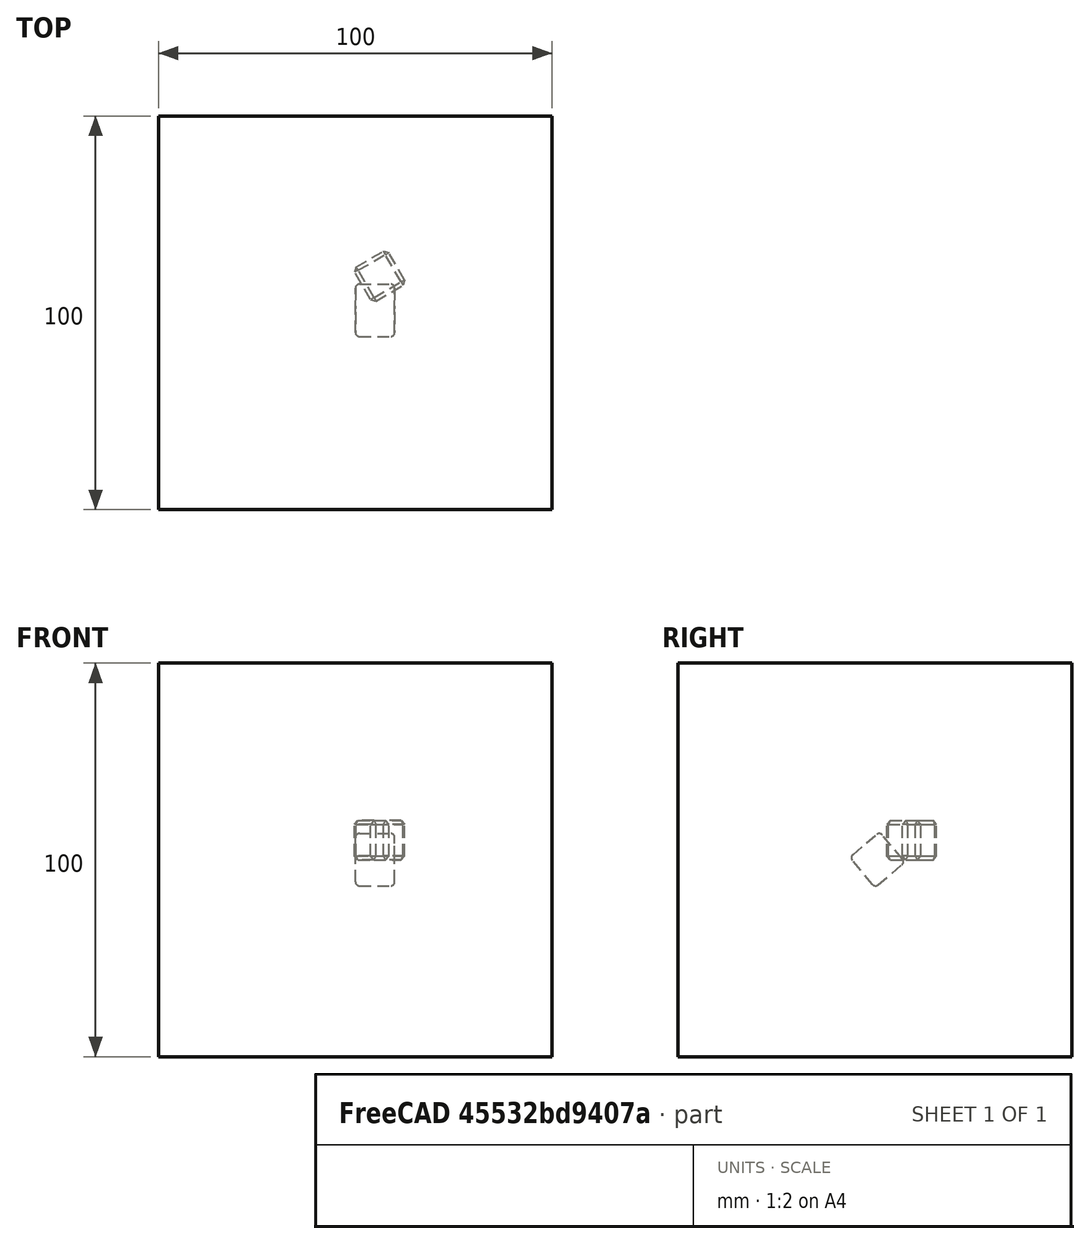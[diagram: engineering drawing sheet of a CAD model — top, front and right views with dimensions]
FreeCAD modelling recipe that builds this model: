
FCSTD DOCUMENT  (FreeCAD 0.21R33694 (Git))
Label: Chamfer_and_fillet
License: All rights reserved
objects: App::DocumentObjectGroupPython×1251, App::Part×3, Part::Box×2, Part::FeaturePython×1, Part::Chamfer×1, Part::Fillet×1
note: 5 computed .brp shape members not serialized (recipe doc carries the construction recipe); baked Part::Feature solids carry a one-line shape summary decoded from their .brp

FEATURE [App::DocumentObjectGroupPython] HALFPI  # scripted group (container) (typed FeaturePython)
  name = HALFPI
  value = pi/2.
FEATURE [App::DocumentObjectGroupPython] PI  # scripted group (container) (typed FeaturePython)
  name = PI
  value = 1.*pi
FEATURE [App::DocumentObjectGroupPython] TWOPI  # scripted group (container) (typed FeaturePython)
  name = TWOPI
  value = 2.*pi
FEATURE [App::DocumentObjectGroupPython] Constants  # scripted group (container) (typed FeaturePython)
  Group = -> [HALFPI,PI,TWOPI]
FEATURE [App::DocumentObjectGroupPython] Variables  # scripted group (container) (typed FeaturePython)
FEATURE [App::DocumentObjectGroupPython] Quantities  # scripted group (container) (typed FeaturePython)
FEATURE [App::DocumentObjectGroupPython] Isotopes  # scripted group (container) (typed FeaturePython)
FEATURE [App::DocumentObjectGroupPython] Elements  # scripted group (container) (typed FeaturePython)
FEATURE [App::DocumentObjectGroupPython] Matrix  # scripted group (container) (typed FeaturePython)
FEATURE [App::DocumentObjectGroupPython] Surfaces  # scripted group (container) (typed FeaturePython)
FEATURE [App::DocumentObjectGroupPython] Opticals  # scripted group (container) (typed FeaturePython)
  Group = -> [Matrix,Surfaces]
FEATURE [App::DocumentObjectGroupPython] G4Isotopes  # scripted group (container) (typed FeaturePython)
FEATURE [App::DocumentObjectGroupPython] H_element  # scripted group (container) (typed FeaturePython)
  Z = 1
  atom_value = 1.008
  formula = H
  name = H_element
FEATURE [App::DocumentObjectGroupPython] He_element  # scripted group (container) (typed FeaturePython)
  Z = 2
  atom_value = 4.0026
  formula = He
  name = He_element
FEATURE [App::DocumentObjectGroupPython] Li_element  # scripted group (container) (typed FeaturePython)
  Z = 3
  atom_value = 6.94
  formula = Li
  name = Li_element
FEATURE [App::DocumentObjectGroupPython] Be_element  # scripted group (container) (typed FeaturePython)
  Z = 4
  atom_value = 9.01218
  formula = Be
  name = Be_element
FEATURE [App::DocumentObjectGroupPython] B_element  # scripted group (container) (typed FeaturePython)
  Z = 5
  atom_value = 10.81
  formula = B
  name = B_element
FEATURE [App::DocumentObjectGroupPython] C_element  # scripted group (container) (typed FeaturePython)
  Z = 6
  atom_value = 12.011
  formula = C
  name = C_element
FEATURE [App::DocumentObjectGroupPython] N_element  # scripted group (container) (typed FeaturePython)
  Z = 7
  atom_value = 14.007
  formula = N
  name = N_element
FEATURE [App::DocumentObjectGroupPython] O_element  # scripted group (container) (typed FeaturePython)
  Z = 8
  atom_value = 15.999
  formula = O
  name = O_element
FEATURE [App::DocumentObjectGroupPython] F_element  # scripted group (container) (typed FeaturePython)
  Z = 9
  atom_value = 18.9984
  formula = F
  name = F_element
FEATURE [App::DocumentObjectGroupPython] Ne_element  # scripted group (container) (typed FeaturePython)
  Z = 10
  atom_value = 20.1797
  formula = Ne
  name = Ne_element
FEATURE [App::DocumentObjectGroupPython] Na_element  # scripted group (container) (typed FeaturePython)
  Z = 11
  atom_value = 22.9898
  formula = Na
  name = Na_element
FEATURE [App::DocumentObjectGroupPython] Mg_element  # scripted group (container) (typed FeaturePython)
  Z = 12
  atom_value = 24.305
  formula = Mg
  name = Mg_element
FEATURE [App::DocumentObjectGroupPython] Al_element  # scripted group (container) (typed FeaturePython)
  Z = 13
  atom_value = 26.9815
  formula = Al
  name = Al_element
FEATURE [App::DocumentObjectGroupPython] Si_element  # scripted group (container) (typed FeaturePython)
  Z = 14
  atom_value = 28.085
  formula = Si
  name = Si_element
FEATURE [App::DocumentObjectGroupPython] P_element  # scripted group (container) (typed FeaturePython)
  Z = 15
  atom_value = 30.9738
  formula = P
  name = P_element
FEATURE [App::DocumentObjectGroupPython] S_element  # scripted group (container) (typed FeaturePython)
  Z = 16
  atom_value = 32.06
  formula = S
  name = S_element
FEATURE [App::DocumentObjectGroupPython] Cl_element  # scripted group (container) (typed FeaturePython)
  Z = 17
  atom_value = 35.45
  formula = Cl
  name = Cl_element
FEATURE [App::DocumentObjectGroupPython] Ar_element  # scripted group (container) (typed FeaturePython)
  Z = 18
  atom_value = 39.95
  formula = Ar
  name = Ar_element
FEATURE [App::DocumentObjectGroupPython] K_element  # scripted group (container) (typed FeaturePython)
  Z = 19
  atom_value = 39.0983
  formula = K
  name = K_element
FEATURE [App::DocumentObjectGroupPython] Ca_element  # scripted group (container) (typed FeaturePython)
  Z = 20
  atom_value = 40.078
  formula = Ca
  name = Ca_element
FEATURE [App::DocumentObjectGroupPython] Sc_element  # scripted group (container) (typed FeaturePython)
  Z = 21
  atom_value = 44.9559
  formula = Sc
  name = Sc_element
FEATURE [App::DocumentObjectGroupPython] Ti_element  # scripted group (container) (typed FeaturePython)
  Z = 22
  atom_value = 47.867
  formula = Ti
  name = Ti_element
FEATURE [App::DocumentObjectGroupPython] V_element  # scripted group (container) (typed FeaturePython)
  Z = 23
  atom_value = 50.9415
  formula = V
  name = V_element
FEATURE [App::DocumentObjectGroupPython] Cr_element  # scripted group (container) (typed FeaturePython)
  Z = 24
  atom_value = 51.9961
  formula = Cr
  name = Cr_element
FEATURE [App::DocumentObjectGroupPython] Mn_element  # scripted group (container) (typed FeaturePython)
  Z = 25
  atom_value = 54.938
  formula = Mn
  name = Mn_element
FEATURE [App::DocumentObjectGroupPython] Fe_element  # scripted group (container) (typed FeaturePython)
  Z = 26
  atom_value = 55.845
  formula = Fe
  name = Fe_element
FEATURE [App::DocumentObjectGroupPython] Co_element  # scripted group (container) (typed FeaturePython)
  Z = 27
  atom_value = 58.9332
  formula = Co
  name = Co_element
FEATURE [App::DocumentObjectGroupPython] Ni_element  # scripted group (container) (typed FeaturePython)
  Z = 28
  atom_value = 58.6934
  formula = Ni
  name = Ni_element
FEATURE [App::DocumentObjectGroupPython] Cu_element  # scripted group (container) (typed FeaturePython)
  Z = 29
  atom_value = 63.546
  formula = Cu
  name = Cu_element
FEATURE [App::DocumentObjectGroupPython] Zn_element  # scripted group (container) (typed FeaturePython)
  Z = 30
  atom_value = 65.38
  formula = Zn
  name = Zn_element
FEATURE [App::DocumentObjectGroupPython] Ga_element  # scripted group (container) (typed FeaturePython)
  Z = 31
  atom_value = 69.723
  formula = Ga
  name = Ga_element
FEATURE [App::DocumentObjectGroupPython] Ge_element  # scripted group (container) (typed FeaturePython)
  Z = 32
  atom_value = 72.63
  formula = Ge
  name = Ge_element
FEATURE [App::DocumentObjectGroupPython] As_element  # scripted group (container) (typed FeaturePython)
  Z = 33
  atom_value = 74.9216
  formula = As
  name = As_element
FEATURE [App::DocumentObjectGroupPython] Se_element  # scripted group (container) (typed FeaturePython)
  Z = 34
  atom_value = 78.971
  formula = Se
  name = Se_element
FEATURE [App::DocumentObjectGroupPython] Br_element  # scripted group (container) (typed FeaturePython)
  Z = 35
  atom_value = 79.904
  formula = Br
  name = Br_element
FEATURE [App::DocumentObjectGroupPython] Kr_element  # scripted group (container) (typed FeaturePython)
  Z = 36
  atom_value = 83.798
  formula = Kr
  name = Kr_element
FEATURE [App::DocumentObjectGroupPython] Rb_element  # scripted group (container) (typed FeaturePython)
  Z = 37
  atom_value = 85.4678
  formula = Rb
  name = Rb_element
FEATURE [App::DocumentObjectGroupPython] Sr_element  # scripted group (container) (typed FeaturePython)
  Z = 38
  atom_value = 87.62
  formula = Sr
  name = Sr_element
FEATURE [App::DocumentObjectGroupPython] Y_element  # scripted group (container) (typed FeaturePython)
  Z = 39
  atom_value = 88.9058
  formula = Y
  name = Y_element
FEATURE [App::DocumentObjectGroupPython] Zr_element  # scripted group (container) (typed FeaturePython)
  Z = 40
  atom_value = 91.224
  formula = Zr
  name = Zr_element
FEATURE [App::DocumentObjectGroupPython] Nb_element  # scripted group (container) (typed FeaturePython)
  Z = 41
  atom_value = 92.9064
  formula = Nb
  name = Nb_element
FEATURE [App::DocumentObjectGroupPython] Mo_element  # scripted group (container) (typed FeaturePython)
  Z = 42
  atom_value = 95.95
  formula = Mo
  name = Mo_element
FEATURE [App::DocumentObjectGroupPython] Tc_element  # scripted group (container) (typed FeaturePython)
  Z = 43
  atom_value = 97
  formula = Tc
  name = Tc_element
FEATURE [App::DocumentObjectGroupPython] Ru_element  # scripted group (container) (typed FeaturePython)
  Z = 44
  atom_value = 101.07
  formula = Ru
  name = Ru_element
FEATURE [App::DocumentObjectGroupPython] Rh_element  # scripted group (container) (typed FeaturePython)
  Z = 45
  atom_value = 102.905
  formula = Rh
  name = Rh_element
FEATURE [App::DocumentObjectGroupPython] Pd_element  # scripted group (container) (typed FeaturePython)
  Z = 46
  atom_value = 106.42
  formula = Pd
  name = Pd_element
FEATURE [App::DocumentObjectGroupPython] Ag_element  # scripted group (container) (typed FeaturePython)
  Z = 47
  atom_value = 107.868
  formula = Ag
  name = Ag_element
FEATURE [App::DocumentObjectGroupPython] Cd_element  # scripted group (container) (typed FeaturePython)
  Z = 48
  atom_value = 112.414
  formula = Cd
  name = Cd_element
FEATURE [App::DocumentObjectGroupPython] In_element  # scripted group (container) (typed FeaturePython)
  Z = 49
  atom_value = 114.818
  formula = In
  name = In_element
FEATURE [App::DocumentObjectGroupPython] Sn_element  # scripted group (container) (typed FeaturePython)
  Z = 50
  atom_value = 118.71
  formula = Sn
  name = Sn_element
FEATURE [App::DocumentObjectGroupPython] Sb_element  # scripted group (container) (typed FeaturePython)
  Z = 51
  atom_value = 121.76
  formula = Sb
  name = Sb_element
FEATURE [App::DocumentObjectGroupPython] Te_element  # scripted group (container) (typed FeaturePython)
  Z = 52
  atom_value = 127.6
  formula = Te
  name = Te_element
FEATURE [App::DocumentObjectGroupPython] I_element  # scripted group (container) (typed FeaturePython)
  Z = 53
  atom_value = 126.904
  formula = I
  name = I_element
FEATURE [App::DocumentObjectGroupPython] Xe_element  # scripted group (container) (typed FeaturePython)
  Z = 54
  atom_value = 131.293
  formula = Xe
  name = Xe_element
FEATURE [App::DocumentObjectGroupPython] Cs_element  # scripted group (container) (typed FeaturePython)
  Z = 55
  atom_value = 132.905
  formula = Cs
  name = Cs_element
FEATURE [App::DocumentObjectGroupPython] Ba_element  # scripted group (container) (typed FeaturePython)
  Z = 56
  atom_value = 137.327
  formula = Ba
  name = Ba_element
FEATURE [App::DocumentObjectGroupPython] La_element  # scripted group (container) (typed FeaturePython)
  Z = 57
  atom_value = 138.905
  formula = La
  name = La_element
FEATURE [App::DocumentObjectGroupPython] Ce_element  # scripted group (container) (typed FeaturePython)
  Z = 58
  atom_value = 140.116
  formula = Ce
  name = Ce_element
FEATURE [App::DocumentObjectGroupPython] Pr_element  # scripted group (container) (typed FeaturePython)
  Z = 59
  atom_value = 140.908
  formula = Pr
  name = Pr_element
FEATURE [App::DocumentObjectGroupPython] Nd_element  # scripted group (container) (typed FeaturePython)
  Z = 60
  atom_value = 144.242
  formula = Nd
  name = Nd_element
FEATURE [App::DocumentObjectGroupPython] Pm_element  # scripted group (container) (typed FeaturePython)
  Z = 61
  atom_value = 145
  formula = Pm
  name = Pm_element
FEATURE [App::DocumentObjectGroupPython] Sm_element  # scripted group (container) (typed FeaturePython)
  Z = 62
  atom_value = 150.36
  formula = Sm
  name = Sm_element
FEATURE [App::DocumentObjectGroupPython] Eu_element  # scripted group (container) (typed FeaturePython)
  Z = 63
  atom_value = 151.964
  formula = Eu
  name = Eu_element
FEATURE [App::DocumentObjectGroupPython] Gd_element  # scripted group (container) (typed FeaturePython)
  Z = 64
  atom_value = 157.25
  formula = Gd
  name = Gd_element
FEATURE [App::DocumentObjectGroupPython] Tb_element  # scripted group (container) (typed FeaturePython)
  Z = 65
  atom_value = 158.925
  formula = Tb
  name = Tb_element
FEATURE [App::DocumentObjectGroupPython] Dy_element  # scripted group (container) (typed FeaturePython)
  Z = 66
  atom_value = 162.5
  formula = Dy
  name = Dy_element
FEATURE [App::DocumentObjectGroupPython] Ho_element  # scripted group (container) (typed FeaturePython)
  Z = 67
  atom_value = 164.93
  formula = Ho
  name = Ho_element
FEATURE [App::DocumentObjectGroupPython] Er_element  # scripted group (container) (typed FeaturePython)
  Z = 68
  atom_value = 167.259
  formula = Er
  name = Er_element
FEATURE [App::DocumentObjectGroupPython] Tm_element  # scripted group (container) (typed FeaturePython)
  Z = 69
  atom_value = 168.934
  formula = Tm
  name = Tm_element
FEATURE [App::DocumentObjectGroupPython] Yb_element  # scripted group (container) (typed FeaturePython)
  Z = 70
  atom_value = 173.045
  formula = Yb
  name = Yb_element
FEATURE [App::DocumentObjectGroupPython] Lu_element  # scripted group (container) (typed FeaturePython)
  Z = 71
  atom_value = 174.967
  formula = Lu
  name = Lu_element
FEATURE [App::DocumentObjectGroupPython] Hf_element  # scripted group (container) (typed FeaturePython)
  Z = 72
  atom_value = 178.49
  formula = Hf
  name = Hf_element
FEATURE [App::DocumentObjectGroupPython] Ta_element  # scripted group (container) (typed FeaturePython)
  Z = 73
  atom_value = 180.948
  formula = Ta
  name = Ta_element
FEATURE [App::DocumentObjectGroupPython] W_element  # scripted group (container) (typed FeaturePython)
  Z = 74
  atom_value = 183.84
  formula = W
  name = W_element
FEATURE [App::DocumentObjectGroupPython] Re_element  # scripted group (container) (typed FeaturePython)
  Z = 75
  atom_value = 186.207
  formula = Re
  name = Re_element
FEATURE [App::DocumentObjectGroupPython] Os_element  # scripted group (container) (typed FeaturePython)
  Z = 76
  atom_value = 190.23
  formula = Os
  name = Os_element
FEATURE [App::DocumentObjectGroupPython] Ir_element  # scripted group (container) (typed FeaturePython)
  Z = 77
  atom_value = 192.217
  formula = Ir
  name = Ir_element
FEATURE [App::DocumentObjectGroupPython] Pt_element  # scripted group (container) (typed FeaturePython)
  Z = 78
  atom_value = 195.084
  formula = Pt
  name = Pt_element
FEATURE [App::DocumentObjectGroupPython] Au_element  # scripted group (container) (typed FeaturePython)
  Z = 79
  atom_value = 196.967
  formula = Au
  name = Au_element
FEATURE [App::DocumentObjectGroupPython] Hg_element  # scripted group (container) (typed FeaturePython)
  Z = 80
  atom_value = 200.592
  formula = Hg
  name = Hg_element
FEATURE [App::DocumentObjectGroupPython] Tl_element  # scripted group (container) (typed FeaturePython)
  Z = 81
  atom_value = 204.38
  formula = Tl
  name = Tl_element
FEATURE [App::DocumentObjectGroupPython] Pb_element  # scripted group (container) (typed FeaturePython)
  Z = 82
  atom_value = 207.2
  formula = Pb
  name = Pb_element
FEATURE [App::DocumentObjectGroupPython] Bi_element  # scripted group (container) (typed FeaturePython)
  Z = 83
  atom_value = 208.98
  formula = Bi
  name = Bi_element
FEATURE [App::DocumentObjectGroupPython] Po_element  # scripted group (container) (typed FeaturePython)
  Z = 84
  atom_value = 209
  formula = Po
  name = Po_element
FEATURE [App::DocumentObjectGroupPython] At_element  # scripted group (container) (typed FeaturePython)
  Z = 85
  atom_value = 210
  formula = At
  name = At_element
FEATURE [App::DocumentObjectGroupPython] Rn_element  # scripted group (container) (typed FeaturePython)
  Z = 86
  atom_value = 222
  formula = Rn
  name = Rn_element
FEATURE [App::DocumentObjectGroupPython] Fr_element  # scripted group (container) (typed FeaturePython)
  Z = 87
  atom_value = 223
  formula = Fr
  name = Fr_element
FEATURE [App::DocumentObjectGroupPython] Ra_element  # scripted group (container) (typed FeaturePython)
  Z = 88
  atom_value = 226
  formula = Ra
  name = Ra_element
FEATURE [App::DocumentObjectGroupPython] Ac_element  # scripted group (container) (typed FeaturePython)
  Z = 89
  atom_value = 227
  formula = Ac
  name = Ac_element
FEATURE [App::DocumentObjectGroupPython] Th_element  # scripted group (container) (typed FeaturePython)
  Z = 90
  atom_value = 232.038
  formula = Th
  name = Th_element
FEATURE [App::DocumentObjectGroupPython] Pa_element  # scripted group (container) (typed FeaturePython)
  Z = 91
  atom_value = 231.036
  formula = Pa
  name = Pa_element
FEATURE [App::DocumentObjectGroupPython] U_element  # scripted group (container) (typed FeaturePython)
  Z = 92
  atom_value = 238.029
  formula = U
  name = U_element
FEATURE [App::DocumentObjectGroupPython] Np_element  # scripted group (container) (typed FeaturePython)
  Z = 93
  atom_value = 237
  formula = Np
  name = Np_element
FEATURE [App::DocumentObjectGroupPython] Pu_element  # scripted group (container) (typed FeaturePython)
  Z = 94
  atom_value = 244
  formula = Pu
  name = Pu_element
FEATURE [App::DocumentObjectGroupPython] Am_element  # scripted group (container) (typed FeaturePython)
  Z = 95
  atom_value = 243
  formula = Am
  name = Am_element
FEATURE [App::DocumentObjectGroupPython] Cm_element  # scripted group (container) (typed FeaturePython)
  Z = 96
  atom_value = 247
  formula = Cm
  name = Cm_element
FEATURE [App::DocumentObjectGroupPython] Bk_element  # scripted group (container) (typed FeaturePython)
  Z = 97
  atom_value = 247
  formula = Bk
  name = Bk_element
FEATURE [App::DocumentObjectGroupPython] Cf_element  # scripted group (container) (typed FeaturePython)
  Z = 98
  atom_value = 251
  formula = Cf
  name = Cf_element
FEATURE [App::DocumentObjectGroupPython] G4Elements  # scripted group (container) (typed FeaturePython)
  Group = -> [H_element,He_element,Li_element,Be_element,B_element,C_element,N_element,O_element,F_element,Ne_element,Na_element,Mg_element,Al_element,Si_element,P_element,S_element,Cl_element,Ar_element,K_element,Ca_element,Sc_element,Ti_element,V_element,Cr_element,Mn_element,Fe_element,Co_element,Ni_element,Cu_element,Zn_element,Ga_element,Ge_element,As_element,Se_element,Br_element,Kr_element,Rb_element,+61 more]
FEATURE [App::DocumentObjectGroupPython] H_element001  label="H_element : 0.101"  # scripted group (container) (typed FeaturePython)
  n = 0.101327
FEATURE [App::DocumentObjectGroupPython] C_element001  label="C_element : 0.775"  # scripted group (container) (typed FeaturePython)
  n = 0.7755
FEATURE [App::DocumentObjectGroupPython] N_element001  label="N_element : 0.035"  # scripted group (container) (typed FeaturePython)
  n = 0.035057
FEATURE [App::DocumentObjectGroupPython] O_element001  label="O_element : 0.052"  # scripted group (container) (typed FeaturePython)
  n = 0.0523159
FEATURE [App::DocumentObjectGroupPython] F_element001  label="F_element : 0.017"  # scripted group (container) (typed FeaturePython)
  n = 0.017422
FEATURE [App::DocumentObjectGroupPython] Ca_element001  label="Ca_element : 0.018"  # scripted group (container) (typed FeaturePython)
  n = 0.018378
FEATURE [App::DocumentObjectGroupPython] G4_A_150_TISSUE  label="G4_A-150_TISSUE"  # scripted group (container) (typed FeaturePython)
  Dunit = g/cm3
  Dvalue = 1.127
  Group = -> [H_element001,C_element001,N_element001,O_element001,F_element001,Ca_element001]
  conduct = 2
  density = 1
  expand = 3
  formula = G4_A-150_TISSUE
  name = G4_A-150_TISSUE
  specific = 4
FEATURE [App::DocumentObjectGroupPython] C_element002  label="C_element : 3"  # scripted group (container) (typed FeaturePython)
  n = 3
  ref = C_element
FEATURE [App::DocumentObjectGroupPython] H_element002  label="H_element : 6"  # scripted group (container) (typed FeaturePython)
  n = 6
  ref = H_element
FEATURE [App::DocumentObjectGroupPython] O_element002  label="O_element : 1"  # scripted group (container) (typed FeaturePython)
  n = 1
  ref = O_element
FEATURE [App::DocumentObjectGroupPython] G4_ACETONE  # scripted group (container) (typed FeaturePython)
  Dunit = g/cm3
  Dvalue = 0.7899
  Group = -> [C_element002,H_element002,O_element002]
  conduct = 2
  density = 1
  expand = 3
  formula = G4_ACETONE
  name = G4_ACETONE
  specific = 4
FEATURE [App::DocumentObjectGroupPython] C_element003  label="C_element : 2"  # scripted group (container) (typed FeaturePython)
  n = 2
  ref = C_element
FEATURE [App::DocumentObjectGroupPython] H_element003  label="H_element : 2"  # scripted group (container) (typed FeaturePython)
  n = 2
  ref = H_element
FEATURE [App::DocumentObjectGroupPython] G4_ACETYLENE  # scripted group (container) (typed FeaturePython)
  Dunit = g/cm3
  Dvalue = 0.0010967
  Group = -> [C_element003,H_element003]
  conduct = 2
  density = 1
  expand = 3
  formula = G4_ACETYLENE
  name = G4_ACETYLENE
  specific = 4
FEATURE [App::DocumentObjectGroupPython] C_element004  label="C_element : 5"  # scripted group (container) (typed FeaturePython)
  n = 5
  ref = C_element
FEATURE [App::DocumentObjectGroupPython] H_element004  label="H_element : 5"  # scripted group (container) (typed FeaturePython)
  n = 5
  ref = H_element
FEATURE [App::DocumentObjectGroupPython] N_element002  label="N_element : 5"  # scripted group (container) (typed FeaturePython)
  n = 5
  ref = N_element
FEATURE [App::DocumentObjectGroupPython] G4_ADENINE  # scripted group (container) (typed FeaturePython)
  Dunit = g/cm3
  Dvalue = 1.6
  Group = -> [C_element004,H_element004,N_element002]
  conduct = 2
  density = 1
  expand = 3
  formula = G4_ADENINE
  name = G4_ADENINE
  specific = 4
FEATURE [App::DocumentObjectGroupPython] H_element005  label="H_element : 0.114"  # scripted group (container) (typed FeaturePython)
  n = 0.114
FEATURE [App::DocumentObjectGroupPython] C_element005  label="C_element : 0.598"  # scripted group (container) (typed FeaturePython)
  n = 0.598
FEATURE [App::DocumentObjectGroupPython] N_element003  label="N_element : 0.007"  # scripted group (container) (typed FeaturePython)
  n = 0.007
FEATURE [App::DocumentObjectGroupPython] O_element003  label="O_element : 0.278"  # scripted group (container) (typed FeaturePython)
  n = 0.278
FEATURE [App::DocumentObjectGroupPython] Na_element001  label="Na_element : 0.001"  # scripted group (container) (typed FeaturePython)
  n = 0.001
FEATURE [App::DocumentObjectGroupPython] S_element001  label="S_element : 0.001"  # scripted group (container) (typed FeaturePython)
  n = 0.001
FEATURE [App::DocumentObjectGroupPython] Cl_element001  label="Cl_element : 0.001"  # scripted group (container) (typed FeaturePython)
  n = 0.001
FEATURE [App::DocumentObjectGroupPython] G4_ADIPOSE_TISSUE_ICRP  # scripted group (container) (typed FeaturePython)
  Dunit = g/cm3
  Dvalue = 0.95
  Group = -> [H_element005,C_element005,N_element003,O_element003,Na_element001,S_element001,Cl_element001]
  conduct = 2
  density = 1
  expand = 3
  formula = G4_ADIPOSE_TISSUE_ICRP
  name = G4_ADIPOSE_TISSUE_ICRP
  specific = 4
FEATURE [App::DocumentObjectGroupPython] C_element006  label="C_element : 0.000"  # scripted group (container) (typed FeaturePython)
  n = 0.000124
FEATURE [App::DocumentObjectGroupPython] N_element004  label="N_element : 0.755"  # scripted group (container) (typed FeaturePython)
  n = 0.755268
FEATURE [App::DocumentObjectGroupPython] O_element004  label="O_element : 0.232"  # scripted group (container) (typed FeaturePython)
  n = 0.231781
FEATURE [App::DocumentObjectGroupPython] Ar_element001  label="Ar_element : 0.013"  # scripted group (container) (typed FeaturePython)
  n = 0.012827
FEATURE [App::DocumentObjectGroupPython] G4_AIR  # scripted group (container) (typed FeaturePython)
  Dunit = g/cm3
  Dvalue = 0.00120479
  Group = -> [C_element006,N_element004,O_element004,Ar_element001]
  conduct = 2
  density = 1
  expand = 3
  formula = G4_AIR
  name = G4_AIR
  specific = 4
FEATURE [App::DocumentObjectGroupPython] C_element007  label="C_element : 006"  # scripted group (container) (typed FeaturePython)
  n = 3
  ref = C_element
FEATURE [App::DocumentObjectGroupPython] H_element006  label="H_element : 7"  # scripted group (container) (typed FeaturePython)
  n = 7
  ref = H_element
FEATURE [App::DocumentObjectGroupPython] N_element005  label="N_element : 1"  # scripted group (container) (typed FeaturePython)
  n = 1
  ref = N_element
FEATURE [App::DocumentObjectGroupPython] O_element005  label="O_element : 2"  # scripted group (container) (typed FeaturePython)
  n = 2
  ref = O_element
FEATURE [App::DocumentObjectGroupPython] G4_ALANINE  # scripted group (container) (typed FeaturePython)
  Dunit = g/cm3
  Dvalue = 1.42
  Group = -> [C_element007,H_element006,N_element005,O_element005]
  conduct = 2
  density = 1
  expand = 3
  formula = G4_ALANINE
  name = G4_ALANINE
  specific = 4
FEATURE [App::DocumentObjectGroupPython] Al_element001  label="Al_element : 2"  # scripted group (container) (typed FeaturePython)
  n = 2
  ref = Al_element
FEATURE [App::DocumentObjectGroupPython] O_element006  label="O_element : 3"  # scripted group (container) (typed FeaturePython)
  n = 3
  ref = O_element
FEATURE [App::DocumentObjectGroupPython] G4_ALUMINUM_OXIDE  # scripted group (container) (typed FeaturePython)
  Dunit = g/cm3
  Dvalue = 3.97
  Group = -> [Al_element001,O_element006]
  conduct = 2
  density = 1
  expand = 3
  formula = G4_ALUMINUM_OXIDE
  name = G4_ALUMINUM_OXIDE
  specific = 4
FEATURE [App::DocumentObjectGroupPython] H_element007  label="H_element : 0.106"  # scripted group (container) (typed FeaturePython)
  n = 0.10593
FEATURE [App::DocumentObjectGroupPython] C_element008  label="C_element : 0.789"  # scripted group (container) (typed FeaturePython)
  n = 0.788974
FEATURE [App::DocumentObjectGroupPython] O_element007  label="O_element : 0.105"  # scripted group (container) (typed FeaturePython)
  n = 0.105096
FEATURE [App::DocumentObjectGroupPython] G4_AMBER  # scripted group (container) (typed FeaturePython)
  Dunit = g/cm3
  Dvalue = 1.1
  Group = -> [H_element007,C_element008,O_element007]
  conduct = 2
  density = 1
  expand = 3
  formula = G4_AMBER
  name = G4_AMBER
  specific = 4
FEATURE [App::DocumentObjectGroupPython] N_element006  label="N_element : 006"  # scripted group (container) (typed FeaturePython)
  n = 1
  ref = N_element
FEATURE [App::DocumentObjectGroupPython] H_element008  label="H_element : 3"  # scripted group (container) (typed FeaturePython)
  n = 3
  ref = H_element
FEATURE [App::DocumentObjectGroupPython] G4_AMMONIA  # scripted group (container) (typed FeaturePython)
  Dunit = g/cm3
  Dvalue = 0.000826019
  Group = -> [N_element006,H_element008]
  conduct = 2
  density = 1
  expand = 3
  formula = G4_AMMONIA
  name = G4_AMMONIA
  specific = 4
FEATURE [App::DocumentObjectGroupPython] C_element009  label="C_element : 6"  # scripted group (container) (typed FeaturePython)
  n = 6
  ref = C_element
FEATURE [App::DocumentObjectGroupPython] H_element009  label="H_element : 008"  # scripted group (container) (typed FeaturePython)
  n = 7
  ref = H_element
FEATURE [App::DocumentObjectGroupPython] N_element007  label="N_element : 007"  # scripted group (container) (typed FeaturePython)
  n = 1
  ref = N_element
FEATURE [App::DocumentObjectGroupPython] G4_ANILINE  # scripted group (container) (typed FeaturePython)
  Dunit = g/cm3
  Dvalue = 1.0235
  Group = -> [C_element009,H_element009,N_element007]
  conduct = 2
  density = 1
  expand = 3
  formula = G4_ANILINE
  name = G4_ANILINE
  specific = 4
FEATURE [App::DocumentObjectGroupPython] C_element010  label="C_element : 14"  # scripted group (container) (typed FeaturePython)
  n = 14
  ref = C_element
FEATURE [App::DocumentObjectGroupPython] H_element010  label="H_element : 10"  # scripted group (container) (typed FeaturePython)
  n = 10
  ref = H_element
FEATURE [App::DocumentObjectGroupPython] G4_ANTHRACENE  # scripted group (container) (typed FeaturePython)
  Dunit = g/cm3
  Dvalue = 1.283
  Group = -> [C_element010,H_element010]
  conduct = 2
  density = 1
  expand = 3
  formula = G4_ANTHRACENE
  name = G4_ANTHRACENE
  specific = 4
FEATURE [App::DocumentObjectGroupPython] H_element011  label="H_element : 0.065"  # scripted group (container) (typed FeaturePython)
  n = 0.0654709
FEATURE [App::DocumentObjectGroupPython] C_element011  label="C_element : 0.537"  # scripted group (container) (typed FeaturePython)
  n = 0.536944
FEATURE [App::DocumentObjectGroupPython] N_element008  label="N_element : 0.021"  # scripted group (container) (typed FeaturePython)
  n = 0.0215
FEATURE [App::DocumentObjectGroupPython] O_element008  label="O_element : 0.032"  # scripted group (container) (typed FeaturePython)
  n = 0.032085
FEATURE [App::DocumentObjectGroupPython] F_element002  label="F_element : 0.167"  # scripted group (container) (typed FeaturePython)
  n = 0.167411
FEATURE [App::DocumentObjectGroupPython] Ca_element002  label="Ca_element : 0.177"  # scripted group (container) (typed FeaturePython)
  n = 0.176589
FEATURE [App::DocumentObjectGroupPython] G4_B_100_BONE  label="G4_B-100_BONE"  # scripted group (container) (typed FeaturePython)
  Dunit = g/cm3
  Dvalue = 1.45
  Group = -> [H_element011,C_element011,N_element008,O_element008,F_element002,Ca_element002]
  conduct = 2
  density = 1
  expand = 3
  formula = G4_B-100_BONE
  name = G4_B-100_BONE
  specific = 4
FEATURE [App::DocumentObjectGroupPython] H_element012  label="H_element : 0.057"  # scripted group (container) (typed FeaturePython)
  n = 0.057441
FEATURE [App::DocumentObjectGroupPython] C_element012  label="C_element : 0.790"  # scripted group (container) (typed FeaturePython)
  n = 0.774591
FEATURE [App::DocumentObjectGroupPython] O_element009  label="O_element : 0.168"  # scripted group (container) (typed FeaturePython)
  n = 0.167968
FEATURE [App::DocumentObjectGroupPython] G4_BAKELITE  # scripted group (container) (typed FeaturePython)
  Dunit = g/cm3
  Dvalue = 1.25
  Group = -> [H_element012,C_element012,O_element009]
  conduct = 2
  density = 1
  expand = 3
  formula = G4_BAKELITE
  name = G4_BAKELITE
  specific = 4
FEATURE [App::DocumentObjectGroupPython] Ba_element001  label="Ba_element : 1"  # scripted group (container) (typed FeaturePython)
  n = 1
  ref = Ba_element
FEATURE [App::DocumentObjectGroupPython] F_element003  label="F_element : 2"  # scripted group (container) (typed FeaturePython)
  n = 2
  ref = F_element
FEATURE [App::DocumentObjectGroupPython] G4_BARIUM_FLUORIDE  # scripted group (container) (typed FeaturePython)
  Dunit = g/cm3
  Dvalue = 4.89
  Group = -> [Ba_element001,F_element003]
  conduct = 2
  density = 1
  expand = 3
  formula = G4_BARIUM_FLUORIDE
  name = G4_BARIUM_FLUORIDE
  specific = 4
FEATURE [App::DocumentObjectGroupPython] Ba_element002  label="Ba_element : 002"  # scripted group (container) (typed FeaturePython)
  n = 1
  ref = Ba_element
FEATURE [App::DocumentObjectGroupPython] S_element002  label="S_element : 1"  # scripted group (container) (typed FeaturePython)
  n = 1
  ref = S_element
FEATURE [App::DocumentObjectGroupPython] O_element010  label="O_element : 4"  # scripted group (container) (typed FeaturePython)
  n = 4
  ref = O_element
FEATURE [App::DocumentObjectGroupPython] G4_BARIUM_SULFATE  # scripted group (container) (typed FeaturePython)
  Dunit = g/cm3
  Dvalue = 4.5
  Group = -> [Ba_element002,S_element002,O_element010]
  conduct = 2
  density = 1
  expand = 3
  formula = G4_BARIUM_SULFATE
  name = G4_BARIUM_SULFATE
  specific = 4
FEATURE [App::DocumentObjectGroupPython] C_element013  label="C_element : 007"  # scripted group (container) (typed FeaturePython)
  n = 6
  ref = C_element
FEATURE [App::DocumentObjectGroupPython] H_element013  label="H_element : 009"  # scripted group (container) (typed FeaturePython)
  n = 6
  ref = H_element
FEATURE [App::DocumentObjectGroupPython] G4_BENZENE  # scripted group (container) (typed FeaturePython)
  Dunit = g/cm3
  Dvalue = 0.87865
  Group = -> [C_element013,H_element013]
  conduct = 2
  density = 1
  expand = 3
  formula = G4_BENZENE
  name = G4_BENZENE
  specific = 4
FEATURE [App::DocumentObjectGroupPython] Be_element001  label="Be_element : 1"  # scripted group (container) (typed FeaturePython)
  n = 1
  ref = Be_element
FEATURE [App::DocumentObjectGroupPython] O_element011  label="O_element : 005"  # scripted group (container) (typed FeaturePython)
  n = 1
  ref = O_element
FEATURE [App::DocumentObjectGroupPython] G4_BERYLLIUM_OXIDE  # scripted group (container) (typed FeaturePython)
  Dunit = g/cm3
  Dvalue = 3.01
  Group = -> [Be_element001,O_element011]
  conduct = 2
  density = 1
  expand = 3
  formula = G4_BERYLLIUM_OXIDE
  name = G4_BERYLLIUM_OXIDE
  specific = 4
FEATURE [App::DocumentObjectGroupPython] Bi_element001  label="Bi_element : 4"  # scripted group (container) (typed FeaturePython)
  n = 4
  ref = Bi_element
FEATURE [App::DocumentObjectGroupPython] Ge_element001  label="Ge_element : 3"  # scripted group (container) (typed FeaturePython)
  n = 3
  ref = Ge_element
FEATURE [App::DocumentObjectGroupPython] O_element012  label="O_element : 12"  # scripted group (container) (typed FeaturePython)
  n = 12
  ref = O_element
FEATURE [App::DocumentObjectGroupPython] G4_BGO  # scripted group (container) (typed FeaturePython)
  Dunit = g/cm3
  Dvalue = 7.13
  Group = -> [Bi_element001,Ge_element001,O_element012]
  conduct = 2
  density = 1
  expand = 3
  formula = G4_BGO
  name = G4_BGO
  specific = 4
FEATURE [App::DocumentObjectGroupPython] H_element014  label="H_element : 0.102"  # scripted group (container) (typed FeaturePython)
  n = 0.102
FEATURE [App::DocumentObjectGroupPython] C_element014  label="C_element : 0.110"  # scripted group (container) (typed FeaturePython)
  n = 0.11
FEATURE [App::DocumentObjectGroupPython] N_element009  label="N_element : 0.033"  # scripted group (container) (typed FeaturePython)
  n = 0.033
FEATURE [App::DocumentObjectGroupPython] O_element013  label="O_element : 0.745"  # scripted group (container) (typed FeaturePython)
  n = 0.745
FEATURE [App::DocumentObjectGroupPython] Na_element002  label="Na_element : 0.002"  # scripted group (container) (typed FeaturePython)
  n = 0.001
FEATURE [App::DocumentObjectGroupPython] P_element001  label="P_element : 0.001"  # scripted group (container) (typed FeaturePython)
  n = 0.001
FEATURE [App::DocumentObjectGroupPython] S_element003  label="S_element : 0.002"  # scripted group (container) (typed FeaturePython)
  n = 0.002
FEATURE [App::DocumentObjectGroupPython] Cl_element002  label="Cl_element : 0.003"  # scripted group (container) (typed FeaturePython)
  n = 0.003
FEATURE [App::DocumentObjectGroupPython] K_element001  label="K_element : 0.002"  # scripted group (container) (typed FeaturePython)
  n = 0.002
FEATURE [App::DocumentObjectGroupPython] Fe_element001  label="Fe_element : 0.001"  # scripted group (container) (typed FeaturePython)
  n = 0.001
FEATURE [App::DocumentObjectGroupPython] G4_BLOOD_ICRP  # scripted group (container) (typed FeaturePython)
  Dunit = g/cm3
  Dvalue = 1.06
  Group = -> [H_element014,C_element014,N_element009,O_element013,Na_element002,P_element001,S_element003,Cl_element002,K_element001,Fe_element001]
  conduct = 2
  density = 1
  expand = 3
  formula = G4_BLOOD_ICRP
  name = G4_BLOOD_ICRP
  specific = 4
FEATURE [App::DocumentObjectGroupPython] H_element015  label="H_element : 0.064"  # scripted group (container) (typed FeaturePython)
  n = 0.064
FEATURE [App::DocumentObjectGroupPython] C_element015  label="C_element : 0.278"  # scripted group (container) (typed FeaturePython)
  n = 0.278
FEATURE [App::DocumentObjectGroupPython] N_element010  label="N_element : 0.027"  # scripted group (container) (typed FeaturePython)
  n = 0.027
FEATURE [App::DocumentObjectGroupPython] O_element014  label="O_element : 0.410"  # scripted group (container) (typed FeaturePython)
  n = 0.41
FEATURE [App::DocumentObjectGroupPython] Mg_element001  label="Mg_element : 0.002"  # scripted group (container) (typed FeaturePython)
  n = 0.002
FEATURE [App::DocumentObjectGroupPython] P_element002  label="P_element : 0.070"  # scripted group (container) (typed FeaturePython)
  n = 0.07
FEATURE [App::DocumentObjectGroupPython] S_element004  label="S_element : 0.003"  # scripted group (container) (typed FeaturePython)
  n = 0.002
FEATURE [App::DocumentObjectGroupPython] Ca_element003  label="Ca_element : 0.147"  # scripted group (container) (typed FeaturePython)
  n = 0.147
FEATURE [App::DocumentObjectGroupPython] G4_BONE_COMPACT_ICRU  # scripted group (container) (typed FeaturePython)
  Dunit = g/cm3
  Dvalue = 1.85
  Group = -> [H_element015,C_element015,N_element010,O_element014,Mg_element001,P_element002,S_element004,Ca_element003]
  conduct = 2
  density = 1
  expand = 3
  formula = G4_BONE_COMPACT_ICRU
  name = G4_BONE_COMPACT_ICRU
  specific = 4
FEATURE [App::DocumentObjectGroupPython] H_element016  label="H_element : 0.034"  # scripted group (container) (typed FeaturePython)
  n = 0.034
FEATURE [App::DocumentObjectGroupPython] C_element016  label="C_element : 0.155"  # scripted group (container) (typed FeaturePython)
  n = 0.155
FEATURE [App::DocumentObjectGroupPython] N_element011  label="N_element : 0.042"  # scripted group (container) (typed FeaturePython)
  n = 0.042
FEATURE [App::DocumentObjectGroupPython] O_element015  label="O_element : 0.435"  # scripted group (container) (typed FeaturePython)
  n = 0.435
FEATURE [App::DocumentObjectGroupPython] Na_element003  label="Na_element : 0.003"  # scripted group (container) (typed FeaturePython)
  n = 0.001
FEATURE [App::DocumentObjectGroupPython] Mg_element002  label="Mg_element : 0.003"  # scripted group (container) (typed FeaturePython)
  n = 0.002
FEATURE [App::DocumentObjectGroupPython] P_element003  label="P_element : 0.103"  # scripted group (container) (typed FeaturePython)
  n = 0.103
FEATURE [App::DocumentObjectGroupPython] S_element005  label="S_element : 0.004"  # scripted group (container) (typed FeaturePython)
  n = 0.003
FEATURE [App::DocumentObjectGroupPython] Ca_element004  label="Ca_element : 0.225"  # scripted group (container) (typed FeaturePython)
  n = 0.225
FEATURE [App::DocumentObjectGroupPython] G4_BONE_CORTICAL_ICRP  # scripted group (container) (typed FeaturePython)
  Dunit = g/cm3
  Dvalue = 1.92
  Group = -> [H_element016,C_element016,N_element011,O_element015,Na_element003,Mg_element002,P_element003,S_element005,Ca_element004]
  conduct = 2
  density = 1
  expand = 3
  formula = G4_BONE_CORTICAL_ICRP
  name = G4_BONE_CORTICAL_ICRP
  specific = 4
FEATURE [App::DocumentObjectGroupPython] B_element001  label="B_element : 4"  # scripted group (container) (typed FeaturePython)
  n = 4
  ref = B_element
FEATURE [App::DocumentObjectGroupPython] C_element017  label="C_element : 1"  # scripted group (container) (typed FeaturePython)
  n = 1
  ref = C_element
FEATURE [App::DocumentObjectGroupPython] G4_BORON_CARBIDE  # scripted group (container) (typed FeaturePython)
  Dunit = g/cm3
  Dvalue = 2.52
  Group = -> [B_element001,C_element017]
  conduct = 2
  density = 1
  expand = 3
  formula = G4_BORON_CARBIDE
  name = G4_BORON_CARBIDE
  specific = 4
FEATURE [App::DocumentObjectGroupPython] B_element002  label="B_element : 2"  # scripted group (container) (typed FeaturePython)
  n = 2
  ref = B_element
FEATURE [App::DocumentObjectGroupPython] O_element016  label="O_element : 006"  # scripted group (container) (typed FeaturePython)
  n = 3
  ref = O_element
FEATURE [App::DocumentObjectGroupPython] G4_BORON_OXIDE  # scripted group (container) (typed FeaturePython)
  Dunit = g/cm3
  Dvalue = 1.812
  Group = -> [B_element002,O_element016]
  conduct = 2
  density = 1
  expand = 3
  formula = G4_BORON_OXIDE
  name = G4_BORON_OXIDE
  specific = 4
FEATURE [App::DocumentObjectGroupPython] H_element017  label="H_element : 0.107"  # scripted group (container) (typed FeaturePython)
  n = 0.107
FEATURE [App::DocumentObjectGroupPython] C_element018  label="C_element : 0.145"  # scripted group (container) (typed FeaturePython)
  n = 0.145
FEATURE [App::DocumentObjectGroupPython] N_element012  label="N_element : 0.022"  # scripted group (container) (typed FeaturePython)
  n = 0.022
FEATURE [App::DocumentObjectGroupPython] O_element017  label="O_element : 0.712"  # scripted group (container) (typed FeaturePython)
  n = 0.712
FEATURE [App::DocumentObjectGroupPython] Na_element004  label="Na_element : 0.004"  # scripted group (container) (typed FeaturePython)
  n = 0.002
FEATURE [App::DocumentObjectGroupPython] P_element004  label="P_element : 0.004"  # scripted group (container) (typed FeaturePython)
  n = 0.004
FEATURE [App::DocumentObjectGroupPython] S_element006  label="S_element : 0.005"  # scripted group (container) (typed FeaturePython)
  n = 0.002
FEATURE [App::DocumentObjectGroupPython] Cl_element003  label="Cl_element : 0.004"  # scripted group (container) (typed FeaturePython)
  n = 0.003
FEATURE [App::DocumentObjectGroupPython] K_element002  label="K_element : 0.003"  # scripted group (container) (typed FeaturePython)
  n = 0.003
FEATURE [App::DocumentObjectGroupPython] G4_BRAIN_ICRP  # scripted group (container) (typed FeaturePython)
  Dunit = g/cm3
  Dvalue = 1.04
  Group = -> [H_element017,C_element018,N_element012,O_element017,Na_element004,P_element004,S_element006,Cl_element003,K_element002]
  conduct = 2
  density = 1
  expand = 3
  formula = G4_BRAIN_ICRP
  name = G4_BRAIN_ICRP
  specific = 4
FEATURE [App::DocumentObjectGroupPython] C_element019  label="C_element : 4"  # scripted group (container) (typed FeaturePython)
  n = 4
  ref = C_element
FEATURE [App::DocumentObjectGroupPython] H_element018  label="H_element : 010"  # scripted group (container) (typed FeaturePython)
  n = 10
  ref = H_element
FEATURE [App::DocumentObjectGroupPython] G4_BUTANE  # scripted group (container) (typed FeaturePython)
  Dunit = g/cm3
  Dvalue = 0.00249343
  Group = -> [C_element019,H_element018]
  conduct = 2
  density = 1
  expand = 3
  formula = G4_BUTANE
  name = G4_BUTANE
  specific = 4
FEATURE [App::DocumentObjectGroupPython] C_element020  label="C_element : 008"  # scripted group (container) (typed FeaturePython)
  n = 4
  ref = C_element
FEATURE [App::DocumentObjectGroupPython] H_element019  label="H_element : 011"  # scripted group (container) (typed FeaturePython)
  n = 10
  ref = H_element
FEATURE [App::DocumentObjectGroupPython] O_element018  label="O_element : 007"  # scripted group (container) (typed FeaturePython)
  n = 1
  ref = O_element
FEATURE [App::DocumentObjectGroupPython] G4_N_BUTYL_ALCOHOL  label="G4_N-BUTYL_ALCOHOL"  # scripted group (container) (typed FeaturePython)
  Dunit = g/cm3
  Dvalue = 0.8098
  Group = -> [C_element020,H_element019,O_element018]
  conduct = 2
  density = 1
  expand = 3
  formula = G4_N-BUTYL_ALCOHOL
  name = G4_N-BUTYL_ALCOHOL
  specific = 4
FEATURE [App::DocumentObjectGroupPython] H_element020  label="H_element : 0.025"  # scripted group (container) (typed FeaturePython)
  n = 0.02468
FEATURE [App::DocumentObjectGroupPython] C_element021  label="C_element : 0.502"  # scripted group (container) (typed FeaturePython)
  n = 0.501611
FEATURE [App::DocumentObjectGroupPython] O_element019  label="O_element : 0.005"  # scripted group (container) (typed FeaturePython)
  n = 0.004527
FEATURE [App::DocumentObjectGroupPython] F_element004  label="F_element : 0.465"  # scripted group (container) (typed FeaturePython)
  n = 0.465209
FEATURE [App::DocumentObjectGroupPython] Si_element001  label="Si_element : 0.004"  # scripted group (container) (typed FeaturePython)
  n = 0.003973
FEATURE [App::DocumentObjectGroupPython] G4_C_552  label="G4_C-552"  # scripted group (container) (typed FeaturePython)
  Dunit = g/cm3
  Dvalue = 1.76
  Group = -> [H_element020,C_element021,O_element019,F_element004,Si_element001]
  conduct = 2
  density = 1
  expand = 3
  formula = G4_C-552
  name = G4_C-552
  specific = 4
FEATURE [App::DocumentObjectGroupPython] Cd_element001  label="Cd_element : 1"  # scripted group (container) (typed FeaturePython)
  n = 1
  ref = Cd_element
FEATURE [App::DocumentObjectGroupPython] Te_element001  label="Te_element : 1"  # scripted group (container) (typed FeaturePython)
  n = 1
  ref = Te_element
FEATURE [App::DocumentObjectGroupPython] G4_CADMIUM_TELLURIDE  # scripted group (container) (typed FeaturePython)
  Dunit = g/cm3
  Dvalue = 6.2
  Group = -> [Cd_element001,Te_element001]
  conduct = 2
  density = 1
  expand = 3
  formula = G4_CADMIUM_TELLURIDE
  name = G4_CADMIUM_TELLURIDE
  specific = 4
FEATURE [App::DocumentObjectGroupPython] Cd_element002  label="Cd_element : 002"  # scripted group (container) (typed FeaturePython)
  n = 1
  ref = Cd_element
FEATURE [App::DocumentObjectGroupPython] W_element001  label="W_element : 1"  # scripted group (container) (typed FeaturePython)
  n = 1
  ref = W_element
FEATURE [App::DocumentObjectGroupPython] O_element020  label="O_element : 008"  # scripted group (container) (typed FeaturePython)
  n = 4
  ref = O_element
FEATURE [App::DocumentObjectGroupPython] G4_CADMIUM_TUNGSTATE  # scripted group (container) (typed FeaturePython)
  Dunit = g/cm3
  Dvalue = 7.9
  Group = -> [Cd_element002,W_element001,O_element020]
  conduct = 2
  density = 1
  expand = 3
  formula = G4_CADMIUM_TUNGSTATE
  name = G4_CADMIUM_TUNGSTATE
  specific = 4
FEATURE [App::DocumentObjectGroupPython] Ca_element005  label="Ca_element : 1"  # scripted group (container) (typed FeaturePython)
  n = 1
  ref = Ca_element
FEATURE [App::DocumentObjectGroupPython] C_element022  label="C_element : 009"  # scripted group (container) (typed FeaturePython)
  n = 1
  ref = C_element
FEATURE [App::DocumentObjectGroupPython] O_element021  label="O_element : 009"  # scripted group (container) (typed FeaturePython)
  n = 3
  ref = O_element
FEATURE [App::DocumentObjectGroupPython] G4_CALCIUM_CARBONATE  # scripted group (container) (typed FeaturePython)
  Dunit = g/cm3
  Dvalue = 2.8
  Group = -> [Ca_element005,C_element022,O_element021]
  conduct = 2
  density = 1
  expand = 3
  formula = G4_CALCIUM_CARBONATE
  name = G4_CALCIUM_CARBONATE
  specific = 4
FEATURE [App::DocumentObjectGroupPython] Ca_element006  label="Ca_element : 002"  # scripted group (container) (typed FeaturePython)
  n = 1
  ref = Ca_element
FEATURE [App::DocumentObjectGroupPython] F_element005  label="F_element : 003"  # scripted group (container) (typed FeaturePython)
  n = 2
  ref = F_element
FEATURE [App::DocumentObjectGroupPython] G4_CALCIUM_FLUORIDE  # scripted group (container) (typed FeaturePython)
  Dunit = g/cm3
  Dvalue = 3.18
  Group = -> [Ca_element006,F_element005]
  conduct = 2
  density = 1
  expand = 3
  formula = G4_CALCIUM_FLUORIDE
  name = G4_CALCIUM_FLUORIDE
  specific = 4
FEATURE [App::DocumentObjectGroupPython] Ca_element007  label="Ca_element : 003"  # scripted group (container) (typed FeaturePython)
  n = 1
  ref = Ca_element
FEATURE [App::DocumentObjectGroupPython] O_element022  label="O_element : 010"  # scripted group (container) (typed FeaturePython)
  n = 1
  ref = O_element
FEATURE [App::DocumentObjectGroupPython] G4_CALCIUM_OXIDE  # scripted group (container) (typed FeaturePython)
  Dunit = g/cm3
  Dvalue = 3.3
  Group = -> [Ca_element007,O_element022]
  conduct = 2
  density = 1
  expand = 3
  formula = G4_CALCIUM_OXIDE
  name = G4_CALCIUM_OXIDE
  specific = 4
FEATURE [App::DocumentObjectGroupPython] Ca_element008  label="Ca_element : 004"  # scripted group (container) (typed FeaturePython)
  n = 1
  ref = Ca_element
FEATURE [App::DocumentObjectGroupPython] S_element007  label="S_element : 002"  # scripted group (container) (typed FeaturePython)
  n = 1
  ref = S_element
FEATURE [App::DocumentObjectGroupPython] O_element023  label="O_element : 011"  # scripted group (container) (typed FeaturePython)
  n = 4
  ref = O_element
FEATURE [App::DocumentObjectGroupPython] G4_CALCIUM_SULFATE  # scripted group (container) (typed FeaturePython)
  Dunit = g/cm3
  Dvalue = 2.96
  Group = -> [Ca_element008,S_element007,O_element023]
  conduct = 2
  density = 1
  expand = 3
  formula = G4_CALCIUM_SULFATE
  name = G4_CALCIUM_SULFATE
  specific = 4
FEATURE [App::DocumentObjectGroupPython] Ca_element009  label="Ca_element : 005"  # scripted group (container) (typed FeaturePython)
  n = 1
  ref = Ca_element
FEATURE [App::DocumentObjectGroupPython] W_element002  label="W_element : 002"  # scripted group (container) (typed FeaturePython)
  n = 1
  ref = W_element
FEATURE [App::DocumentObjectGroupPython] O_element024  label="O_element : 012"  # scripted group (container) (typed FeaturePython)
  n = 4
  ref = O_element
FEATURE [App::DocumentObjectGroupPython] G4_CALCIUM_TUNGSTATE  # scripted group (container) (typed FeaturePython)
  Dunit = g/cm3
  Dvalue = 6.062
  Group = -> [Ca_element009,W_element002,O_element024]
  conduct = 2
  density = 1
  expand = 3
  formula = G4_CALCIUM_TUNGSTATE
  name = G4_CALCIUM_TUNGSTATE
  specific = 4
FEATURE [App::DocumentObjectGroupPython] C_element023  label="C_element : 010"  # scripted group (container) (typed FeaturePython)
  n = 1
  ref = C_element
FEATURE [App::DocumentObjectGroupPython] O_element025  label="O_element : 013"  # scripted group (container) (typed FeaturePython)
  n = 2
  ref = O_element
FEATURE [App::DocumentObjectGroupPython] G4_CARBON_DIOXIDE  # scripted group (container) (typed FeaturePython)
  Dunit = g/cm3
  Dvalue = 0.00184212
  Group = -> [C_element023,O_element025]
  conduct = 2
  density = 1
  expand = 3
  formula = G4_CARBON_DIOXIDE
  name = G4_CARBON_DIOXIDE
  specific = 4
FEATURE [App::DocumentObjectGroupPython] C_element024  label="C_element : 011"  # scripted group (container) (typed FeaturePython)
  n = 1
  ref = C_element
FEATURE [App::DocumentObjectGroupPython] Cl_element004  label="Cl_element : 4"  # scripted group (container) (typed FeaturePython)
  n = 4
  ref = Cl_element
FEATURE [App::DocumentObjectGroupPython] G4_CARBON_TETRACHLORIDE  # scripted group (container) (typed FeaturePython)
  Dunit = g/cm3
  Dvalue = 1.594
  Group = -> [C_element024,Cl_element004]
  conduct = 2
  density = 1
  expand = 3
  formula = G4_CARBON_TETRACHLORIDE
  name = G4_CARBON_TETRACHLORIDE
  specific = 4
FEATURE [App::DocumentObjectGroupPython] C_element025  label="C_element : 012"  # scripted group (container) (typed FeaturePython)
  n = 6
  ref = C_element
FEATURE [App::DocumentObjectGroupPython] H_element021  label="H_element : 012"  # scripted group (container) (typed FeaturePython)
  n = 10
  ref = H_element
FEATURE [App::DocumentObjectGroupPython] O_element026  label="O_element : 5"  # scripted group (container) (typed FeaturePython)
  n = 5
  ref = O_element
FEATURE [App::DocumentObjectGroupPython] G4_CELLULOSE_CELLOPHANE  # scripted group (container) (typed FeaturePython)
  Dunit = g/cm3
  Dvalue = 1.42
  Group = -> [C_element025,H_element021,O_element026]
  conduct = 2
  density = 1
  expand = 3
  formula = G4_CELLULOSE_CELLOPHANE
  name = G4_CELLULOSE_CELLOPHANE
  specific = 4
FEATURE [App::DocumentObjectGroupPython] H_element022  label="H_element : 0.067"  # scripted group (container) (typed FeaturePython)
  n = 0.067125
FEATURE [App::DocumentObjectGroupPython] C_element026  label="C_element : 0.545"  # scripted group (container) (typed FeaturePython)
  n = 0.545403
FEATURE [App::DocumentObjectGroupPython] O_element027  label="O_element : 0.387"  # scripted group (container) (typed FeaturePython)
  n = 0.387472
FEATURE [App::DocumentObjectGroupPython] G4_CELLULOSE_BUTYRATE  # scripted group (container) (typed FeaturePython)
  Dunit = g/cm3
  Dvalue = 1.2
  Group = -> [H_element022,C_element026,O_element027]
  conduct = 2
  density = 1
  expand = 3
  formula = G4_CELLULOSE_BUTYRATE
  name = G4_CELLULOSE_BUTYRATE
  specific = 4
FEATURE [App::DocumentObjectGroupPython] H_element023  label="H_element : 0.029"  # scripted group (container) (typed FeaturePython)
  n = 0.029216
FEATURE [App::DocumentObjectGroupPython] C_element027  label="C_element : 0.271"  # scripted group (container) (typed FeaturePython)
  n = 0.271296
FEATURE [App::DocumentObjectGroupPython] N_element013  label="N_element : 0.121"  # scripted group (container) (typed FeaturePython)
  n = 0.121276
FEATURE [App::DocumentObjectGroupPython] O_element028  label="O_element : 0.578"  # scripted group (container) (typed FeaturePython)
  n = 0.578212
FEATURE [App::DocumentObjectGroupPython] G4_CELLULOSE_NITRATE  # scripted group (container) (typed FeaturePython)
  Dunit = g/cm3
  Dvalue = 1.49
  Group = -> [H_element023,C_element027,N_element013,O_element028]
  conduct = 2
  density = 1
  expand = 3
  formula = G4_CELLULOSE_NITRATE
  name = G4_CELLULOSE_NITRATE
  specific = 4
FEATURE [App::DocumentObjectGroupPython] H_element024  label="H_element : 0.108"  # scripted group (container) (typed FeaturePython)
  n = 0.107596
FEATURE [App::DocumentObjectGroupPython] N_element014  label="N_element : 0.001"  # scripted group (container) (typed FeaturePython)
  n = 0.0008
FEATURE [App::DocumentObjectGroupPython] O_element029  label="O_element : 0.875"  # scripted group (container) (typed FeaturePython)
  n = 0.874976
FEATURE [App::DocumentObjectGroupPython] S_element008  label="S_element : 0.015"  # scripted group (container) (typed FeaturePython)
  n = 0.014627
FEATURE [App::DocumentObjectGroupPython] Ce_element001  label="Ce_element : 0.002"  # scripted group (container) (typed FeaturePython)
  n = 0.002001
FEATURE [App::DocumentObjectGroupPython] G4_CERIC_SULFATE  # scripted group (container) (typed FeaturePython)
  Dunit = g/cm3
  Dvalue = 1.03
  Group = -> [H_element024,N_element014,O_element029,S_element008,Ce_element001]
  conduct = 2
  density = 1
  expand = 3
  formula = G4_CERIC_SULFATE
  name = G4_CERIC_SULFATE
  specific = 4
FEATURE [App::DocumentObjectGroupPython] Cs_element001  label="Cs_element : 1"  # scripted group (container) (typed FeaturePython)
  n = 1
  ref = Cs_element
FEATURE [App::DocumentObjectGroupPython] F_element006  label="F_element : 1"  # scripted group (container) (typed FeaturePython)
  n = 1
  ref = F_element
FEATURE [App::DocumentObjectGroupPython] G4_CESIUM_FLUORIDE  # scripted group (container) (typed FeaturePython)
  Dunit = g/cm3
  Dvalue = 4.115
  Group = -> [Cs_element001,F_element006]
  conduct = 2
  density = 1
  expand = 3
  formula = G4_CESIUM_FLUORIDE
  name = G4_CESIUM_FLUORIDE
  specific = 4
FEATURE [App::DocumentObjectGroupPython] Cs_element002  label="Cs_element : 002"  # scripted group (container) (typed FeaturePython)
  n = 1
  ref = Cs_element
FEATURE [App::DocumentObjectGroupPython] I_element001  label="I_element : 1"  # scripted group (container) (typed FeaturePython)
  n = 1
  ref = I_element
FEATURE [App::DocumentObjectGroupPython] G4_CESIUM_IODIDE  # scripted group (container) (typed FeaturePython)
  Dunit = g/cm3
  Dvalue = 4.51
  Group = -> [Cs_element002,I_element001]
  conduct = 2
  density = 1
  expand = 3
  formula = G4_CESIUM_IODIDE
  name = G4_CESIUM_IODIDE
  specific = 4
FEATURE [App::DocumentObjectGroupPython] C_element028  label="C_element : 013"  # scripted group (container) (typed FeaturePython)
  n = 6
  ref = C_element
FEATURE [App::DocumentObjectGroupPython] H_element025  label="H_element : 013"  # scripted group (container) (typed FeaturePython)
  n = 5
  ref = H_element
FEATURE [App::DocumentObjectGroupPython] Cl_element005  label="Cl_element : 1"  # scripted group (container) (typed FeaturePython)
  n = 1
  ref = Cl_element
FEATURE [App::DocumentObjectGroupPython] G4_CHLOROBENZENE  # scripted group (container) (typed FeaturePython)
  Dunit = g/cm3
  Dvalue = 1.1058
  Group = -> [C_element028,H_element025,Cl_element005]
  conduct = 2
  density = 1
  expand = 3
  formula = G4_CHLOROBENZENE
  name = G4_CHLOROBENZENE
  specific = 4
FEATURE [App::DocumentObjectGroupPython] C_element029  label="C_element : 014"  # scripted group (container) (typed FeaturePython)
  n = 1
  ref = C_element
FEATURE [App::DocumentObjectGroupPython] H_element026  label="H_element : 1"  # scripted group (container) (typed FeaturePython)
  n = 1
  ref = H_element
FEATURE [App::DocumentObjectGroupPython] Cl_element006  label="Cl_element : 3"  # scripted group (container) (typed FeaturePython)
  n = 3
  ref = Cl_element
FEATURE [App::DocumentObjectGroupPython] G4_CHLOROFORM  # scripted group (container) (typed FeaturePython)
  Dunit = g/cm3
  Dvalue = 1.4832
  Group = -> [C_element029,H_element026,Cl_element006]
  conduct = 2
  density = 1
  expand = 3
  formula = G4_CHLOROFORM
  name = G4_CHLOROFORM
  specific = 4
FEATURE [App::DocumentObjectGroupPython] H_element027  label="H_element : 0.010"  # scripted group (container) (typed FeaturePython)
  n = 0.01
FEATURE [App::DocumentObjectGroupPython] C_element030  label="C_element : 0.001"  # scripted group (container) (typed FeaturePython)
  n = 0.001
FEATURE [App::DocumentObjectGroupPython] O_element030  label="O_element : 0.529"  # scripted group (container) (typed FeaturePython)
  n = 0.529107
FEATURE [App::DocumentObjectGroupPython] Na_element005  label="Na_element : 0.016"  # scripted group (container) (typed FeaturePython)
  n = 0.016
FEATURE [App::DocumentObjectGroupPython] Mg_element003  label="Mg_element : 0.004"  # scripted group (container) (typed FeaturePython)
  n = 0.002
FEATURE [App::DocumentObjectGroupPython] Al_element002  label="Al_element : 0.034"  # scripted group (container) (typed FeaturePython)
  n = 0.033872
FEATURE [App::DocumentObjectGroupPython] Si_element002  label="Si_element : 0.337"  # scripted group (container) (typed FeaturePython)
  n = 0.337021
FEATURE [App::DocumentObjectGroupPython] K_element003  label="K_element : 0.013"  # scripted group (container) (typed FeaturePython)
  n = 0.013
FEATURE [App::DocumentObjectGroupPython] Ca_element010  label="Ca_element : 0.044"  # scripted group (container) (typed FeaturePython)
  n = 0.044
FEATURE [App::DocumentObjectGroupPython] Fe_element002  label="Fe_element : 0.014"  # scripted group (container) (typed FeaturePython)
  n = 0.014
FEATURE [App::DocumentObjectGroupPython] G4_CONCRETE  # scripted group (container) (typed FeaturePython)
  Dunit = g/cm3
  Dvalue = 2.3
  Group = -> [H_element027,C_element030,O_element030,Na_element005,Mg_element003,Al_element002,Si_element002,K_element003,Ca_element010,Fe_element002]
  conduct = 2
  density = 1
  expand = 3
  formula = G4_CONCRETE
  name = G4_CONCRETE
  specific = 4
FEATURE [App::DocumentObjectGroupPython] C_element031  label="C_element : 015"  # scripted group (container) (typed FeaturePython)
  n = 6
  ref = C_element
FEATURE [App::DocumentObjectGroupPython] H_element028  label="H_element : 12"  # scripted group (container) (typed FeaturePython)
  n = 12
  ref = H_element
FEATURE [App::DocumentObjectGroupPython] G4_CYCLOHEXANE  # scripted group (container) (typed FeaturePython)
  Dunit = g/cm3
  Dvalue = 0.779
  Group = -> [C_element031,H_element028]
  conduct = 2
  density = 1
  expand = 3
  formula = G4_CYCLOHEXANE
  name = G4_CYCLOHEXANE
  specific = 4
FEATURE [App::DocumentObjectGroupPython] C_element032  label="C_element : 016"  # scripted group (container) (typed FeaturePython)
  n = 6
  ref = C_element
FEATURE [App::DocumentObjectGroupPython] H_element029  label="H_element : 4"  # scripted group (container) (typed FeaturePython)
  n = 4
  ref = H_element
FEATURE [App::DocumentObjectGroupPython] Cl_element007  label="Cl_element : 2"  # scripted group (container) (typed FeaturePython)
  n = 2
  ref = Cl_element
FEATURE [App::DocumentObjectGroupPython] G4_1_2_DICHLOROBENZENE  label="G4_1.2-DICHLOROBENZENE"  # scripted group (container) (typed FeaturePython)
  Dunit = g/cm3
  Dvalue = 1.3048
  Group = -> [C_element032,H_element029,Cl_element007]
  conduct = 2
  density = 1
  expand = 3
  formula = G4_1.2-DICHLOROBENZENE
  name = G4_1.2-DICHLOROBENZENE
  specific = 4
FEATURE [App::DocumentObjectGroupPython] C_element033  label="C_element : 017"  # scripted group (container) (typed FeaturePython)
  n = 4
  ref = C_element
FEATURE [App::DocumentObjectGroupPython] H_element030  label="H_element : 8"  # scripted group (container) (typed FeaturePython)
  n = 8
  ref = H_element
FEATURE [App::DocumentObjectGroupPython] O_element031  label="O_element : 014"  # scripted group (container) (typed FeaturePython)
  n = 1
  ref = O_element
FEATURE [App::DocumentObjectGroupPython] Cl_element008  label="Cl_element : 005"  # scripted group (container) (typed FeaturePython)
  n = 2
  ref = Cl_element
FEATURE [App::DocumentObjectGroupPython] G4_DICHLORODIETHYL_ETHER  # scripted group (container) (typed FeaturePython)
  Dunit = g/cm3
  Dvalue = 1.2199
  Group = -> [C_element033,H_element030,O_element031,Cl_element008]
  conduct = 2
  density = 1
  expand = 3
  formula = G4_DICHLORODIETHYL_ETHER
  name = G4_DICHLORODIETHYL_ETHER
  specific = 4
FEATURE [App::DocumentObjectGroupPython] C_element034  label="C_element : 018"  # scripted group (container) (typed FeaturePython)
  n = 2
  ref = C_element
FEATURE [App::DocumentObjectGroupPython] H_element031  label="H_element : 014"  # scripted group (container) (typed FeaturePython)
  n = 4
  ref = H_element
FEATURE [App::DocumentObjectGroupPython] Cl_element009  label="Cl_element : 006"  # scripted group (container) (typed FeaturePython)
  n = 2
  ref = Cl_element
FEATURE [App::DocumentObjectGroupPython] G4_1_2_DICHLOROETHANE  label="G4_1.2-DICHLOROETHANE"  # scripted group (container) (typed FeaturePython)
  Dunit = g/cm3
  Dvalue = 1.2351
  Group = -> [C_element034,H_element031,Cl_element009]
  conduct = 2
  density = 1
  expand = 3
  formula = G4_1.2-DICHLOROETHANE
  name = G4_1.2-DICHLOROETHANE
  specific = 4
FEATURE [App::DocumentObjectGroupPython] C_element035  label="C_element : 019"  # scripted group (container) (typed FeaturePython)
  n = 4
  ref = C_element
FEATURE [App::DocumentObjectGroupPython] H_element032  label="H_element : 015"  # scripted group (container) (typed FeaturePython)
  n = 10
  ref = H_element
FEATURE [App::DocumentObjectGroupPython] O_element032  label="O_element : 015"  # scripted group (container) (typed FeaturePython)
  n = 1
  ref = O_element
FEATURE [App::DocumentObjectGroupPython] G4_DIETHYL_ETHER  # scripted group (container) (typed FeaturePython)
  Dunit = g/cm3
  Dvalue = 0.71378
  Group = -> [C_element035,H_element032,O_element032]
  conduct = 2
  density = 1
  expand = 3
  formula = G4_DIETHYL_ETHER
  name = G4_DIETHYL_ETHER
  specific = 4
FEATURE [App::DocumentObjectGroupPython] C_element036  label="C_element : 020"  # scripted group (container) (typed FeaturePython)
  n = 3
  ref = C_element
FEATURE [App::DocumentObjectGroupPython] H_element033  label="H_element : 016"  # scripted group (container) (typed FeaturePython)
  n = 7
  ref = H_element
FEATURE [App::DocumentObjectGroupPython] N_element015  label="N_element : 008"  # scripted group (container) (typed FeaturePython)
  n = 1
  ref = N_element
FEATURE [App::DocumentObjectGroupPython] O_element033  label="O_element : 016"  # scripted group (container) (typed FeaturePython)
  n = 1
  ref = O_element
FEATURE [App::DocumentObjectGroupPython] G4_N_N_DIMETHYL_FORMAMIDE  label="G4_N.N-DIMETHYL_FORMAMIDE"  # scripted group (container) (typed FeaturePython)
  Dunit = g/cm3
  Dvalue = 0.9487
  Group = -> [C_element036,H_element033,N_element015,O_element033]
  conduct = 2
  density = 1
  expand = 3
  formula = G4_N.N-DIMETHYL_FORMAMIDE
  name = G4_N.N-DIMETHYL_FORMAMIDE
  specific = 4
FEATURE [App::DocumentObjectGroupPython] C_element037  label="C_element : 021"  # scripted group (container) (typed FeaturePython)
  n = 2
  ref = C_element
FEATURE [App::DocumentObjectGroupPython] H_element034  label="H_element : 017"  # scripted group (container) (typed FeaturePython)
  n = 6
  ref = H_element
FEATURE [App::DocumentObjectGroupPython] O_element034  label="O_element : 017"  # scripted group (container) (typed FeaturePython)
  n = 1
  ref = O_element
FEATURE [App::DocumentObjectGroupPython] S_element009  label="S_element : 003"  # scripted group (container) (typed FeaturePython)
  n = 1
  ref = S_element
FEATURE [App::DocumentObjectGroupPython] G4_DIMETHYL_SULFOXIDE  # scripted group (container) (typed FeaturePython)
  Dunit = g/cm3
  Dvalue = 1.1014
  Group = -> [C_element037,H_element034,O_element034,S_element009]
  conduct = 2
  density = 1
  expand = 3
  formula = G4_DIMETHYL_SULFOXIDE
  name = G4_DIMETHYL_SULFOXIDE
  specific = 4
FEATURE [App::DocumentObjectGroupPython] C_element038  label="C_element : 022"  # scripted group (container) (typed FeaturePython)
  n = 2
  ref = C_element
FEATURE [App::DocumentObjectGroupPython] H_element035  label="H_element : 018"  # scripted group (container) (typed FeaturePython)
  n = 6
  ref = H_element
FEATURE [App::DocumentObjectGroupPython] G4_ETHANE  # scripted group (container) (typed FeaturePython)
  Dunit = g/cm3
  Dvalue = 0.00125324
  Group = -> [C_element038,H_element035]
  conduct = 2
  density = 1
  expand = 3
  formula = G4_ETHANE
  name = G4_ETHANE
  specific = 4
FEATURE [App::DocumentObjectGroupPython] C_element039  label="C_element : 023"  # scripted group (container) (typed FeaturePython)
  n = 2
  ref = C_element
FEATURE [App::DocumentObjectGroupPython] H_element036  label="H_element : 019"  # scripted group (container) (typed FeaturePython)
  n = 6
  ref = H_element
FEATURE [App::DocumentObjectGroupPython] O_element035  label="O_element : 018"  # scripted group (container) (typed FeaturePython)
  n = 1
  ref = O_element
FEATURE [App::DocumentObjectGroupPython] G4_ETHYL_ALCOHOL  # scripted group (container) (typed FeaturePython)
  Dunit = g/cm3
  Dvalue = 0.7893
  Group = -> [C_element039,H_element036,O_element035]
  conduct = 2
  density = 1
  expand = 3
  formula = G4_ETHYL_ALCOHOL
  name = G4_ETHYL_ALCOHOL
  specific = 4
FEATURE [App::DocumentObjectGroupPython] H_element037  label="H_element : 0.090"  # scripted group (container) (typed FeaturePython)
  n = 0.090027
FEATURE [App::DocumentObjectGroupPython] C_element040  label="C_element : 0.585"  # scripted group (container) (typed FeaturePython)
  n = 0.585182
FEATURE [App::DocumentObjectGroupPython] O_element036  label="O_element : 0.325"  # scripted group (container) (typed FeaturePython)
  n = 0.324791
FEATURE [App::DocumentObjectGroupPython] G4_ETHYL_CELLULOSE  # scripted group (container) (typed FeaturePython)
  Dunit = g/cm3
  Dvalue = 1.13
  Group = -> [H_element037,C_element040,O_element036]
  conduct = 2
  density = 1
  expand = 3
  formula = G4_ETHYL_CELLULOSE
  name = G4_ETHYL_CELLULOSE
  specific = 4
FEATURE [App::DocumentObjectGroupPython] C_element041  label="C_element : 024"  # scripted group (container) (typed FeaturePython)
  n = 2
  ref = C_element
FEATURE [App::DocumentObjectGroupPython] H_element038  label="H_element : 020"  # scripted group (container) (typed FeaturePython)
  n = 4
  ref = H_element
FEATURE [App::DocumentObjectGroupPython] G4_ETHYLENE  # scripted group (container) (typed FeaturePython)
  Dunit = g/cm3
  Dvalue = 0.00117497
  Group = -> [C_element041,H_element038]
  conduct = 2
  density = 1
  expand = 3
  formula = G4_ETHYLENE
  name = G4_ETHYLENE
  specific = 4
FEATURE [App::DocumentObjectGroupPython] H_element039  label="H_element : 0.096"  # scripted group (container) (typed FeaturePython)
  n = 0.096
FEATURE [App::DocumentObjectGroupPython] C_element042  label="C_element : 0.195"  # scripted group (container) (typed FeaturePython)
  n = 0.195
FEATURE [App::DocumentObjectGroupPython] N_element016  label="N_element : 0.057"  # scripted group (container) (typed FeaturePython)
  n = 0.057
FEATURE [App::DocumentObjectGroupPython] O_element037  label="O_element : 0.646"  # scripted group (container) (typed FeaturePython)
  n = 0.646
FEATURE [App::DocumentObjectGroupPython] Na_element006  label="Na_element : 0.017"  # scripted group (container) (typed FeaturePython)
  n = 0.001
FEATURE [App::DocumentObjectGroupPython] P_element005  label="P_element : 0.104"  # scripted group (container) (typed FeaturePython)
  n = 0.001
FEATURE [App::DocumentObjectGroupPython] S_element010  label="S_element : 0.016"  # scripted group (container) (typed FeaturePython)
  n = 0.003
FEATURE [App::DocumentObjectGroupPython] Cl_element010  label="Cl_element : 0.005"  # scripted group (container) (typed FeaturePython)
  n = 0.001
FEATURE [App::DocumentObjectGroupPython] G4_EYE_LENS_ICRP  # scripted group (container) (typed FeaturePython)
  Dunit = g/cm3
  Dvalue = 1.07
  Group = -> [H_element039,C_element042,N_element016,O_element037,Na_element006,P_element005,S_element010,Cl_element010]
  conduct = 2
  density = 1
  expand = 3
  formula = G4_EYE_LENS_ICRP
  name = G4_EYE_LENS_ICRP
  specific = 4
FEATURE [App::DocumentObjectGroupPython] Fe_element003  label="Fe_element : 2"  # scripted group (container) (typed FeaturePython)
  n = 2
  ref = Fe_element
FEATURE [App::DocumentObjectGroupPython] O_element038  label="O_element : 019"  # scripted group (container) (typed FeaturePython)
  n = 3
  ref = O_element
FEATURE [App::DocumentObjectGroupPython] G4_FERRIC_OXIDE  # scripted group (container) (typed FeaturePython)
  Dunit = g/cm3
  Dvalue = 5.2
  Group = -> [Fe_element003,O_element038]
  conduct = 2
  density = 1
  expand = 3
  formula = G4_FERRIC_OXIDE
  name = G4_FERRIC_OXIDE
  specific = 4
FEATURE [App::DocumentObjectGroupPython] Fe_element004  label="Fe_element : 1"  # scripted group (container) (typed FeaturePython)
  n = 1
  ref = Fe_element
FEATURE [App::DocumentObjectGroupPython] B_element003  label="B_element : 1"  # scripted group (container) (typed FeaturePython)
  n = 1
  ref = B_element
FEATURE [App::DocumentObjectGroupPython] G4_FERROBORIDE  # scripted group (container) (typed FeaturePython)
  Dunit = g/cm3
  Dvalue = 7.15
  Group = -> [Fe_element004,B_element003]
  conduct = 2
  density = 1
  expand = 3
  formula = G4_FERROBORIDE
  name = G4_FERROBORIDE
  specific = 4
FEATURE [App::DocumentObjectGroupPython] Fe_element005  label="Fe_element : 003"  # scripted group (container) (typed FeaturePython)
  n = 1
  ref = Fe_element
FEATURE [App::DocumentObjectGroupPython] O_element039  label="O_element : 020"  # scripted group (container) (typed FeaturePython)
  n = 1
  ref = O_element
FEATURE [App::DocumentObjectGroupPython] G4_FERROUS_OXIDE  # scripted group (container) (typed FeaturePython)
  Dunit = g/cm3
  Dvalue = 5.7
  Group = -> [Fe_element005,O_element039]
  conduct = 2
  density = 1
  expand = 3
  formula = G4_FERROUS_OXIDE
  name = G4_FERROUS_OXIDE
  specific = 4
FEATURE [App::DocumentObjectGroupPython] H_element040  label="H_element : 0.115"  # scripted group (container) (typed FeaturePython)
  n = 0.108259
FEATURE [App::DocumentObjectGroupPython] N_element017  label="N_element : 0.000"  # scripted group (container) (typed FeaturePython)
  n = 2.7e-05
FEATURE [App::DocumentObjectGroupPython] O_element040  label="O_element : 0.879"  # scripted group (container) (typed FeaturePython)
  n = 0.878636
FEATURE [App::DocumentObjectGroupPython] Na_element007  label="Na_element : 0.000"  # scripted group (container) (typed FeaturePython)
  n = 2.2e-05
FEATURE [App::DocumentObjectGroupPython] S_element011  label="S_element : 0.013"  # scripted group (container) (typed FeaturePython)
  n = 0.012968
FEATURE [App::DocumentObjectGroupPython] Cl_element011  label="Cl_element : 0.000"  # scripted group (container) (typed FeaturePython)
  n = 3.4e-05
FEATURE [App::DocumentObjectGroupPython] Fe_element006  label="Fe_element : 0.000"  # scripted group (container) (typed FeaturePython)
  n = 5.4e-05
FEATURE [App::DocumentObjectGroupPython] G4_FERROUS_SULFATE  # scripted group (container) (typed FeaturePython)
  Dunit = g/cm3
  Dvalue = 1.024
  Group = -> [H_element040,N_element017,O_element040,Na_element007,S_element011,Cl_element011,Fe_element006]
  conduct = 2
  density = 1
  expand = 3
  formula = G4_FERROUS_SULFATE
  name = G4_FERROUS_SULFATE
  specific = 4
FEATURE [App::DocumentObjectGroupPython] C_element043  label="C_element : 0.099"  # scripted group (container) (typed FeaturePython)
  n = 0.099335
FEATURE [App::DocumentObjectGroupPython] F_element007  label="F_element : 0.314"  # scripted group (container) (typed FeaturePython)
  n = 0.314247
FEATURE [App::DocumentObjectGroupPython] Cl_element012  label="Cl_element : 0.586"  # scripted group (container) (typed FeaturePython)
  n = 0.586418
FEATURE [App::DocumentObjectGroupPython] G4_FREON_12  label="G4_FREON-12"  # scripted group (container) (typed FeaturePython)
  Dunit = g/cm3
  Dvalue = 1.12
  Group = -> [C_element043,F_element007,Cl_element012]
  conduct = 2
  density = 1
  expand = 3
  formula = G4_FREON-12
  name = G4_FREON-12
  specific = 4
FEATURE [App::DocumentObjectGroupPython] C_element044  label="C_element : 0.057"  # scripted group (container) (typed FeaturePython)
  n = 0.057245
FEATURE [App::DocumentObjectGroupPython] F_element008  label="F_element : 0.181"  # scripted group (container) (typed FeaturePython)
  n = 0.181096
FEATURE [App::DocumentObjectGroupPython] Br_element001  label="Br_element : 0.762"  # scripted group (container) (typed FeaturePython)
  n = 0.761659
FEATURE [App::DocumentObjectGroupPython] G4_FREON_12B2  label="G4_FREON-12B2"  # scripted group (container) (typed FeaturePython)
  Dunit = g/cm3
  Dvalue = 1.8
  Group = -> [C_element044,F_element008,Br_element001]
  conduct = 2
  density = 1
  expand = 3
  formula = G4_FREON-12B2
  name = G4_FREON-12B2
  specific = 4
FEATURE [App::DocumentObjectGroupPython] C_element045  label="C_element : 0.115"  # scripted group (container) (typed FeaturePython)
  n = 0.114983
FEATURE [App::DocumentObjectGroupPython] F_element009  label="F_element : 0.546"  # scripted group (container) (typed FeaturePython)
  n = 0.545621
FEATURE [App::DocumentObjectGroupPython] Cl_element013  label="Cl_element : 0.339"  # scripted group (container) (typed FeaturePython)
  n = 0.339396
FEATURE [App::DocumentObjectGroupPython] G4_FREON_13  label="G4_FREON-13"  # scripted group (container) (typed FeaturePython)
  Dunit = g/cm3
  Dvalue = 0.95
  Group = -> [C_element045,F_element009,Cl_element013]
  conduct = 2
  density = 1
  expand = 3
  formula = G4_FREON-13
  name = G4_FREON-13
  specific = 4
FEATURE [App::DocumentObjectGroupPython] C_element046  label="C_element : 025"  # scripted group (container) (typed FeaturePython)
  n = 1
  ref = C_element
FEATURE [App::DocumentObjectGroupPython] F_element010  label="F_element : 3"  # scripted group (container) (typed FeaturePython)
  n = 3
  ref = F_element
FEATURE [App::DocumentObjectGroupPython] Br_element002  label="Br_element : 1"  # scripted group (container) (typed FeaturePython)
  n = 1
  ref = Br_element
FEATURE [App::DocumentObjectGroupPython] G4_FREON_13B1  label="G4_FREON-13B1"  # scripted group (container) (typed FeaturePython)
  Dunit = g/cm3
  Dvalue = 1.5
  Group = -> [C_element046,F_element010,Br_element002]
  conduct = 2
  density = 1
  expand = 3
  formula = G4_FREON-13B1
  name = G4_FREON-13B1
  specific = 4
FEATURE [App::DocumentObjectGroupPython] C_element047  label="C_element : 0.061"  # scripted group (container) (typed FeaturePython)
  n = 0.061309
FEATURE [App::DocumentObjectGroupPython] F_element011  label="F_element : 0.291"  # scripted group (container) (typed FeaturePython)
  n = 0.290924
FEATURE [App::DocumentObjectGroupPython] I_element002  label="I_element : 0.648"  # scripted group (container) (typed FeaturePython)
  n = 0.647767
FEATURE [App::DocumentObjectGroupPython] G4_FREON_13I1  label="G4_FREON-13I1"  # scripted group (container) (typed FeaturePython)
  Dunit = g/cm3
  Dvalue = 1.8
  Group = -> [C_element047,F_element011,I_element002]
  conduct = 2
  density = 1
  expand = 3
  formula = G4_FREON-13I1
  name = G4_FREON-13I1
  specific = 4
FEATURE [App::DocumentObjectGroupPython] Gd_element001  label="Gd_element : 2"  # scripted group (container) (typed FeaturePython)
  n = 2
  ref = Gd_element
FEATURE [App::DocumentObjectGroupPython] O_element041  label="O_element : 021"  # scripted group (container) (typed FeaturePython)
  n = 2
  ref = O_element
FEATURE [App::DocumentObjectGroupPython] S_element012  label="S_element : 004"  # scripted group (container) (typed FeaturePython)
  n = 1
  ref = S_element
FEATURE [App::DocumentObjectGroupPython] G4_GADOLINIUM_OXYSULFIDE  # scripted group (container) (typed FeaturePython)
  Dunit = g/cm3
  Dvalue = 7.44
  Group = -> [Gd_element001,O_element041,S_element012]
  conduct = 2
  density = 1
  expand = 3
  formula = G4_GADOLINIUM_OXYSULFIDE
  name = G4_GADOLINIUM_OXYSULFIDE
  specific = 4
FEATURE [App::DocumentObjectGroupPython] Ga_element001  label="Ga_element : 1"  # scripted group (container) (typed FeaturePython)
  n = 1
  ref = Ga_element
FEATURE [App::DocumentObjectGroupPython] As_element001  label="As_element : 1"  # scripted group (container) (typed FeaturePython)
  n = 1
  ref = As_element
FEATURE [App::DocumentObjectGroupPython] G4_GALLIUM_ARSENIDE  # scripted group (container) (typed FeaturePython)
  Dunit = g/cm3
  Dvalue = 5.31
  Group = -> [Ga_element001,As_element001]
  conduct = 2
  density = 1
  expand = 3
  formula = G4_GALLIUM_ARSENIDE
  name = G4_GALLIUM_ARSENIDE
  specific = 4
FEATURE [App::DocumentObjectGroupPython] H_element041  label="H_element : 0.081"  # scripted group (container) (typed FeaturePython)
  n = 0.08118
FEATURE [App::DocumentObjectGroupPython] C_element048  label="C_element : 0.416"  # scripted group (container) (typed FeaturePython)
  n = 0.41606
FEATURE [App::DocumentObjectGroupPython] N_element018  label="N_element : 0.111"  # scripted group (container) (typed FeaturePython)
  n = 0.11124
FEATURE [App::DocumentObjectGroupPython] O_element042  label="O_element : 0.381"  # scripted group (container) (typed FeaturePython)
  n = 0.38064
FEATURE [App::DocumentObjectGroupPython] S_element013  label="S_element : 0.011"  # scripted group (container) (typed FeaturePython)
  n = 0.01088
FEATURE [App::DocumentObjectGroupPython] G4_GEL_PHOTO_EMULSION  # scripted group (container) (typed FeaturePython)
  Dunit = g/cm3
  Dvalue = 1.2914
  Group = -> [H_element041,C_element048,N_element018,O_element042,S_element013]
  conduct = 2
  density = 1
  expand = 3
  formula = G4_GEL_PHOTO_EMULSION
  name = G4_GEL_PHOTO_EMULSION
  specific = 4
FEATURE [App::DocumentObjectGroupPython] B_element004  label="B_element : 0.040"  # scripted group (container) (typed FeaturePython)
  n = 0.0400639
FEATURE [App::DocumentObjectGroupPython] O_element043  label="O_element : 0.540"  # scripted group (container) (typed FeaturePython)
  n = 0.539561
FEATURE [App::DocumentObjectGroupPython] Na_element008  label="Na_element : 0.028"  # scripted group (container) (typed FeaturePython)
  n = 0.0281909
FEATURE [App::DocumentObjectGroupPython] Al_element003  label="Al_element : 0.012"  # scripted group (container) (typed FeaturePython)
  n = 0.011644
FEATURE [App::DocumentObjectGroupPython] Si_element003  label="Si_element : 0.377"  # scripted group (container) (typed FeaturePython)
  n = 0.377219
FEATURE [App::DocumentObjectGroupPython] K_element004  label="K_element : 0.014"  # scripted group (container) (typed FeaturePython)
  n = 0.00332099
FEATURE [App::DocumentObjectGroupPython] G4_Pyrex_Glass  # scripted group (container) (typed FeaturePython)
  Dunit = g/cm3
  Dvalue = 2.23
  Group = -> [B_element004,O_element043,Na_element008,Al_element003,Si_element003,K_element004]
  conduct = 2
  density = 1
  expand = 3
  formula = G4_Pyrex_Glass
  name = G4_Pyrex_Glass
  specific = 4
FEATURE [App::DocumentObjectGroupPython] O_element044  label="O_element : 0.156"  # scripted group (container) (typed FeaturePython)
  n = 0.156453
FEATURE [App::DocumentObjectGroupPython] Si_element004  label="Si_element : 0.081"  # scripted group (container) (typed FeaturePython)
  n = 0.080866
FEATURE [App::DocumentObjectGroupPython] Ti_element001  label="Ti_element : 0.008"  # scripted group (container) (typed FeaturePython)
  n = 0.008092
FEATURE [App::DocumentObjectGroupPython] As_element002  label="As_element : 0.003"  # scripted group (container) (typed FeaturePython)
  n = 0.002651
FEATURE [App::DocumentObjectGroupPython] Pb_element001  label="Pb_element : 0.752"  # scripted group (container) (typed FeaturePython)
  n = 0.751938
FEATURE [App::DocumentObjectGroupPython] G4_GLASS_LEAD  # scripted group (container) (typed FeaturePython)
  Dunit = g/cm3
  Dvalue = 6.22
  Group = -> [O_element044,Si_element004,Ti_element001,As_element002,Pb_element001]
  conduct = 2
  density = 1
  expand = 3
  formula = G4_GLASS_LEAD
  name = G4_GLASS_LEAD
  specific = 4
FEATURE [App::DocumentObjectGroupPython] O_element045  label="O_element : 0.460"  # scripted group (container) (typed FeaturePython)
  n = 0.4598
FEATURE [App::DocumentObjectGroupPython] Na_element009  label="Na_element : 0.096"  # scripted group (container) (typed FeaturePython)
  n = 0.0964411
FEATURE [App::DocumentObjectGroupPython] Si_element005  label="Si_element : 0.378"  # scripted group (container) (typed FeaturePython)
  n = 0.336553
FEATURE [App::DocumentObjectGroupPython] Ca_element011  label="Ca_element : 0.107"  # scripted group (container) (typed FeaturePython)
  n = 0.107205
FEATURE [App::DocumentObjectGroupPython] G4_GLASS_PLATE  # scripted group (container) (typed FeaturePython)
  Dunit = g/cm3
  Dvalue = 2.4
  Group = -> [O_element045,Na_element009,Si_element005,Ca_element011]
  conduct = 2
  density = 1
  expand = 3
  formula = G4_GLASS_PLATE
  name = G4_GLASS_PLATE
  specific = 4
FEATURE [App::DocumentObjectGroupPython] C_element049  label="C_element : 026"  # scripted group (container) (typed FeaturePython)
  n = 5
  ref = C_element
FEATURE [App::DocumentObjectGroupPython] H_element042  label="H_element : 021"  # scripted group (container) (typed FeaturePython)
  n = 10
  ref = H_element
FEATURE [App::DocumentObjectGroupPython] N_element019  label="N_element : 2"  # scripted group (container) (typed FeaturePython)
  n = 2
  ref = N_element
FEATURE [App::DocumentObjectGroupPython] O_element046  label="O_element : 022"  # scripted group (container) (typed FeaturePython)
  n = 3
  ref = O_element
FEATURE [App::DocumentObjectGroupPython] G4_GLUTAMINE  # scripted group (container) (typed FeaturePython)
  Dunit = g/cm3
  Dvalue = 1.46
  Group = -> [C_element049,H_element042,N_element019,O_element046]
  conduct = 2
  density = 1
  expand = 3
  formula = G4_GLUTAMINE
  name = G4_GLUTAMINE
  specific = 4
FEATURE [App::DocumentObjectGroupPython] C_element050  label="C_element : 027"  # scripted group (container) (typed FeaturePython)
  n = 3
  ref = C_element
FEATURE [App::DocumentObjectGroupPython] H_element043  label="H_element : 022"  # scripted group (container) (typed FeaturePython)
  n = 8
  ref = H_element
FEATURE [App::DocumentObjectGroupPython] O_element047  label="O_element : 023"  # scripted group (container) (typed FeaturePython)
  n = 3
  ref = O_element
FEATURE [App::DocumentObjectGroupPython] G4_GLYCEROL  # scripted group (container) (typed FeaturePython)
  Dunit = g/cm3
  Dvalue = 1.2613
  Group = -> [C_element050,H_element043,O_element047]
  conduct = 2
  density = 1
  expand = 3
  formula = G4_GLYCEROL
  name = G4_GLYCEROL
  specific = 4
FEATURE [App::DocumentObjectGroupPython] C_element051  label="C_element : 028"  # scripted group (container) (typed FeaturePython)
  n = 5
  ref = C_element
FEATURE [App::DocumentObjectGroupPython] H_element044  label="H_element : 023"  # scripted group (container) (typed FeaturePython)
  n = 5
  ref = H_element
FEATURE [App::DocumentObjectGroupPython] N_element020  label="N_element : 009"  # scripted group (container) (typed FeaturePython)
  n = 5
  ref = N_element
FEATURE [App::DocumentObjectGroupPython] O_element048  label="O_element : 024"  # scripted group (container) (typed FeaturePython)
  n = 1
  ref = O_element
FEATURE [App::DocumentObjectGroupPython] G4_GUANINE  # scripted group (container) (typed FeaturePython)
  Dunit = g/cm3
  Dvalue = 2.2
  Group = -> [C_element051,H_element044,N_element020,O_element048]
  conduct = 2
  density = 1
  expand = 3
  formula = G4_GUANINE
  name = G4_GUANINE
  specific = 4
FEATURE [App::DocumentObjectGroupPython] Ca_element012  label="Ca_element : 006"  # scripted group (container) (typed FeaturePython)
  n = 1
  ref = Ca_element
FEATURE [App::DocumentObjectGroupPython] S_element014  label="S_element : 005"  # scripted group (container) (typed FeaturePython)
  n = 1
  ref = S_element
FEATURE [App::DocumentObjectGroupPython] O_element049  label="O_element : 6"  # scripted group (container) (typed FeaturePython)
  n = 6
  ref = O_element
FEATURE [App::DocumentObjectGroupPython] H_element045  label="H_element : 024"  # scripted group (container) (typed FeaturePython)
  n = 4
  ref = H_element
FEATURE [App::DocumentObjectGroupPython] G4_GYPSUM  # scripted group (container) (typed FeaturePython)
  Dunit = g/cm3
  Dvalue = 2.32
  Group = -> [Ca_element012,S_element014,O_element049,H_element045]
  conduct = 2
  density = 1
  expand = 3
  formula = G4_GYPSUM
  name = G4_GYPSUM
  specific = 4
FEATURE [App::DocumentObjectGroupPython] C_element052  label="C_element : 7"  # scripted group (container) (typed FeaturePython)
  n = 7
  ref = C_element
FEATURE [App::DocumentObjectGroupPython] H_element046  label="H_element : 16"  # scripted group (container) (typed FeaturePython)
  n = 16
  ref = H_element
FEATURE [App::DocumentObjectGroupPython] G4_N_HEPTANE  label="G4_N-HEPTANE"  # scripted group (container) (typed FeaturePython)
  Dunit = g/cm3
  Dvalue = 0.68376
  Group = -> [C_element052,H_element046]
  conduct = 2
  density = 1
  expand = 3
  formula = G4_N-HEPTANE
  name = G4_N-HEPTANE
  specific = 4
FEATURE [App::DocumentObjectGroupPython] C_element053  label="C_element : 029"  # scripted group (container) (typed FeaturePython)
  n = 6
  ref = C_element
FEATURE [App::DocumentObjectGroupPython] H_element047  label="H_element : 14"  # scripted group (container) (typed FeaturePython)
  n = 14
  ref = H_element
FEATURE [App::DocumentObjectGroupPython] G4_N_HEXANE  label="G4_N-HEXANE"  # scripted group (container) (typed FeaturePython)
  Dunit = g/cm3
  Dvalue = 0.6603
  Group = -> [C_element053,H_element047]
  conduct = 2
  density = 1
  expand = 3
  formula = G4_N-HEXANE
  name = G4_N-HEXANE
  specific = 4
FEATURE [App::DocumentObjectGroupPython] C_element054  label="C_element : 22"  # scripted group (container) (typed FeaturePython)
  n = 22
  ref = C_element
FEATURE [App::DocumentObjectGroupPython] H_element048  label="H_element : 025"  # scripted group (container) (typed FeaturePython)
  n = 10
  ref = H_element
FEATURE [App::DocumentObjectGroupPython] N_element021  label="N_element : 010"  # scripted group (container) (typed FeaturePython)
  n = 2
  ref = N_element
FEATURE [App::DocumentObjectGroupPython] O_element050  label="O_element : 025"  # scripted group (container) (typed FeaturePython)
  n = 5
  ref = O_element
FEATURE [App::DocumentObjectGroupPython] G4_KAPTON  # scripted group (container) (typed FeaturePython)
  Dunit = g/cm3
  Dvalue = 1.42
  Group = -> [C_element054,H_element048,N_element021,O_element050]
  conduct = 2
  density = 1
  expand = 3
  formula = G4_KAPTON
  name = G4_KAPTON
  specific = 4
FEATURE [App::DocumentObjectGroupPython] La_element001  label="La_element : 1"  # scripted group (container) (typed FeaturePython)
  n = 1
  ref = La_element
FEATURE [App::DocumentObjectGroupPython] Br_element003  label="Br_element : 002"  # scripted group (container) (typed FeaturePython)
  n = 1
  ref = Br_element
FEATURE [App::DocumentObjectGroupPython] O_element051  label="O_element : 026"  # scripted group (container) (typed FeaturePython)
  n = 1
  ref = O_element
FEATURE [App::DocumentObjectGroupPython] G4_LANTHANUM_OXYBROMIDE  # scripted group (container) (typed FeaturePython)
  Dunit = g/cm3
  Dvalue = 6.28
  Group = -> [La_element001,Br_element003,O_element051]
  conduct = 2
  density = 1
  expand = 3
  formula = G4_LANTHANUM_OXYBROMIDE
  name = G4_LANTHANUM_OXYBROMIDE
  specific = 4
FEATURE [App::DocumentObjectGroupPython] La_element002  label="La_element : 2"  # scripted group (container) (typed FeaturePython)
  n = 2
  ref = La_element
FEATURE [App::DocumentObjectGroupPython] O_element052  label="O_element : 027"  # scripted group (container) (typed FeaturePython)
  n = 2
  ref = O_element
FEATURE [App::DocumentObjectGroupPython] S_element015  label="S_element : 006"  # scripted group (container) (typed FeaturePython)
  n = 1
  ref = S_element
FEATURE [App::DocumentObjectGroupPython] G4_LANTHANUM_OXYSULFIDE  # scripted group (container) (typed FeaturePython)
  Dunit = g/cm3
  Dvalue = 5.86
  Group = -> [La_element002,O_element052,S_element015]
  conduct = 2
  density = 1
  expand = 3
  formula = G4_LANTHANUM_OXYSULFIDE
  name = G4_LANTHANUM_OXYSULFIDE
  specific = 4
FEATURE [App::DocumentObjectGroupPython] O_element053  label="O_element : 0.072"  # scripted group (container) (typed FeaturePython)
  n = 0.071682
FEATURE [App::DocumentObjectGroupPython] Pb_element002  label="Pb_element : 0.928"  # scripted group (container) (typed FeaturePython)
  n = 0.928318
FEATURE [App::DocumentObjectGroupPython] G4_LEAD_OXIDE  # scripted group (container) (typed FeaturePython)
  Dunit = g/cm3
  Dvalue = 9.53
  Group = -> [O_element053,Pb_element002]
  conduct = 2
  density = 1
  expand = 3
  formula = G4_LEAD_OXIDE
  name = G4_LEAD_OXIDE
  specific = 4
FEATURE [App::DocumentObjectGroupPython] Li_element001  label="Li_element : 1"  # scripted group (container) (typed FeaturePython)
  n = 1
  ref = Li_element
FEATURE [App::DocumentObjectGroupPython] N_element022  label="N_element : 011"  # scripted group (container) (typed FeaturePython)
  n = 1
  ref = N_element
FEATURE [App::DocumentObjectGroupPython] H_element049  label="H_element : 026"  # scripted group (container) (typed FeaturePython)
  n = 2
  ref = H_element
FEATURE [App::DocumentObjectGroupPython] G4_LITHIUM_AMIDE  # scripted group (container) (typed FeaturePython)
  Dunit = g/cm3
  Dvalue = 1.178
  Group = -> [Li_element001,N_element022,H_element049]
  conduct = 2
  density = 1
  expand = 3
  formula = G4_LITHIUM_AMIDE
  name = G4_LITHIUM_AMIDE
  specific = 4
FEATURE [App::DocumentObjectGroupPython] Li_element002  label="Li_element : 2"  # scripted group (container) (typed FeaturePython)
  n = 2
  ref = Li_element
FEATURE [App::DocumentObjectGroupPython] C_element055  label="C_element : 030"  # scripted group (container) (typed FeaturePython)
  n = 1
  ref = C_element
FEATURE [App::DocumentObjectGroupPython] O_element054  label="O_element : 028"  # scripted group (container) (typed FeaturePython)
  n = 3
  ref = O_element
FEATURE [App::DocumentObjectGroupPython] G4_LITHIUM_CARBONATE  # scripted group (container) (typed FeaturePython)
  Dunit = g/cm3
  Dvalue = 2.11
  Group = -> [Li_element002,C_element055,O_element054]
  conduct = 2
  density = 1
  expand = 3
  formula = G4_LITHIUM_CARBONATE
  name = G4_LITHIUM_CARBONATE
  specific = 4
FEATURE [App::DocumentObjectGroupPython] Li_element003  label="Li_element : 003"  # scripted group (container) (typed FeaturePython)
  n = 1
  ref = Li_element
FEATURE [App::DocumentObjectGroupPython] F_element012  label="F_element : 004"  # scripted group (container) (typed FeaturePython)
  n = 1
  ref = F_element
FEATURE [App::DocumentObjectGroupPython] G4_LITHIUM_FLUORIDE  # scripted group (container) (typed FeaturePython)
  Dunit = g/cm3
  Dvalue = 2.635
  Group = -> [Li_element003,F_element012]
  conduct = 2
  density = 1
  expand = 3
  formula = G4_LITHIUM_FLUORIDE
  name = G4_LITHIUM_FLUORIDE
  specific = 4
FEATURE [App::DocumentObjectGroupPython] Li_element004  label="Li_element : 004"  # scripted group (container) (typed FeaturePython)
  n = 1
  ref = Li_element
FEATURE [App::DocumentObjectGroupPython] H_element050  label="H_element : 027"  # scripted group (container) (typed FeaturePython)
  n = 1
  ref = H_element
FEATURE [App::DocumentObjectGroupPython] G4_LITHIUM_HYDRIDE  # scripted group (container) (typed FeaturePython)
  Dunit = g/cm3
  Dvalue = 0.82
  Group = -> [Li_element004,H_element050]
  conduct = 2
  density = 1
  expand = 3
  formula = G4_LITHIUM_HYDRIDE
  name = G4_LITHIUM_HYDRIDE
  specific = 4
FEATURE [App::DocumentObjectGroupPython] Li_element005  label="Li_element : 005"  # scripted group (container) (typed FeaturePython)
  n = 1
  ref = Li_element
FEATURE [App::DocumentObjectGroupPython] I_element003  label="I_element : 002"  # scripted group (container) (typed FeaturePython)
  n = 1
  ref = I_element
FEATURE [App::DocumentObjectGroupPython] G4_LITHIUM_IODIDE  # scripted group (container) (typed FeaturePython)
  Dunit = g/cm3
  Dvalue = 3.494
  Group = -> [Li_element005,I_element003]
  conduct = 2
  density = 1
  expand = 3
  formula = G4_LITHIUM_IODIDE
  name = G4_LITHIUM_IODIDE
  specific = 4
FEATURE [App::DocumentObjectGroupPython] Li_element006  label="Li_element : 006"  # scripted group (container) (typed FeaturePython)
  n = 2
  ref = Li_element
FEATURE [App::DocumentObjectGroupPython] O_element055  label="O_element : 029"  # scripted group (container) (typed FeaturePython)
  n = 1
  ref = O_element
FEATURE [App::DocumentObjectGroupPython] G4_LITHIUM_OXIDE  # scripted group (container) (typed FeaturePython)
  Dunit = g/cm3
  Dvalue = 2.013
  Group = -> [Li_element006,O_element055]
  conduct = 2
  density = 1
  expand = 3
  formula = G4_LITHIUM_OXIDE
  name = G4_LITHIUM_OXIDE
  specific = 4
FEATURE [App::DocumentObjectGroupPython] Li_element007  label="Li_element : 007"  # scripted group (container) (typed FeaturePython)
  n = 2
  ref = Li_element
FEATURE [App::DocumentObjectGroupPython] B_element005  label="B_element : 005"  # scripted group (container) (typed FeaturePython)
  n = 4
  ref = B_element
FEATURE [App::DocumentObjectGroupPython] O_element056  label="O_element : 7"  # scripted group (container) (typed FeaturePython)
  n = 7
  ref = O_element
FEATURE [App::DocumentObjectGroupPython] G4_LITHIUM_TETRABORATE  # scripted group (container) (typed FeaturePython)
  Dunit = g/cm3
  Dvalue = 2.44
  Group = -> [Li_element007,B_element005,O_element056]
  conduct = 2
  density = 1
  expand = 3
  formula = G4_LITHIUM_TETRABORATE
  name = G4_LITHIUM_TETRABORATE
  specific = 4
FEATURE [App::DocumentObjectGroupPython] H_element051  label="H_element : 0.105"  # scripted group (container) (typed FeaturePython)
  n = 0.105
FEATURE [App::DocumentObjectGroupPython] C_element056  label="C_element : 0.083"  # scripted group (container) (typed FeaturePython)
  n = 0.083
FEATURE [App::DocumentObjectGroupPython] N_element023  label="N_element : 0.023"  # scripted group (container) (typed FeaturePython)
  n = 0.023
FEATURE [App::DocumentObjectGroupPython] O_element057  label="O_element : 0.779"  # scripted group (container) (typed FeaturePython)
  n = 0.779
FEATURE [App::DocumentObjectGroupPython] Na_element010  label="Na_element : 0.097"  # scripted group (container) (typed FeaturePython)
  n = 0.002
FEATURE [App::DocumentObjectGroupPython] P_element006  label="P_element : 0.105"  # scripted group (container) (typed FeaturePython)
  n = 0.001
FEATURE [App::DocumentObjectGroupPython] S_element016  label="S_element : 0.017"  # scripted group (container) (typed FeaturePython)
  n = 0.002
FEATURE [App::DocumentObjectGroupPython] Cl_element014  label="Cl_element : 0.587"  # scripted group (container) (typed FeaturePython)
  n = 0.003
FEATURE [App::DocumentObjectGroupPython] K_element005  label="K_element : 0.015"  # scripted group (container) (typed FeaturePython)
  n = 0.002
FEATURE [App::DocumentObjectGroupPython] G4_LUNG_ICRP  # scripted group (container) (typed FeaturePython)
  Dunit = g/cm3
  Dvalue = 1.04
  Group = -> [H_element051,C_element056,N_element023,O_element057,Na_element010,P_element006,S_element016,Cl_element014,K_element005]
  conduct = 2
  density = 1
  expand = 3
  formula = G4_LUNG_ICRP
  name = G4_LUNG_ICRP
  specific = 4
FEATURE [App::DocumentObjectGroupPython] H_element052  label="H_element : 0.116"  # scripted group (container) (typed FeaturePython)
  n = 0.114318
FEATURE [App::DocumentObjectGroupPython] C_element057  label="C_element : 0.656"  # scripted group (container) (typed FeaturePython)
  n = 0.655824
FEATURE [App::DocumentObjectGroupPython] O_element058  label="O_element : 0.092"  # scripted group (container) (typed FeaturePython)
  n = 0.0921831
FEATURE [App::DocumentObjectGroupPython] Mg_element004  label="Mg_element : 0.135"  # scripted group (container) (typed FeaturePython)
  n = 0.134792
FEATURE [App::DocumentObjectGroupPython] Ca_element013  label="Ca_element : 0.003"  # scripted group (container) (typed FeaturePython)
  n = 0.002883
FEATURE [App::DocumentObjectGroupPython] G4_M3_WAX  # scripted group (container) (typed FeaturePython)
  Dunit = g/cm3
  Dvalue = 1.05
  Group = -> [H_element052,C_element057,O_element058,Mg_element004,Ca_element013]
  conduct = 2
  density = 1
  expand = 3
  formula = G4_M3_WAX
  name = G4_M3_WAX
  specific = 4
FEATURE [App::DocumentObjectGroupPython] Mg_element005  label="Mg_element : 1"  # scripted group (container) (typed FeaturePython)
  n = 1
  ref = Mg_element
FEATURE [App::DocumentObjectGroupPython] C_element058  label="C_element : 031"  # scripted group (container) (typed FeaturePython)
  n = 1
  ref = C_element
FEATURE [App::DocumentObjectGroupPython] O_element059  label="O_element : 030"  # scripted group (container) (typed FeaturePython)
  n = 3
  ref = O_element
FEATURE [App::DocumentObjectGroupPython] G4_MAGNESIUM_CARBONATE  # scripted group (container) (typed FeaturePython)
  Dunit = g/cm3
  Dvalue = 2.958
  Group = -> [Mg_element005,C_element058,O_element059]
  conduct = 2
  density = 1
  expand = 3
  formula = G4_MAGNESIUM_CARBONATE
  name = G4_MAGNESIUM_CARBONATE
  specific = 4
FEATURE [App::DocumentObjectGroupPython] Mg_element006  label="Mg_element : 002"  # scripted group (container) (typed FeaturePython)
  n = 1
  ref = Mg_element
FEATURE [App::DocumentObjectGroupPython] F_element013  label="F_element : 005"  # scripted group (container) (typed FeaturePython)
  n = 2
  ref = F_element
FEATURE [App::DocumentObjectGroupPython] G4_MAGNESIUM_FLUORIDE  # scripted group (container) (typed FeaturePython)
  Dunit = g/cm3
  Dvalue = 3
  Group = -> [Mg_element006,F_element013]
  conduct = 2
  density = 1
  expand = 3
  formula = G4_MAGNESIUM_FLUORIDE
  name = G4_MAGNESIUM_FLUORIDE
  specific = 4
FEATURE [App::DocumentObjectGroupPython] Mg_element007  label="Mg_element : 003"  # scripted group (container) (typed FeaturePython)
  n = 1
  ref = Mg_element
FEATURE [App::DocumentObjectGroupPython] O_element060  label="O_element : 031"  # scripted group (container) (typed FeaturePython)
  n = 1
  ref = O_element
FEATURE [App::DocumentObjectGroupPython] G4_MAGNESIUM_OXIDE  # scripted group (container) (typed FeaturePython)
  Dunit = g/cm3
  Dvalue = 3.58
  Group = -> [Mg_element007,O_element060]
  conduct = 2
  density = 1
  expand = 3
  formula = G4_MAGNESIUM_OXIDE
  name = G4_MAGNESIUM_OXIDE
  specific = 4
FEATURE [App::DocumentObjectGroupPython] Mg_element008  label="Mg_element : 004"  # scripted group (container) (typed FeaturePython)
  n = 1
  ref = Mg_element
FEATURE [App::DocumentObjectGroupPython] B_element006  label="B_element : 006"  # scripted group (container) (typed FeaturePython)
  n = 4
  ref = B_element
FEATURE [App::DocumentObjectGroupPython] O_element061  label="O_element : 032"  # scripted group (container) (typed FeaturePython)
  n = 7
  ref = O_element
FEATURE [App::DocumentObjectGroupPython] G4_MAGNESIUM_TETRABORATE  # scripted group (container) (typed FeaturePython)
  Dunit = g/cm3
  Dvalue = 2.53
  Group = -> [Mg_element008,B_element006,O_element061]
  conduct = 2
  density = 1
  expand = 3
  formula = G4_MAGNESIUM_TETRABORATE
  name = G4_MAGNESIUM_TETRABORATE
  specific = 4
FEATURE [App::DocumentObjectGroupPython] Hg_element001  label="Hg_element : 1"  # scripted group (container) (typed FeaturePython)
  n = 1
  ref = Hg_element
FEATURE [App::DocumentObjectGroupPython] I_element004  label="I_element : 2"  # scripted group (container) (typed FeaturePython)
  n = 2
  ref = I_element
FEATURE [App::DocumentObjectGroupPython] G4_MERCURIC_IODIDE  # scripted group (container) (typed FeaturePython)
  Dunit = g/cm3
  Dvalue = 6.36
  Group = -> [Hg_element001,I_element004]
  conduct = 2
  density = 1
  expand = 3
  formula = G4_MERCURIC_IODIDE
  name = G4_MERCURIC_IODIDE
  specific = 4
FEATURE [App::DocumentObjectGroupPython] C_element059  label="C_element : 032"  # scripted group (container) (typed FeaturePython)
  n = 1
  ref = C_element
FEATURE [App::DocumentObjectGroupPython] H_element053  label="H_element : 028"  # scripted group (container) (typed FeaturePython)
  n = 4
  ref = H_element
FEATURE [App::DocumentObjectGroupPython] G4_METHANE  # scripted group (container) (typed FeaturePython)
  Dunit = g/cm3
  Dvalue = 0.000667151
  Group = -> [C_element059,H_element053]
  conduct = 2
  density = 1
  expand = 3
  formula = G4_METHANE
  name = G4_METHANE
  specific = 4
FEATURE [App::DocumentObjectGroupPython] C_element060  label="C_element : 033"  # scripted group (container) (typed FeaturePython)
  n = 1
  ref = C_element
FEATURE [App::DocumentObjectGroupPython] H_element054  label="H_element : 029"  # scripted group (container) (typed FeaturePython)
  n = 4
  ref = H_element
FEATURE [App::DocumentObjectGroupPython] O_element062  label="O_element : 033"  # scripted group (container) (typed FeaturePython)
  n = 1
  ref = O_element
FEATURE [App::DocumentObjectGroupPython] G4_METHANOL  # scripted group (container) (typed FeaturePython)
  Dunit = g/cm3
  Dvalue = 0.7914
  Group = -> [C_element060,H_element054,O_element062]
  conduct = 2
  density = 1
  expand = 3
  formula = G4_METHANOL
  name = G4_METHANOL
  specific = 4
FEATURE [App::DocumentObjectGroupPython] H_element055  label="H_element : 0.134"  # scripted group (container) (typed FeaturePython)
  n = 0.13404
FEATURE [App::DocumentObjectGroupPython] C_element061  label="C_element : 0.778"  # scripted group (container) (typed FeaturePython)
  n = 0.77796
FEATURE [App::DocumentObjectGroupPython] O_element063  label="O_element : 0.035"  # scripted group (container) (typed FeaturePython)
  n = 0.03502
FEATURE [App::DocumentObjectGroupPython] Mg_element009  label="Mg_element : 0.039"  # scripted group (container) (typed FeaturePython)
  n = 0.038594
FEATURE [App::DocumentObjectGroupPython] Ti_element002  label="Ti_element : 0.014"  # scripted group (container) (typed FeaturePython)
  n = 0.014386
FEATURE [App::DocumentObjectGroupPython] G4_MIX_D_WAX  # scripted group (container) (typed FeaturePython)
  Dunit = g/cm3
  Dvalue = 0.99
  Group = -> [H_element055,C_element061,O_element063,Mg_element009,Ti_element002]
  conduct = 2
  density = 1
  expand = 3
  formula = G4_MIX_D_WAX
  name = G4_MIX_D_WAX
  specific = 4
FEATURE [App::DocumentObjectGroupPython] H_element056  label="H_element : 0.135"  # scripted group (container) (typed FeaturePython)
  n = 0.081192
FEATURE [App::DocumentObjectGroupPython] C_element062  label="C_element : 0.583"  # scripted group (container) (typed FeaturePython)
  n = 0.583442
FEATURE [App::DocumentObjectGroupPython] N_element024  label="N_element : 0.018"  # scripted group (container) (typed FeaturePython)
  n = 0.017798
FEATURE [App::DocumentObjectGroupPython] O_element064  label="O_element : 0.186"  # scripted group (container) (typed FeaturePython)
  n = 0.186381
FEATURE [App::DocumentObjectGroupPython] Mg_element010  label="Mg_element : 0.130"  # scripted group (container) (typed FeaturePython)
  n = 0.130287
FEATURE [App::DocumentObjectGroupPython] Cl_element015  label="Cl_element : 0.588"  # scripted group (container) (typed FeaturePython)
  n = 0.0009
FEATURE [App::DocumentObjectGroupPython] G4_MS20_TISSUE  # scripted group (container) (typed FeaturePython)
  Dunit = g/cm3
  Dvalue = 1
  Group = -> [H_element056,C_element062,N_element024,O_element064,Mg_element010,Cl_element015]
  conduct = 2
  density = 1
  expand = 3
  formula = G4_MS20_TISSUE
  name = G4_MS20_TISSUE
  specific = 4
FEATURE [App::DocumentObjectGroupPython] H_element057  label="H_element : 0.136"  # scripted group (container) (typed FeaturePython)
  n = 0.102
FEATURE [App::DocumentObjectGroupPython] C_element063  label="C_element : 0.143"  # scripted group (container) (typed FeaturePython)
  n = 0.143
FEATURE [App::DocumentObjectGroupPython] N_element025  label="N_element : 0.034"  # scripted group (container) (typed FeaturePython)
  n = 0.034
FEATURE [App::DocumentObjectGroupPython] O_element065  label="O_element : 0.710"  # scripted group (container) (typed FeaturePython)
  n = 0.71
FEATURE [App::DocumentObjectGroupPython] Na_element011  label="Na_element : 0.098"  # scripted group (container) (typed FeaturePython)
  n = 0.001
FEATURE [App::DocumentObjectGroupPython] P_element007  label="P_element : 0.002"  # scripted group (container) (typed FeaturePython)
  n = 0.002
FEATURE [App::DocumentObjectGroupPython] S_element017  label="S_element : 0.018"  # scripted group (container) (typed FeaturePython)
  n = 0.003
FEATURE [App::DocumentObjectGroupPython] Cl_element016  label="Cl_element : 0.589"  # scripted group (container) (typed FeaturePython)
  n = 0.001
FEATURE [App::DocumentObjectGroupPython] K_element006  label="K_element : 0.004"  # scripted group (container) (typed FeaturePython)
  n = 0.004
FEATURE [App::DocumentObjectGroupPython] G4_MUSCLE_SKELETAL_ICRP  # scripted group (container) (typed FeaturePython)
  Dunit = g/cm3
  Dvalue = 1.05
  Group = -> [H_element057,C_element063,N_element025,O_element065,Na_element011,P_element007,S_element017,Cl_element016,K_element006]
  conduct = 2
  density = 1
  expand = 3
  formula = G4_MUSCLE_SKELETAL_ICRP
  name = G4_MUSCLE_SKELETAL_ICRP
  specific = 4
FEATURE [App::DocumentObjectGroupPython] H_element058  label="H_element : 0.137"  # scripted group (container) (typed FeaturePython)
  n = 0.102102
FEATURE [App::DocumentObjectGroupPython] C_element064  label="C_element : 0.123"  # scripted group (container) (typed FeaturePython)
  n = 0.123123
FEATURE [App::DocumentObjectGroupPython] N_element026  label="N_element : 0.756"  # scripted group (container) (typed FeaturePython)
  n = 0.035035
FEATURE [App::DocumentObjectGroupPython] O_element066  label="O_element : 0.730"  # scripted group (container) (typed FeaturePython)
  n = 0.72973
FEATURE [App::DocumentObjectGroupPython] Na_element012  label="Na_element : 0.099"  # scripted group (container) (typed FeaturePython)
  n = 0.001001
FEATURE [App::DocumentObjectGroupPython] P_element008  label="P_element : 0.106"  # scripted group (container) (typed FeaturePython)
  n = 0.002002
FEATURE [App::DocumentObjectGroupPython] S_element018  label="S_element : 0.019"  # scripted group (container) (typed FeaturePython)
  n = 0.004004
FEATURE [App::DocumentObjectGroupPython] K_element007  label="K_element : 0.016"  # scripted group (container) (typed FeaturePython)
  n = 0.003003
FEATURE [App::DocumentObjectGroupPython] G4_MUSCLE_STRIATED_ICRU  # scripted group (container) (typed FeaturePython)
  Dunit = g/cm3
  Dvalue = 1.04
  Group = -> [H_element058,C_element064,N_element026,O_element066,Na_element012,P_element008,S_element018,K_element007]
  conduct = 2
  density = 1
  expand = 3
  formula = G4_MUSCLE_STRIATED_ICRU
  name = G4_MUSCLE_STRIATED_ICRU
  specific = 4
FEATURE [App::DocumentObjectGroupPython] H_element059  label="H_element : 0.098"  # scripted group (container) (typed FeaturePython)
  n = 0.0982341
FEATURE [App::DocumentObjectGroupPython] C_element065  label="C_element : 0.156"  # scripted group (container) (typed FeaturePython)
  n = 0.156214
FEATURE [App::DocumentObjectGroupPython] N_element027  label="N_element : 0.757"  # scripted group (container) (typed FeaturePython)
  n = 0.035451
FEATURE [App::DocumentObjectGroupPython] O_element067  label="O_element : 0.880"  # scripted group (container) (typed FeaturePython)
  n = 0.710101
FEATURE [App::DocumentObjectGroupPython] G4_MUSCLE_WITH_SUCROSE  # scripted group (container) (typed FeaturePython)
  Dunit = g/cm3
  Dvalue = 1.11
  Group = -> [H_element059,C_element065,N_element027,O_element067]
  conduct = 2
  density = 1
  expand = 3
  formula = G4_MUSCLE_WITH_SUCROSE
  name = G4_MUSCLE_WITH_SUCROSE
  specific = 4
FEATURE [App::DocumentObjectGroupPython] H_element060  label="H_element : 0.138"  # scripted group (container) (typed FeaturePython)
  n = 0.101969
FEATURE [App::DocumentObjectGroupPython] C_element066  label="C_element : 0.120"  # scripted group (container) (typed FeaturePython)
  n = 0.120058
FEATURE [App::DocumentObjectGroupPython] N_element028  label="N_element : 0.758"  # scripted group (container) (typed FeaturePython)
  n = 0.035451
FEATURE [App::DocumentObjectGroupPython] O_element068  label="O_element : 0.743"  # scripted group (container) (typed FeaturePython)
  n = 0.742522
FEATURE [App::DocumentObjectGroupPython] G4_MUSCLE_WITHOUT_SUCROSE  # scripted group (container) (typed FeaturePython)
  Dunit = g/cm3
  Dvalue = 1.07
  Group = -> [H_element060,C_element066,N_element028,O_element068]
  conduct = 2
  density = 1
  expand = 3
  formula = G4_MUSCLE_WITHOUT_SUCROSE
  name = G4_MUSCLE_WITHOUT_SUCROSE
  specific = 4
FEATURE [App::DocumentObjectGroupPython] C_element067  label="C_element : 10"  # scripted group (container) (typed FeaturePython)
  n = 10
  ref = C_element
FEATURE [App::DocumentObjectGroupPython] H_element061  label="H_element : 030"  # scripted group (container) (typed FeaturePython)
  n = 8
  ref = H_element
FEATURE [App::DocumentObjectGroupPython] G4_NAPHTHALENE  # scripted group (container) (typed FeaturePython)
  Dunit = g/cm3
  Dvalue = 1.145
  Group = -> [C_element067,H_element061]
  conduct = 2
  density = 1
  expand = 3
  formula = G4_NAPHTHALENE
  name = G4_NAPHTHALENE
  specific = 4
FEATURE [App::DocumentObjectGroupPython] C_element068  label="C_element : 034"  # scripted group (container) (typed FeaturePython)
  n = 6
  ref = C_element
FEATURE [App::DocumentObjectGroupPython] H_element062  label="H_element : 031"  # scripted group (container) (typed FeaturePython)
  n = 5
  ref = H_element
FEATURE [App::DocumentObjectGroupPython] N_element029  label="N_element : 012"  # scripted group (container) (typed FeaturePython)
  n = 1
  ref = N_element
FEATURE [App::DocumentObjectGroupPython] O_element069  label="O_element : 034"  # scripted group (container) (typed FeaturePython)
  n = 2
  ref = O_element
FEATURE [App::DocumentObjectGroupPython] G4_NITROBENZENE  # scripted group (container) (typed FeaturePython)
  Dunit = g/cm3
  Dvalue = 1.19867
  Group = -> [C_element068,H_element062,N_element029,O_element069]
  conduct = 2
  density = 1
  expand = 3
  formula = G4_NITROBENZENE
  name = G4_NITROBENZENE
  specific = 4
FEATURE [App::DocumentObjectGroupPython] N_element030  label="N_element : 013"  # scripted group (container) (typed FeaturePython)
  n = 2
  ref = N_element
FEATURE [App::DocumentObjectGroupPython] O_element070  label="O_element : 035"  # scripted group (container) (typed FeaturePython)
  n = 1
  ref = O_element
FEATURE [App::DocumentObjectGroupPython] G4_NITROUS_OXIDE  # scripted group (container) (typed FeaturePython)
  Dunit = g/cm3
  Dvalue = 0.00183094
  Group = -> [N_element030,O_element070]
  conduct = 2
  density = 1
  expand = 3
  formula = G4_NITROUS_OXIDE
  name = G4_NITROUS_OXIDE
  specific = 4
FEATURE [App::DocumentObjectGroupPython] H_element063  label="H_element : 0.104"  # scripted group (container) (typed FeaturePython)
  n = 0.103509
FEATURE [App::DocumentObjectGroupPython] C_element069  label="C_element : 0.648"  # scripted group (container) (typed FeaturePython)
  n = 0.648416
FEATURE [App::DocumentObjectGroupPython] N_element031  label="N_element : 0.100"  # scripted group (container) (typed FeaturePython)
  n = 0.0995361
FEATURE [App::DocumentObjectGroupPython] O_element071  label="O_element : 0.149"  # scripted group (container) (typed FeaturePython)
  n = 0.148539
FEATURE [App::DocumentObjectGroupPython] G4_NYLON_8062  label="G4_NYLON-8062"  # scripted group (container) (typed FeaturePython)
  Dunit = g/cm3
  Dvalue = 1.08
  Group = -> [H_element063,C_element069,N_element031,O_element071]
  conduct = 2
  density = 1
  expand = 3
  formula = G4_NYLON-8062
  name = G4_NYLON-8062
  specific = 4
FEATURE [App::DocumentObjectGroupPython] C_element070  label="C_element : 035"  # scripted group (container) (typed FeaturePython)
  n = 6
  ref = C_element
FEATURE [App::DocumentObjectGroupPython] H_element064  label="H_element : 11"  # scripted group (container) (typed FeaturePython)
  n = 11
  ref = H_element
FEATURE [App::DocumentObjectGroupPython] N_element032  label="N_element : 014"  # scripted group (container) (typed FeaturePython)
  n = 1
  ref = N_element
FEATURE [App::DocumentObjectGroupPython] O_element072  label="O_element : 036"  # scripted group (container) (typed FeaturePython)
  n = 1
  ref = O_element
FEATURE [App::DocumentObjectGroupPython] G4_NYLON_6_6  label="G4_NYLON-6-6"  # scripted group (container) (typed FeaturePython)
  Dunit = g/cm3
  Dvalue = 1.14
  Group = -> [C_element070,H_element064,N_element032,O_element072]
  conduct = 2
  density = 1
  expand = 3
  formula = G4_NYLON-6-6
  name = G4_NYLON-6-6
  specific = 4
FEATURE [App::DocumentObjectGroupPython] H_element065  label="H_element : 0.139"  # scripted group (container) (typed FeaturePython)
  n = 0.107062
FEATURE [App::DocumentObjectGroupPython] C_element071  label="C_element : 0.680"  # scripted group (container) (typed FeaturePython)
  n = 0.680449
FEATURE [App::DocumentObjectGroupPython] N_element033  label="N_element : 0.099"  # scripted group (container) (typed FeaturePython)
  n = 0.099189
FEATURE [App::DocumentObjectGroupPython] O_element073  label="O_element : 0.113"  # scripted group (container) (typed FeaturePython)
  n = 0.1133
FEATURE [App::DocumentObjectGroupPython] G4_NYLON_6_10  label="G4_NYLON-6-10"  # scripted group (container) (typed FeaturePython)
  Dunit = g/cm3
  Dvalue = 1.14
  Group = -> [H_element065,C_element071,N_element033,O_element073]
  conduct = 2
  density = 1
  expand = 3
  formula = G4_NYLON-6-10
  name = G4_NYLON-6-10
  specific = 4
FEATURE [App::DocumentObjectGroupPython] H_element066  label="H_element : 0.140"  # scripted group (container) (typed FeaturePython)
  n = 0.115476
FEATURE [App::DocumentObjectGroupPython] C_element072  label="C_element : 0.721"  # scripted group (container) (typed FeaturePython)
  n = 0.720818
FEATURE [App::DocumentObjectGroupPython] N_element034  label="N_element : 0.076"  # scripted group (container) (typed FeaturePython)
  n = 0.0764169
FEATURE [App::DocumentObjectGroupPython] O_element074  label="O_element : 0.087"  # scripted group (container) (typed FeaturePython)
  n = 0.0872889
FEATURE [App::DocumentObjectGroupPython] G4_NYLON_11_RILSAN  label="G4_NYLON-11_RILSAN"  # scripted group (container) (typed FeaturePython)
  Dunit = g/cm3
  Dvalue = 1.425
  Group = -> [H_element066,C_element072,N_element034,O_element074]
  conduct = 2
  density = 1
  expand = 3
  formula = G4_NYLON-11_RILSAN
  name = G4_NYLON-11_RILSAN
  specific = 4
FEATURE [App::DocumentObjectGroupPython] C_element073  label="C_element : 8"  # scripted group (container) (typed FeaturePython)
  n = 8
  ref = C_element
FEATURE [App::DocumentObjectGroupPython] H_element067  label="H_element : 18"  # scripted group (container) (typed FeaturePython)
  n = 18
  ref = H_element
FEATURE [App::DocumentObjectGroupPython] G4_OCTANE  # scripted group (container) (typed FeaturePython)
  Dunit = g/cm3
  Dvalue = 0.7026
  Group = -> [C_element073,H_element067]
  conduct = 2
  density = 1
  expand = 3
  formula = G4_OCTANE
  name = G4_OCTANE
  specific = 4
FEATURE [App::DocumentObjectGroupPython] C_element074  label="C_element : 25"  # scripted group (container) (typed FeaturePython)
  n = 25
  ref = C_element
FEATURE [App::DocumentObjectGroupPython] H_element068  label="H_element : 52"  # scripted group (container) (typed FeaturePython)
  n = 52
  ref = H_element
FEATURE [App::DocumentObjectGroupPython] G4_PARAFFIN  # scripted group (container) (typed FeaturePython)
  Dunit = g/cm3
  Dvalue = 0.93
  Group = -> [C_element074,H_element068]
  conduct = 2
  density = 1
  expand = 3
  formula = G4_PARAFFIN
  name = G4_PARAFFIN
  specific = 4
FEATURE [App::DocumentObjectGroupPython] C_element075  label="C_element : 036"  # scripted group (container) (typed FeaturePython)
  n = 5
  ref = C_element
FEATURE [App::DocumentObjectGroupPython] H_element069  label="H_element : 032"  # scripted group (container) (typed FeaturePython)
  n = 12
  ref = H_element
FEATURE [App::DocumentObjectGroupPython] G4_N_PENTANE  label="G4_N-PENTANE"  # scripted group (container) (typed FeaturePython)
  Dunit = g/cm3
  Dvalue = 0.6262
  Group = -> [C_element075,H_element069]
  conduct = 2
  density = 1
  expand = 3
  formula = G4_N-PENTANE
  name = G4_N-PENTANE
  specific = 4
FEATURE [App::DocumentObjectGroupPython] H_element070  label="H_element : 0.014"  # scripted group (container) (typed FeaturePython)
  n = 0.0141
FEATURE [App::DocumentObjectGroupPython] C_element076  label="C_element : 0.072"  # scripted group (container) (typed FeaturePython)
  n = 0.072261
FEATURE [App::DocumentObjectGroupPython] N_element035  label="N_element : 0.019"  # scripted group (container) (typed FeaturePython)
  n = 0.01932
FEATURE [App::DocumentObjectGroupPython] O_element075  label="O_element : 0.066"  # scripted group (container) (typed FeaturePython)
  n = 0.066101
FEATURE [App::DocumentObjectGroupPython] S_element019  label="S_element : 0.020"  # scripted group (container) (typed FeaturePython)
  n = 0.00189
FEATURE [App::DocumentObjectGroupPython] Br_element004  label="Br_element : 0.349"  # scripted group (container) (typed FeaturePython)
  n = 0.349103
FEATURE [App::DocumentObjectGroupPython] Ag_element001  label="Ag_element : 0.474"  # scripted group (container) (typed FeaturePython)
  n = 0.474105
FEATURE [App::DocumentObjectGroupPython] I_element005  label="I_element : 0.003"  # scripted group (container) (typed FeaturePython)
  n = 0.00312
FEATURE [App::DocumentObjectGroupPython] G4_PHOTO_EMULSION  # scripted group (container) (typed FeaturePython)
  Dunit = g/cm3
  Dvalue = 3.815
  Group = -> [H_element070,C_element076,N_element035,O_element075,S_element019,Br_element004,Ag_element001,I_element005]
  conduct = 2
  density = 1
  expand = 3
  formula = G4_PHOTO_EMULSION
  name = G4_PHOTO_EMULSION
  specific = 4
FEATURE [App::DocumentObjectGroupPython] C_element077  label="C_element : 9"  # scripted group (container) (typed FeaturePython)
  n = 9
  ref = C_element
FEATURE [App::DocumentObjectGroupPython] H_element071  label="H_element : 033"  # scripted group (container) (typed FeaturePython)
  n = 10
  ref = H_element
FEATURE [App::DocumentObjectGroupPython] G4_PLASTIC_SC_VINYLTOLUENE  # scripted group (container) (typed FeaturePython)
  Dunit = g/cm3
  Dvalue = 1.032
  Group = -> [C_element077,H_element071]
  conduct = 2
  density = 1
  expand = 3
  formula = G4_PLASTIC_SC_VINYLTOLUENE
  name = G4_PLASTIC_SC_VINYLTOLUENE
  specific = 4
FEATURE [App::DocumentObjectGroupPython] Pu_element001  label="Pu_element : 1"  # scripted group (container) (typed FeaturePython)
  n = 1
  ref = Pu_element
FEATURE [App::DocumentObjectGroupPython] O_element076  label="O_element : 037"  # scripted group (container) (typed FeaturePython)
  n = 2
  ref = O_element
FEATURE [App::DocumentObjectGroupPython] G4_PLUTONIUM_DIOXIDE  # scripted group (container) (typed FeaturePython)
  Dunit = g/cm3
  Dvalue = 11.46
  Group = -> [Pu_element001,O_element076]
  conduct = 2
  density = 1
  expand = 3
  formula = G4_PLUTONIUM_DIOXIDE
  name = G4_PLUTONIUM_DIOXIDE
  specific = 4
FEATURE [App::DocumentObjectGroupPython] C_element078  label="C_element : 037"  # scripted group (container) (typed FeaturePython)
  n = 3
  ref = C_element
FEATURE [App::DocumentObjectGroupPython] H_element072  label="H_element : 034"  # scripted group (container) (typed FeaturePython)
  n = 3
  ref = H_element
FEATURE [App::DocumentObjectGroupPython] N_element036  label="N_element : 015"  # scripted group (container) (typed FeaturePython)
  n = 1
  ref = N_element
FEATURE [App::DocumentObjectGroupPython] G4_POLYACRYLONITRILE  # scripted group (container) (typed FeaturePython)
  Dunit = g/cm3
  Dvalue = 1.17
  Group = -> [C_element078,H_element072,N_element036]
  conduct = 2
  density = 1
  expand = 3
  formula = G4_POLYACRYLONITRILE
  name = G4_POLYACRYLONITRILE
  specific = 4
FEATURE [App::DocumentObjectGroupPython] C_element079  label="C_element : 16"  # scripted group (container) (typed FeaturePython)
  n = 16
  ref = C_element
FEATURE [App::DocumentObjectGroupPython] H_element073  label="H_element : 035"  # scripted group (container) (typed FeaturePython)
  n = 14
  ref = H_element
FEATURE [App::DocumentObjectGroupPython] O_element077  label="O_element : 038"  # scripted group (container) (typed FeaturePython)
  n = 3
  ref = O_element
FEATURE [App::DocumentObjectGroupPython] G4_POLYCARBONATE  # scripted group (container) (typed FeaturePython)
  Dunit = g/cm3
  Dvalue = 1.2
  Group = -> [C_element079,H_element073,O_element077]
  conduct = 2
  density = 1
  expand = 3
  formula = G4_POLYCARBONATE
  name = G4_POLYCARBONATE
  specific = 4
FEATURE [App::DocumentObjectGroupPython] C_element080  label="C_element : 038"  # scripted group (container) (typed FeaturePython)
  n = 8
  ref = C_element
FEATURE [App::DocumentObjectGroupPython] H_element074  label="H_element : 036"  # scripted group (container) (typed FeaturePython)
  n = 7
  ref = H_element
FEATURE [App::DocumentObjectGroupPython] Cl_element017  label="Cl_element : 007"  # scripted group (container) (typed FeaturePython)
  n = 1
  ref = Cl_element
FEATURE [App::DocumentObjectGroupPython] G4_POLYCHLOROSTYRENE  # scripted group (container) (typed FeaturePython)
  Dunit = g/cm3
  Dvalue = 1.3
  Group = -> [C_element080,H_element074,Cl_element017]
  conduct = 2
  density = 1
  expand = 3
  formula = G4_POLYCHLOROSTYRENE
  name = G4_POLYCHLOROSTYRENE
  specific = 4
FEATURE [App::DocumentObjectGroupPython] C_element081  label="C_element : 039"  # scripted group (container) (typed FeaturePython)
  n = 1
  ref = C_element
FEATURE [App::DocumentObjectGroupPython] H_element075  label="H_element : 037"  # scripted group (container) (typed FeaturePython)
  n = 2
  ref = H_element
FEATURE [App::DocumentObjectGroupPython] G4_POLYETHYLENE  # scripted group (container) (typed FeaturePython)
  Dunit = g/cm3
  Dvalue = 0.94
  Group = -> [C_element081,H_element075]
  conduct = 2
  density = 1
  expand = 3
  formula = G4_POLYETHYLENE
  name = G4_POLYETHYLENE
  specific = 4
FEATURE [App::DocumentObjectGroupPython] C_element082  label="C_element : 040"  # scripted group (container) (typed FeaturePython)
  n = 10
  ref = C_element
FEATURE [App::DocumentObjectGroupPython] H_element076  label="H_element : 038"  # scripted group (container) (typed FeaturePython)
  n = 8
  ref = H_element
FEATURE [App::DocumentObjectGroupPython] O_element078  label="O_element : 039"  # scripted group (container) (typed FeaturePython)
  n = 4
  ref = O_element
FEATURE [App::DocumentObjectGroupPython] G4_MYLAR  # scripted group (container) (typed FeaturePython)
  Dunit = g/cm3
  Dvalue = 1.4
  Group = -> [C_element082,H_element076,O_element078]
  conduct = 2
  density = 1
  expand = 3
  formula = G4_MYLAR
  name = G4_MYLAR
  specific = 4
FEATURE [App::DocumentObjectGroupPython] C_element083  label="C_element : 041"  # scripted group (container) (typed FeaturePython)
  n = 5
  ref = C_element
FEATURE [App::DocumentObjectGroupPython] H_element077  label="H_element : 039"  # scripted group (container) (typed FeaturePython)
  n = 8
  ref = H_element
FEATURE [App::DocumentObjectGroupPython] O_element079  label="O_element : 040"  # scripted group (container) (typed FeaturePython)
  n = 2
  ref = O_element
FEATURE [App::DocumentObjectGroupPython] G4_PLEXIGLASS  # scripted group (container) (typed FeaturePython)
  Dunit = g/cm3
  Dvalue = 1.19
  Group = -> [C_element083,H_element077,O_element079]
  conduct = 2
  density = 1
  expand = 3
  formula = G4_PLEXIGLASS
  name = G4_PLEXIGLASS
  specific = 4
FEATURE [App::DocumentObjectGroupPython] C_element084  label="C_element : 042"  # scripted group (container) (typed FeaturePython)
  n = 1
  ref = C_element
FEATURE [App::DocumentObjectGroupPython] H_element078  label="H_element : 040"  # scripted group (container) (typed FeaturePython)
  n = 2
  ref = H_element
FEATURE [App::DocumentObjectGroupPython] O_element080  label="O_element : 041"  # scripted group (container) (typed FeaturePython)
  n = 1
  ref = O_element
FEATURE [App::DocumentObjectGroupPython] G4_POLYOXYMETHYLENE  # scripted group (container) (typed FeaturePython)
  Dunit = g/cm3
  Dvalue = 1.425
  Group = -> [C_element084,H_element078,O_element080]
  conduct = 2
  density = 1
  expand = 3
  formula = G4_POLYOXYMETHYLENE
  name = G4_POLYOXYMETHYLENE
  specific = 4
FEATURE [App::DocumentObjectGroupPython] C_element085  label="C_element : 043"  # scripted group (container) (typed FeaturePython)
  n = 2
  ref = C_element
FEATURE [App::DocumentObjectGroupPython] H_element079  label="H_element : 041"  # scripted group (container) (typed FeaturePython)
  n = 4
  ref = H_element
FEATURE [App::DocumentObjectGroupPython] G4_POLYPROPYLENE  # scripted group (container) (typed FeaturePython)
  Dunit = g/cm3
  Dvalue = 0.9
  Group = -> [C_element085,H_element079]
  conduct = 2
  density = 1
  expand = 3
  formula = G4_POLYPROPYLENE
  name = G4_POLYPROPYLENE
  specific = 4
FEATURE [App::DocumentObjectGroupPython] C_element086  label="C_element : 044"  # scripted group (container) (typed FeaturePython)
  n = 8
  ref = C_element
FEATURE [App::DocumentObjectGroupPython] H_element080  label="H_element : 042"  # scripted group (container) (typed FeaturePython)
  n = 8
  ref = H_element
FEATURE [App::DocumentObjectGroupPython] G4_POLYSTYRENE  # scripted group (container) (typed FeaturePython)
  Dunit = g/cm3
  Dvalue = 1.06
  Group = -> [C_element086,H_element080]
  conduct = 2
  density = 1
  expand = 3
  formula = G4_POLYSTYRENE
  name = G4_POLYSTYRENE
  specific = 4
FEATURE [App::DocumentObjectGroupPython] C_element087  label="C_element : 045"  # scripted group (container) (typed FeaturePython)
  n = 2
  ref = C_element
FEATURE [App::DocumentObjectGroupPython] F_element014  label="F_element : 4"  # scripted group (container) (typed FeaturePython)
  n = 4
  ref = F_element
FEATURE [App::DocumentObjectGroupPython] G4_TEFLON  # scripted group (container) (typed FeaturePython)
  Dunit = g/cm3
  Dvalue = 2.2
  Group = -> [C_element087,F_element014]
  conduct = 2
  density = 1
  expand = 3
  formula = G4_TEFLON
  name = G4_TEFLON
  specific = 4
FEATURE [App::DocumentObjectGroupPython] C_element088  label="C_element : 046"  # scripted group (container) (typed FeaturePython)
  n = 2
  ref = C_element
FEATURE [App::DocumentObjectGroupPython] F_element015  label="F_element : 006"  # scripted group (container) (typed FeaturePython)
  n = 3
  ref = F_element
FEATURE [App::DocumentObjectGroupPython] Cl_element018  label="Cl_element : 008"  # scripted group (container) (typed FeaturePython)
  n = 1
  ref = Cl_element
FEATURE [App::DocumentObjectGroupPython] G4_POLYTRIFLUOROCHLOROETHYLENE  # scripted group (container) (typed FeaturePython)
  Dunit = g/cm3
  Dvalue = 2.1
  Group = -> [C_element088,F_element015,Cl_element018]
  conduct = 2
  density = 1
  expand = 3
  formula = G4_POLYTRIFLUOROCHLOROETHYLENE
  name = G4_POLYTRIFLUOROCHLOROETHYLENE
  specific = 4
FEATURE [App::DocumentObjectGroupPython] C_element089  label="C_element : 047"  # scripted group (container) (typed FeaturePython)
  n = 4
  ref = C_element
FEATURE [App::DocumentObjectGroupPython] H_element081  label="H_element : 043"  # scripted group (container) (typed FeaturePython)
  n = 6
  ref = H_element
FEATURE [App::DocumentObjectGroupPython] O_element081  label="O_element : 042"  # scripted group (container) (typed FeaturePython)
  n = 2
  ref = O_element
FEATURE [App::DocumentObjectGroupPython] G4_POLYVINYL_ACETATE  # scripted group (container) (typed FeaturePython)
  Dunit = g/cm3
  Dvalue = 1.19
  Group = -> [C_element089,H_element081,O_element081]
  conduct = 2
  density = 1
  expand = 3
  formula = G4_POLYVINYL_ACETATE
  name = G4_POLYVINYL_ACETATE
  specific = 4
FEATURE [App::DocumentObjectGroupPython] C_element090  label="C_element : 048"  # scripted group (container) (typed FeaturePython)
  n = 2
  ref = C_element
FEATURE [App::DocumentObjectGroupPython] H_element082  label="H_element : 044"  # scripted group (container) (typed FeaturePython)
  n = 4
  ref = H_element
FEATURE [App::DocumentObjectGroupPython] O_element082  label="O_element : 043"  # scripted group (container) (typed FeaturePython)
  n = 1
  ref = O_element
FEATURE [App::DocumentObjectGroupPython] G4_POLYVINYL_ALCOHOL  # scripted group (container) (typed FeaturePython)
  Dunit = g/cm3
  Dvalue = 1.3
  Group = -> [C_element090,H_element082,O_element082]
  conduct = 2
  density = 1
  expand = 3
  formula = G4_POLYVINYL_ALCOHOL
  name = G4_POLYVINYL_ALCOHOL
  specific = 4
FEATURE [App::DocumentObjectGroupPython] C_element091  label="C_element : 049"  # scripted group (container) (typed FeaturePython)
  n = 8
  ref = C_element
FEATURE [App::DocumentObjectGroupPython] H_element083  label="H_element : 045"  # scripted group (container) (typed FeaturePython)
  n = 14
  ref = H_element
FEATURE [App::DocumentObjectGroupPython] O_element083  label="O_element : 044"  # scripted group (container) (typed FeaturePython)
  n = 2
  ref = O_element
FEATURE [App::DocumentObjectGroupPython] G4_POLYVINYL_BUTYRAL  # scripted group (container) (typed FeaturePython)
  Dunit = g/cm3
  Dvalue = 1.12
  Group = -> [C_element091,H_element083,O_element083]
  conduct = 2
  density = 1
  expand = 3
  formula = G4_POLYVINYL_BUTYRAL
  name = G4_POLYVINYL_BUTYRAL
  specific = 4
FEATURE [App::DocumentObjectGroupPython] C_element092  label="C_element : 050"  # scripted group (container) (typed FeaturePython)
  n = 2
  ref = C_element
FEATURE [App::DocumentObjectGroupPython] H_element084  label="H_element : 046"  # scripted group (container) (typed FeaturePython)
  n = 3
  ref = H_element
FEATURE [App::DocumentObjectGroupPython] Cl_element019  label="Cl_element : 009"  # scripted group (container) (typed FeaturePython)
  n = 1
  ref = Cl_element
FEATURE [App::DocumentObjectGroupPython] G4_POLYVINYL_CHLORIDE  # scripted group (container) (typed FeaturePython)
  Dunit = g/cm3
  Dvalue = 1.3
  Group = -> [C_element092,H_element084,Cl_element019]
  conduct = 2
  density = 1
  expand = 3
  formula = G4_POLYVINYL_CHLORIDE
  name = G4_POLYVINYL_CHLORIDE
  specific = 4
FEATURE [App::DocumentObjectGroupPython] C_element093  label="C_element : 051"  # scripted group (container) (typed FeaturePython)
  n = 2
  ref = C_element
FEATURE [App::DocumentObjectGroupPython] H_element085  label="H_element : 047"  # scripted group (container) (typed FeaturePython)
  n = 2
  ref = H_element
FEATURE [App::DocumentObjectGroupPython] Cl_element020  label="Cl_element : 010"  # scripted group (container) (typed FeaturePython)
  n = 2
  ref = Cl_element
FEATURE [App::DocumentObjectGroupPython] G4_POLYVINYLIDENE_CHLORIDE  # scripted group (container) (typed FeaturePython)
  Dunit = g/cm3
  Dvalue = 1.7
  Group = -> [C_element093,H_element085,Cl_element020]
  conduct = 2
  density = 1
  expand = 3
  formula = G4_POLYVINYLIDENE_CHLORIDE
  name = G4_POLYVINYLIDENE_CHLORIDE
  specific = 4
FEATURE [App::DocumentObjectGroupPython] C_element094  label="C_element : 052"  # scripted group (container) (typed FeaturePython)
  n = 2
  ref = C_element
FEATURE [App::DocumentObjectGroupPython] H_element086  label="H_element : 048"  # scripted group (container) (typed FeaturePython)
  n = 2
  ref = H_element
FEATURE [App::DocumentObjectGroupPython] F_element016  label="F_element : 007"  # scripted group (container) (typed FeaturePython)
  n = 2
  ref = F_element
FEATURE [App::DocumentObjectGroupPython] G4_POLYVINYLIDENE_FLUORIDE  # scripted group (container) (typed FeaturePython)
  Dunit = g/cm3
  Dvalue = 1.76
  Group = -> [C_element094,H_element086,F_element016]
  conduct = 2
  density = 1
  expand = 3
  formula = G4_POLYVINYLIDENE_FLUORIDE
  name = G4_POLYVINYLIDENE_FLUORIDE
  specific = 4
FEATURE [App::DocumentObjectGroupPython] C_element095  label="C_element : 053"  # scripted group (container) (typed FeaturePython)
  n = 6
  ref = C_element
FEATURE [App::DocumentObjectGroupPython] H_element087  label="H_element : 9"  # scripted group (container) (typed FeaturePython)
  n = 9
  ref = H_element
FEATURE [App::DocumentObjectGroupPython] N_element037  label="N_element : 016"  # scripted group (container) (typed FeaturePython)
  n = 1
  ref = N_element
FEATURE [App::DocumentObjectGroupPython] O_element084  label="O_element : 045"  # scripted group (container) (typed FeaturePython)
  n = 1
  ref = O_element
FEATURE [App::DocumentObjectGroupPython] G4_POLYVINYL_PYRROLIDONE  # scripted group (container) (typed FeaturePython)
  Dunit = g/cm3
  Dvalue = 1.25
  Group = -> [C_element095,H_element087,N_element037,O_element084]
  conduct = 2
  density = 1
  expand = 3
  formula = G4_POLYVINYL_PYRROLIDONE
  name = G4_POLYVINYL_PYRROLIDONE
  specific = 4
FEATURE [App::DocumentObjectGroupPython] K_element008  label="K_element : 1"  # scripted group (container) (typed FeaturePython)
  n = 1
  ref = K_element
FEATURE [App::DocumentObjectGroupPython] I_element006  label="I_element : 003"  # scripted group (container) (typed FeaturePython)
  n = 1
  ref = I_element
FEATURE [App::DocumentObjectGroupPython] G4_POTASSIUM_IODIDE  # scripted group (container) (typed FeaturePython)
  Dunit = g/cm3
  Dvalue = 3.13
  Group = -> [K_element008,I_element006]
  conduct = 2
  density = 1
  expand = 3
  formula = G4_POTASSIUM_IODIDE
  name = G4_POTASSIUM_IODIDE
  specific = 4
FEATURE [App::DocumentObjectGroupPython] K_element009  label="K_element : 2"  # scripted group (container) (typed FeaturePython)
  n = 2
  ref = K_element
FEATURE [App::DocumentObjectGroupPython] O_element085  label="O_element : 046"  # scripted group (container) (typed FeaturePython)
  n = 1
  ref = O_element
FEATURE [App::DocumentObjectGroupPython] G4_POTASSIUM_OXIDE  # scripted group (container) (typed FeaturePython)
  Dunit = g/cm3
  Dvalue = 2.32
  Group = -> [K_element009,O_element085]
  conduct = 2
  density = 1
  expand = 3
  formula = G4_POTASSIUM_OXIDE
  name = G4_POTASSIUM_OXIDE
  specific = 4
FEATURE [App::DocumentObjectGroupPython] C_element096  label="C_element : 054"  # scripted group (container) (typed FeaturePython)
  n = 3
  ref = C_element
FEATURE [App::DocumentObjectGroupPython] H_element088  label="H_element : 049"  # scripted group (container) (typed FeaturePython)
  n = 8
  ref = H_element
FEATURE [App::DocumentObjectGroupPython] G4_PROPANE  # scripted group (container) (typed FeaturePython)
  Dunit = g/cm3
  Dvalue = 0.00187939
  Group = -> [C_element096,H_element088]
  conduct = 2
  density = 1
  expand = 3
  formula = G4_PROPANE
  name = G4_PROPANE
  specific = 4
FEATURE [App::DocumentObjectGroupPython] C_element097  label="C_element : 055"  # scripted group (container) (typed FeaturePython)
  n = 3
  ref = C_element
FEATURE [App::DocumentObjectGroupPython] H_element089  label="H_element : 050"  # scripted group (container) (typed FeaturePython)
  n = 8
  ref = H_element
FEATURE [App::DocumentObjectGroupPython] G4_lPROPANE  # scripted group (container) (typed FeaturePython)
  Dunit = g/cm3
  Dvalue = 0.43
  Group = -> [C_element097,H_element089]
  conduct = 2
  density = 1
  expand = 3
  formula = G4_lPROPANE
  name = G4_lPROPANE
  specific = 4
FEATURE [App::DocumentObjectGroupPython] C_element098  label="C_element : 056"  # scripted group (container) (typed FeaturePython)
  n = 3
  ref = C_element
FEATURE [App::DocumentObjectGroupPython] H_element090  label="H_element : 051"  # scripted group (container) (typed FeaturePython)
  n = 8
  ref = H_element
FEATURE [App::DocumentObjectGroupPython] O_element086  label="O_element : 047"  # scripted group (container) (typed FeaturePython)
  n = 1
  ref = O_element
FEATURE [App::DocumentObjectGroupPython] G4_N_PROPYL_ALCOHOL  label="G4_N-PROPYL_ALCOHOL"  # scripted group (container) (typed FeaturePython)
  Dunit = g/cm3
  Dvalue = 0.8035
  Group = -> [C_element098,H_element090,O_element086]
  conduct = 2
  density = 1
  expand = 3
  formula = G4_N-PROPYL_ALCOHOL
  name = G4_N-PROPYL_ALCOHOL
  specific = 4
FEATURE [App::DocumentObjectGroupPython] C_element099  label="C_element : 057"  # scripted group (container) (typed FeaturePython)
  n = 5
  ref = C_element
FEATURE [App::DocumentObjectGroupPython] H_element091  label="H_element : 052"  # scripted group (container) (typed FeaturePython)
  n = 5
  ref = H_element
FEATURE [App::DocumentObjectGroupPython] N_element038  label="N_element : 017"  # scripted group (container) (typed FeaturePython)
  n = 1
  ref = N_element
FEATURE [App::DocumentObjectGroupPython] G4_PYRIDINE  # scripted group (container) (typed FeaturePython)
  Dunit = g/cm3
  Dvalue = 0.9819
  Group = -> [C_element099,H_element091,N_element038]
  conduct = 2
  density = 1
  expand = 3
  formula = G4_PYRIDINE
  name = G4_PYRIDINE
  specific = 4
FEATURE [App::DocumentObjectGroupPython] H_element092  label="H_element : 0.144"  # scripted group (container) (typed FeaturePython)
  n = 0.143711
FEATURE [App::DocumentObjectGroupPython] C_element100  label="C_element : 0.856"  # scripted group (container) (typed FeaturePython)
  n = 0.856289
FEATURE [App::DocumentObjectGroupPython] G4_RUBBER_BUTYL  # scripted group (container) (typed FeaturePython)
  Dunit = g/cm3
  Dvalue = 0.92
  Group = -> [H_element092,C_element100]
  conduct = 2
  density = 1
  expand = 3
  formula = G4_RUBBER_BUTYL
  name = G4_RUBBER_BUTYL
  specific = 4
FEATURE [App::DocumentObjectGroupPython] H_element093  label="H_element : 0.118"  # scripted group (container) (typed FeaturePython)
  n = 0.118371
FEATURE [App::DocumentObjectGroupPython] C_element101  label="C_element : 0.882"  # scripted group (container) (typed FeaturePython)
  n = 0.881629
FEATURE [App::DocumentObjectGroupPython] G4_RUBBER_NATURAL  # scripted group (container) (typed FeaturePython)
  Dunit = g/cm3
  Dvalue = 0.92
  Group = -> [H_element093,C_element101]
  conduct = 2
  density = 1
  expand = 3
  formula = G4_RUBBER_NATURAL
  name = G4_RUBBER_NATURAL
  specific = 4
FEATURE [App::DocumentObjectGroupPython] H_element094  label="H_element : 0.145"  # scripted group (container) (typed FeaturePython)
  n = 0.05692
FEATURE [App::DocumentObjectGroupPython] C_element102  label="C_element : 0.543"  # scripted group (container) (typed FeaturePython)
  n = 0.542646
FEATURE [App::DocumentObjectGroupPython] Cl_element021  label="Cl_element : 0.400"  # scripted group (container) (typed FeaturePython)
  n = 0.400434
FEATURE [App::DocumentObjectGroupPython] G4_RUBBER_NEOPRENE  # scripted group (container) (typed FeaturePython)
  Dunit = g/cm3
  Dvalue = 1.23
  Group = -> [H_element094,C_element102,Cl_element021]
  conduct = 2
  density = 1
  expand = 3
  formula = G4_RUBBER_NEOPRENE
  name = G4_RUBBER_NEOPRENE
  specific = 4
FEATURE [App::DocumentObjectGroupPython] Si_element006  label="Si_element : 1"  # scripted group (container) (typed FeaturePython)
  n = 1
  ref = Si_element
FEATURE [App::DocumentObjectGroupPython] O_element087  label="O_element : 048"  # scripted group (container) (typed FeaturePython)
  n = 2
  ref = O_element
FEATURE [App::DocumentObjectGroupPython] G4_SILICON_DIOXIDE  # scripted group (container) (typed FeaturePython)
  Dunit = g/cm3
  Dvalue = 2.32
  Group = -> [Si_element006,O_element087]
  conduct = 2
  density = 1
  expand = 3
  formula = G4_SILICON_DIOXIDE
  name = G4_SILICON_DIOXIDE
  specific = 4
FEATURE [App::DocumentObjectGroupPython] Ag_element002  label="Ag_element : 1"  # scripted group (container) (typed FeaturePython)
  n = 1
  ref = Ag_element
FEATURE [App::DocumentObjectGroupPython] Br_element005  label="Br_element : 003"  # scripted group (container) (typed FeaturePython)
  n = 1
  ref = Br_element
FEATURE [App::DocumentObjectGroupPython] G4_SILVER_BROMIDE  # scripted group (container) (typed FeaturePython)
  Dunit = g/cm3
  Dvalue = 6.473
  Group = -> [Ag_element002,Br_element005]
  conduct = 2
  density = 1
  expand = 3
  formula = G4_SILVER_BROMIDE
  name = G4_SILVER_BROMIDE
  specific = 4
FEATURE [App::DocumentObjectGroupPython] Ag_element003  label="Ag_element : 002"  # scripted group (container) (typed FeaturePython)
  n = 1
  ref = Ag_element
FEATURE [App::DocumentObjectGroupPython] Cl_element022  label="Cl_element : 011"  # scripted group (container) (typed FeaturePython)
  n = 1
  ref = Cl_element
FEATURE [App::DocumentObjectGroupPython] G4_SILVER_CHLORIDE  # scripted group (container) (typed FeaturePython)
  Dunit = g/cm3
  Dvalue = 5.56
  Group = -> [Ag_element003,Cl_element022]
  conduct = 2
  density = 1
  expand = 3
  formula = G4_SILVER_CHLORIDE
  name = G4_SILVER_CHLORIDE
  specific = 4
FEATURE [App::DocumentObjectGroupPython] Br_element006  label="Br_element : 0.423"  # scripted group (container) (typed FeaturePython)
  n = 0.422895
FEATURE [App::DocumentObjectGroupPython] Ag_element004  label="Ag_element : 0.574"  # scripted group (container) (typed FeaturePython)
  n = 0.573748
FEATURE [App::DocumentObjectGroupPython] I_element007  label="I_element : 0.649"  # scripted group (container) (typed FeaturePython)
  n = 0.003357
FEATURE [App::DocumentObjectGroupPython] G4_SILVER_HALIDES  # scripted group (container) (typed FeaturePython)
  Dunit = g/cm3
  Dvalue = 6.47
  Group = -> [Br_element006,Ag_element004,I_element007]
  conduct = 2
  density = 1
  expand = 3
  formula = G4_SILVER_HALIDES
  name = G4_SILVER_HALIDES
  specific = 4
FEATURE [App::DocumentObjectGroupPython] Ag_element005  label="Ag_element : 003"  # scripted group (container) (typed FeaturePython)
  n = 1
  ref = Ag_element
FEATURE [App::DocumentObjectGroupPython] I_element008  label="I_element : 004"  # scripted group (container) (typed FeaturePython)
  n = 1
  ref = I_element
FEATURE [App::DocumentObjectGroupPython] G4_SILVER_IODIDE  # scripted group (container) (typed FeaturePython)
  Dunit = g/cm3
  Dvalue = 6.01
  Group = -> [Ag_element005,I_element008]
  conduct = 2
  density = 1
  expand = 3
  formula = G4_SILVER_IODIDE
  name = G4_SILVER_IODIDE
  specific = 4
FEATURE [App::DocumentObjectGroupPython] H_element095  label="H_element : 0.100"  # scripted group (container) (typed FeaturePython)
  n = 0.1
FEATURE [App::DocumentObjectGroupPython] C_element103  label="C_element : 0.204"  # scripted group (container) (typed FeaturePython)
  n = 0.204
FEATURE [App::DocumentObjectGroupPython] N_element039  label="N_element : 0.759"  # scripted group (container) (typed FeaturePython)
  n = 0.042
FEATURE [App::DocumentObjectGroupPython] O_element088  label="O_element : 0.645"  # scripted group (container) (typed FeaturePython)
  n = 0.645
FEATURE [App::DocumentObjectGroupPython] Na_element013  label="Na_element : 0.100"  # scripted group (container) (typed FeaturePython)
  n = 0.002
FEATURE [App::DocumentObjectGroupPython] P_element009  label="P_element : 0.107"  # scripted group (container) (typed FeaturePython)
  n = 0.001
FEATURE [App::DocumentObjectGroupPython] S_element020  label="S_element : 0.021"  # scripted group (container) (typed FeaturePython)
  n = 0.002
FEATURE [App::DocumentObjectGroupPython] Cl_element023  label="Cl_element : 0.590"  # scripted group (container) (typed FeaturePython)
  n = 0.003
FEATURE [App::DocumentObjectGroupPython] K_element010  label="K_element : 0.001"  # scripted group (container) (typed FeaturePython)
  n = 0.001
FEATURE [App::DocumentObjectGroupPython] G4_SKIN_ICRP  # scripted group (container) (typed FeaturePython)
  Dunit = g/cm3
  Dvalue = 1.09
  Group = -> [H_element095,C_element103,N_element039,O_element088,Na_element013,P_element009,S_element020,Cl_element023,K_element010]
  conduct = 2
  density = 1
  expand = 3
  formula = G4_SKIN_ICRP
  name = G4_SKIN_ICRP
  specific = 4
FEATURE [App::DocumentObjectGroupPython] Na_element014  label="Na_element : 2"  # scripted group (container) (typed FeaturePython)
  n = 2
  ref = Na_element
FEATURE [App::DocumentObjectGroupPython] C_element104  label="C_element : 058"  # scripted group (container) (typed FeaturePython)
  n = 1
  ref = C_element
FEATURE [App::DocumentObjectGroupPython] O_element089  label="O_element : 049"  # scripted group (container) (typed FeaturePython)
  n = 3
  ref = O_element
FEATURE [App::DocumentObjectGroupPython] G4_SODIUM_CARBONATE  # scripted group (container) (typed FeaturePython)
  Dunit = g/cm3
  Dvalue = 2.532
  Group = -> [Na_element014,C_element104,O_element089]
  conduct = 2
  density = 1
  expand = 3
  formula = G4_SODIUM_CARBONATE
  name = G4_SODIUM_CARBONATE
  specific = 4
FEATURE [App::DocumentObjectGroupPython] Na_element015  label="Na_element : 1"  # scripted group (container) (typed FeaturePython)
  n = 1
  ref = Na_element
FEATURE [App::DocumentObjectGroupPython] I_element009  label="I_element : 005"  # scripted group (container) (typed FeaturePython)
  n = 1
  ref = I_element
FEATURE [App::DocumentObjectGroupPython] G4_SODIUM_IODIDE  # scripted group (container) (typed FeaturePython)
  Dunit = g/cm3
  Dvalue = 3.667
  Group = -> [Na_element015,I_element009]
  conduct = 2
  density = 1
  expand = 3
  formula = G4_SODIUM_IODIDE
  name = G4_SODIUM_IODIDE
  specific = 4
FEATURE [App::DocumentObjectGroupPython] Na_element016  label="Na_element : 003"  # scripted group (container) (typed FeaturePython)
  n = 2
  ref = Na_element
FEATURE [App::DocumentObjectGroupPython] O_element090  label="O_element : 050"  # scripted group (container) (typed FeaturePython)
  n = 1
  ref = O_element
FEATURE [App::DocumentObjectGroupPython] G4_SODIUM_MONOXIDE  # scripted group (container) (typed FeaturePython)
  Dunit = g/cm3
  Dvalue = 2.27
  Group = -> [Na_element016,O_element090]
  conduct = 2
  density = 1
  expand = 3
  formula = G4_SODIUM_MONOXIDE
  name = G4_SODIUM_MONOXIDE
  specific = 4
FEATURE [App::DocumentObjectGroupPython] Na_element017  label="Na_element : 004"  # scripted group (container) (typed FeaturePython)
  n = 1
  ref = Na_element
FEATURE [App::DocumentObjectGroupPython] N_element040  label="N_element : 018"  # scripted group (container) (typed FeaturePython)
  n = 1
  ref = N_element
FEATURE [App::DocumentObjectGroupPython] O_element091  label="O_element : 051"  # scripted group (container) (typed FeaturePython)
  n = 3
  ref = O_element
FEATURE [App::DocumentObjectGroupPython] G4_SODIUM_NITRATE  # scripted group (container) (typed FeaturePython)
  Dunit = g/cm3
  Dvalue = 2.261
  Group = -> [Na_element017,N_element040,O_element091]
  conduct = 2
  density = 1
  expand = 3
  formula = G4_SODIUM_NITRATE
  name = G4_SODIUM_NITRATE
  specific = 4
FEATURE [App::DocumentObjectGroupPython] C_element105  label="C_element : 059"  # scripted group (container) (typed FeaturePython)
  n = 14
  ref = C_element
FEATURE [App::DocumentObjectGroupPython] H_element096  label="H_element : 053"  # scripted group (container) (typed FeaturePython)
  n = 12
  ref = H_element
FEATURE [App::DocumentObjectGroupPython] G4_STILBENE  # scripted group (container) (typed FeaturePython)
  Dunit = g/cm3
  Dvalue = 0.9707
  Group = -> [C_element105,H_element096]
  conduct = 2
  density = 1
  expand = 3
  formula = G4_STILBENE
  name = G4_STILBENE
  specific = 4
FEATURE [App::DocumentObjectGroupPython] C_element106  label="C_element : 12"  # scripted group (container) (typed FeaturePython)
  n = 12
  ref = C_element
FEATURE [App::DocumentObjectGroupPython] H_element097  label="H_element : 22"  # scripted group (container) (typed FeaturePython)
  n = 22
  ref = H_element
FEATURE [App::DocumentObjectGroupPython] O_element092  label="O_element : 11"  # scripted group (container) (typed FeaturePython)
  n = 11
  ref = O_element
FEATURE [App::DocumentObjectGroupPython] G4_SUCROSE  # scripted group (container) (typed FeaturePython)
  Dunit = g/cm3
  Dvalue = 1.5805
  Group = -> [C_element106,H_element097,O_element092]
  conduct = 2
  density = 1
  expand = 3
  formula = G4_SUCROSE
  name = G4_SUCROSE
  specific = 4
FEATURE [App::DocumentObjectGroupPython] C_element107  label="C_element : 18"  # scripted group (container) (typed FeaturePython)
  n = 18
  ref = C_element
FEATURE [App::DocumentObjectGroupPython] H_element098  label="H_element : 054"  # scripted group (container) (typed FeaturePython)
  n = 14
  ref = H_element
FEATURE [App::DocumentObjectGroupPython] G4_TERPHENYL  # scripted group (container) (typed FeaturePython)
  Dunit = g/cm3
  Dvalue = 1.24
  Group = -> [C_element107,H_element098]
  conduct = 2
  density = 1
  expand = 3
  formula = G4_TERPHENYL
  name = G4_TERPHENYL
  specific = 4
FEATURE [App::DocumentObjectGroupPython] H_element099  label="H_element : 0.146"  # scripted group (container) (typed FeaturePython)
  n = 0.106
FEATURE [App::DocumentObjectGroupPython] C_element108  label="C_element : 0.883"  # scripted group (container) (typed FeaturePython)
  n = 0.099
FEATURE [App::DocumentObjectGroupPython] N_element041  label="N_element : 0.020"  # scripted group (container) (typed FeaturePython)
  n = 0.02
FEATURE [App::DocumentObjectGroupPython] O_element093  label="O_element : 0.766"  # scripted group (container) (typed FeaturePython)
  n = 0.766
FEATURE [App::DocumentObjectGroupPython] Na_element018  label="Na_element : 0.101"  # scripted group (container) (typed FeaturePython)
  n = 0.002
FEATURE [App::DocumentObjectGroupPython] P_element010  label="P_element : 0.108"  # scripted group (container) (typed FeaturePython)
  n = 0.001
FEATURE [App::DocumentObjectGroupPython] S_element021  label="S_element : 0.022"  # scripted group (container) (typed FeaturePython)
  n = 0.002
FEATURE [App::DocumentObjectGroupPython] Cl_element024  label="Cl_element : 0.002"  # scripted group (container) (typed FeaturePython)
  n = 0.002
FEATURE [App::DocumentObjectGroupPython] K_element011  label="K_element : 0.017"  # scripted group (container) (typed FeaturePython)
  n = 0.002
FEATURE [App::DocumentObjectGroupPython] G4_TESTIS_ICRP  # scripted group (container) (typed FeaturePython)
  Dunit = g/cm3
  Dvalue = 1.04
  Group = -> [H_element099,C_element108,N_element041,O_element093,Na_element018,P_element010,S_element021,Cl_element024,K_element011]
  conduct = 2
  density = 1
  expand = 3
  formula = G4_TESTIS_ICRP
  name = G4_TESTIS_ICRP
  specific = 4
FEATURE [App::DocumentObjectGroupPython] C_element109  label="C_element : 060"  # scripted group (container) (typed FeaturePython)
  n = 2
  ref = C_element
FEATURE [App::DocumentObjectGroupPython] Cl_element025  label="Cl_element : 012"  # scripted group (container) (typed FeaturePython)
  n = 4
  ref = Cl_element
FEATURE [App::DocumentObjectGroupPython] G4_TETRACHLOROETHYLENE  # scripted group (container) (typed FeaturePython)
  Dunit = g/cm3
  Dvalue = 1.625
  Group = -> [C_element109,Cl_element025]
  conduct = 2
  density = 1
  expand = 3
  formula = G4_TETRACHLOROETHYLENE
  name = G4_TETRACHLOROETHYLENE
  specific = 4
FEATURE [App::DocumentObjectGroupPython] Tl_element001  label="Tl_element : 1"  # scripted group (container) (typed FeaturePython)
  n = 1
  ref = Tl_element
FEATURE [App::DocumentObjectGroupPython] Cl_element026  label="Cl_element : 013"  # scripted group (container) (typed FeaturePython)
  n = 1
  ref = Cl_element
FEATURE [App::DocumentObjectGroupPython] G4_THALLIUM_CHLORIDE  # scripted group (container) (typed FeaturePython)
  Dunit = g/cm3
  Dvalue = 7.004
  Group = -> [Tl_element001,Cl_element026]
  conduct = 2
  density = 1
  expand = 3
  formula = G4_THALLIUM_CHLORIDE
  name = G4_THALLIUM_CHLORIDE
  specific = 4
FEATURE [App::DocumentObjectGroupPython] H_element100  label="H_element : 0.147"  # scripted group (container) (typed FeaturePython)
  n = 0.105
FEATURE [App::DocumentObjectGroupPython] C_element110  label="C_element : 0.256"  # scripted group (container) (typed FeaturePython)
  n = 0.256
FEATURE [App::DocumentObjectGroupPython] N_element042  label="N_element : 0.760"  # scripted group (container) (typed FeaturePython)
  n = 0.027
FEATURE [App::DocumentObjectGroupPython] O_element094  label="O_element : 0.602"  # scripted group (container) (typed FeaturePython)
  n = 0.602
FEATURE [App::DocumentObjectGroupPython] Na_element019  label="Na_element : 0.102"  # scripted group (container) (typed FeaturePython)
  n = 0.001
FEATURE [App::DocumentObjectGroupPython] P_element011  label="P_element : 0.109"  # scripted group (container) (typed FeaturePython)
  n = 0.002
FEATURE [App::DocumentObjectGroupPython] S_element022  label="S_element : 0.023"  # scripted group (container) (typed FeaturePython)
  n = 0.003
FEATURE [App::DocumentObjectGroupPython] Cl_element027  label="Cl_element : 0.591"  # scripted group (container) (typed FeaturePython)
  n = 0.002
FEATURE [App::DocumentObjectGroupPython] K_element012  label="K_element : 0.018"  # scripted group (container) (typed FeaturePython)
  n = 0.002
FEATURE [App::DocumentObjectGroupPython] G4_TISSUE_SOFT_ICRP  # scripted group (container) (typed FeaturePython)
  Dunit = g/cm3
  Dvalue = 1.03
  Group = -> [H_element100,C_element110,N_element042,O_element094,Na_element019,P_element011,S_element022,Cl_element027,K_element012]
  conduct = 2
  density = 1
  expand = 3
  formula = G4_TISSUE_SOFT_ICRP
  name = G4_TISSUE_SOFT_ICRP
  specific = 4
FEATURE [App::DocumentObjectGroupPython] H_element101  label="H_element : 0.148"  # scripted group (container) (typed FeaturePython)
  n = 0.101
FEATURE [App::DocumentObjectGroupPython] C_element111  label="C_element : 0.111"  # scripted group (container) (typed FeaturePython)
  n = 0.111
FEATURE [App::DocumentObjectGroupPython] N_element043  label="N_element : 0.026"  # scripted group (container) (typed FeaturePython)
  n = 0.026
FEATURE [App::DocumentObjectGroupPython] O_element095  label="O_element : 0.762"  # scripted group (container) (typed FeaturePython)
  n = 0.762
FEATURE [App::DocumentObjectGroupPython] G4_TISSUE_SOFT_ICRU_4  label="G4_TISSUE_SOFT_ICRU-4"  # scripted group (container) (typed FeaturePython)
  Dunit = g/cm3
  Dvalue = 1
  Group = -> [H_element101,C_element111,N_element043,O_element095]
  conduct = 2
  density = 1
  expand = 3
  formula = G4_TISSUE_SOFT_ICRU-4
  name = G4_TISSUE_SOFT_ICRU-4
  specific = 4
FEATURE [App::DocumentObjectGroupPython] H_element102  label="H_element : 0.149"  # scripted group (container) (typed FeaturePython)
  n = 0.101869
FEATURE [App::DocumentObjectGroupPython] C_element112  label="C_element : 0.456"  # scripted group (container) (typed FeaturePython)
  n = 0.456179
FEATURE [App::DocumentObjectGroupPython] N_element044  label="N_element : 0.761"  # scripted group (container) (typed FeaturePython)
  n = 0.035172
FEATURE [App::DocumentObjectGroupPython] O_element096  label="O_element : 0.407"  # scripted group (container) (typed FeaturePython)
  n = 0.40678
FEATURE [App::DocumentObjectGroupPython] G4_TISSUE_METHANE  label="G4_TISSUE-METHANE"  # scripted group (container) (typed FeaturePython)
  Dunit = g/cm3
  Dvalue = 0.00106409
  Group = -> [H_element102,C_element112,N_element044,O_element096]
  conduct = 2
  density = 1
  expand = 3
  formula = G4_TISSUE-METHANE
  name = G4_TISSUE-METHANE
  specific = 4
FEATURE [App::DocumentObjectGroupPython] H_element103  label="H_element : 0.103"  # scripted group (container) (typed FeaturePython)
  n = 0.102672
FEATURE [App::DocumentObjectGroupPython] C_element113  label="C_element : 0.569"  # scripted group (container) (typed FeaturePython)
  n = 0.56894
FEATURE [App::DocumentObjectGroupPython] N_element045  label="N_element : 0.762"  # scripted group (container) (typed FeaturePython)
  n = 0.035022
FEATURE [App::DocumentObjectGroupPython] O_element097  label="O_element : 0.293"  # scripted group (container) (typed FeaturePython)
  n = 0.293366
FEATURE [App::DocumentObjectGroupPython] G4_TISSUE_PROPANE  label="G4_TISSUE-PROPANE"  # scripted group (container) (typed FeaturePython)
  Dunit = g/cm3
  Dvalue = 0.00182628
  Group = -> [H_element103,C_element113,N_element045,O_element097]
  conduct = 2
  density = 1
  expand = 3
  formula = G4_TISSUE-PROPANE
  name = G4_TISSUE-PROPANE
  specific = 4
FEATURE [App::DocumentObjectGroupPython] Ti_element003  label="Ti_element : 1"  # scripted group (container) (typed FeaturePython)
  n = 1
  ref = Ti_element
FEATURE [App::DocumentObjectGroupPython] O_element098  label="O_element : 052"  # scripted group (container) (typed FeaturePython)
  n = 2
  ref = O_element
FEATURE [App::DocumentObjectGroupPython] G4_TITANIUM_DIOXIDE  # scripted group (container) (typed FeaturePython)
  Dunit = g/cm3
  Dvalue = 4.26
  Group = -> [Ti_element003,O_element098]
  conduct = 2
  density = 1
  expand = 3
  formula = G4_TITANIUM_DIOXIDE
  name = G4_TITANIUM_DIOXIDE
  specific = 4
FEATURE [App::DocumentObjectGroupPython] C_element114  label="C_element : 061"  # scripted group (container) (typed FeaturePython)
  n = 7
  ref = C_element
FEATURE [App::DocumentObjectGroupPython] H_element104  label="H_element : 055"  # scripted group (container) (typed FeaturePython)
  n = 8
  ref = H_element
FEATURE [App::DocumentObjectGroupPython] G4_TOLUENE  # scripted group (container) (typed FeaturePython)
  Dunit = g/cm3
  Dvalue = 0.8669
  Group = -> [C_element114,H_element104]
  conduct = 2
  density = 1
  expand = 3
  formula = G4_TOLUENE
  name = G4_TOLUENE
  specific = 4
FEATURE [App::DocumentObjectGroupPython] C_element115  label="C_element : 062"  # scripted group (container) (typed FeaturePython)
  n = 2
  ref = C_element
FEATURE [App::DocumentObjectGroupPython] H_element105  label="H_element : 056"  # scripted group (container) (typed FeaturePython)
  n = 1
  ref = H_element
FEATURE [App::DocumentObjectGroupPython] Cl_element028  label="Cl_element : 014"  # scripted group (container) (typed FeaturePython)
  n = 3
  ref = Cl_element
FEATURE [App::DocumentObjectGroupPython] G4_TRICHLOROETHYLENE  # scripted group (container) (typed FeaturePython)
  Dunit = g/cm3
  Dvalue = 1.46
  Group = -> [C_element115,H_element105,Cl_element028]
  conduct = 2
  density = 1
  expand = 3
  formula = G4_TRICHLOROETHYLENE
  name = G4_TRICHLOROETHYLENE
  specific = 4
FEATURE [App::DocumentObjectGroupPython] C_element116  label="C_element : 063"  # scripted group (container) (typed FeaturePython)
  n = 6
  ref = C_element
FEATURE [App::DocumentObjectGroupPython] H_element106  label="H_element : 15"  # scripted group (container) (typed FeaturePython)
  n = 15
  ref = H_element
FEATURE [App::DocumentObjectGroupPython] O_element099  label="O_element : 053"  # scripted group (container) (typed FeaturePython)
  n = 4
  ref = O_element
FEATURE [App::DocumentObjectGroupPython] P_element012  label="P_element : 1"  # scripted group (container) (typed FeaturePython)
  n = 1
  ref = P_element
FEATURE [App::DocumentObjectGroupPython] G4_TRIETHYL_PHOSPHATE  # scripted group (container) (typed FeaturePython)
  Dunit = g/cm3
  Dvalue = 1.07
  Group = -> [C_element116,H_element106,O_element099,P_element012]
  conduct = 2
  density = 1
  expand = 3
  formula = G4_TRIETHYL_PHOSPHATE
  name = G4_TRIETHYL_PHOSPHATE
  specific = 4
FEATURE [App::DocumentObjectGroupPython] W_element003  label="W_element : 003"  # scripted group (container) (typed FeaturePython)
  n = 1
  ref = W_element
FEATURE [App::DocumentObjectGroupPython] F_element017  label="F_element : 6"  # scripted group (container) (typed FeaturePython)
  n = 6
  ref = F_element
FEATURE [App::DocumentObjectGroupPython] G4_TUNGSTEN_HEXAFLUORIDE  # scripted group (container) (typed FeaturePython)
  Dunit = g/cm3
  Dvalue = 2.4
  Group = -> [W_element003,F_element017]
  conduct = 2
  density = 1
  expand = 3
  formula = G4_TUNGSTEN_HEXAFLUORIDE
  name = G4_TUNGSTEN_HEXAFLUORIDE
  specific = 4
FEATURE [App::DocumentObjectGroupPython] U_element001  label="U_element : 1"  # scripted group (container) (typed FeaturePython)
  n = 1
  ref = U_element
FEATURE [App::DocumentObjectGroupPython] C_element117  label="C_element : 064"  # scripted group (container) (typed FeaturePython)
  n = 2
  ref = C_element
FEATURE [App::DocumentObjectGroupPython] G4_URANIUM_DICARBIDE  # scripted group (container) (typed FeaturePython)
  Dunit = g/cm3
  Dvalue = 11.28
  Group = -> [U_element001,C_element117]
  conduct = 2
  density = 1
  expand = 3
  formula = G4_URANIUM_DICARBIDE
  name = G4_URANIUM_DICARBIDE
  specific = 4
FEATURE [App::DocumentObjectGroupPython] U_element002  label="U_element : 002"  # scripted group (container) (typed FeaturePython)
  n = 1
  ref = U_element
FEATURE [App::DocumentObjectGroupPython] C_element118  label="C_element : 065"  # scripted group (container) (typed FeaturePython)
  n = 1
  ref = C_element
FEATURE [App::DocumentObjectGroupPython] G4_URANIUM_MONOCARBIDE  # scripted group (container) (typed FeaturePython)
  Dunit = g/cm3
  Dvalue = 13.63
  Group = -> [U_element002,C_element118]
  conduct = 2
  density = 1
  expand = 3
  formula = G4_URANIUM_MONOCARBIDE
  name = G4_URANIUM_MONOCARBIDE
  specific = 4
FEATURE [App::DocumentObjectGroupPython] U_element003  label="U_element : 003"  # scripted group (container) (typed FeaturePython)
  n = 1
  ref = U_element
FEATURE [App::DocumentObjectGroupPython] O_element100  label="O_element : 054"  # scripted group (container) (typed FeaturePython)
  n = 2
  ref = O_element
FEATURE [App::DocumentObjectGroupPython] G4_URANIUM_OXIDE  # scripted group (container) (typed FeaturePython)
  Dunit = g/cm3
  Dvalue = 10.96
  Group = -> [U_element003,O_element100]
  conduct = 2
  density = 1
  expand = 3
  formula = G4_URANIUM_OXIDE
  name = G4_URANIUM_OXIDE
  specific = 4
FEATURE [App::DocumentObjectGroupPython] C_element119  label="C_element : 066"  # scripted group (container) (typed FeaturePython)
  n = 1
  ref = C_element
FEATURE [App::DocumentObjectGroupPython] H_element107  label="H_element : 057"  # scripted group (container) (typed FeaturePython)
  n = 4
  ref = H_element
FEATURE [App::DocumentObjectGroupPython] N_element046  label="N_element : 019"  # scripted group (container) (typed FeaturePython)
  n = 2
  ref = N_element
FEATURE [App::DocumentObjectGroupPython] O_element101  label="O_element : 055"  # scripted group (container) (typed FeaturePython)
  n = 1
  ref = O_element
FEATURE [App::DocumentObjectGroupPython] G4_UREA  # scripted group (container) (typed FeaturePython)
  Dunit = g/cm3
  Dvalue = 1.323
  Group = -> [C_element119,H_element107,N_element046,O_element101]
  conduct = 2
  density = 1
  expand = 3
  formula = G4_UREA
  name = G4_UREA
  specific = 4
FEATURE [App::DocumentObjectGroupPython] C_element120  label="C_element : 067"  # scripted group (container) (typed FeaturePython)
  n = 5
  ref = C_element
FEATURE [App::DocumentObjectGroupPython] H_element108  label="H_element : 058"  # scripted group (container) (typed FeaturePython)
  n = 11
  ref = H_element
FEATURE [App::DocumentObjectGroupPython] N_element047  label="N_element : 020"  # scripted group (container) (typed FeaturePython)
  n = 1
  ref = N_element
FEATURE [App::DocumentObjectGroupPython] O_element102  label="O_element : 056"  # scripted group (container) (typed FeaturePython)
  n = 2
  ref = O_element
FEATURE [App::DocumentObjectGroupPython] G4_VALINE  # scripted group (container) (typed FeaturePython)
  Dunit = g/cm3
  Dvalue = 1.23
  Group = -> [C_element120,H_element108,N_element047,O_element102]
  conduct = 2
  density = 1
  expand = 3
  formula = G4_VALINE
  name = G4_VALINE
  specific = 4
FEATURE [App::DocumentObjectGroupPython] H_element109  label="H_element : 0.009"  # scripted group (container) (typed FeaturePython)
  n = 0.009417
FEATURE [App::DocumentObjectGroupPython] C_element121  label="C_element : 0.281"  # scripted group (container) (typed FeaturePython)
  n = 0.280555
FEATURE [App::DocumentObjectGroupPython] F_element018  label="F_element : 0.710"  # scripted group (container) (typed FeaturePython)
  n = 0.710028
FEATURE [App::DocumentObjectGroupPython] G4_VITON  # scripted group (container) (typed FeaturePython)
  Dunit = g/cm3
  Dvalue = 1.8
  Group = -> [H_element109,C_element121,F_element018]
  conduct = 2
  density = 1
  expand = 3
  formula = G4_VITON
  name = G4_VITON
  specific = 4
FEATURE [App::DocumentObjectGroupPython] H_element110  label="H_element : 059"  # scripted group (container) (typed FeaturePython)
  n = 2
  ref = H_element
FEATURE [App::DocumentObjectGroupPython] O_element103  label="O_element : 057"  # scripted group (container) (typed FeaturePython)
  n = 1
  ref = O_element
FEATURE [App::DocumentObjectGroupPython] G4_WATER  # scripted group (container) (typed FeaturePython)
  Dunit = g/cm3
  Dvalue = 1
  Group = -> [H_element110,O_element103]
  conduct = 2
  density = 1
  expand = 3
  formula = G4_WATER
  name = G4_WATER
  specific = 4
FEATURE [App::DocumentObjectGroupPython] H_element111  label="H_element : 060"  # scripted group (container) (typed FeaturePython)
  n = 2
  ref = H_element
FEATURE [App::DocumentObjectGroupPython] O_element104  label="O_element : 058"  # scripted group (container) (typed FeaturePython)
  n = 1
  ref = O_element
FEATURE [App::DocumentObjectGroupPython] G4_WATER_VAPOR  # scripted group (container) (typed FeaturePython)
  Dunit = g/cm3
  Dvalue = 0.000756182
  Group = -> [H_element111,O_element104]
  conduct = 2
  density = 1
  expand = 3
  formula = G4_WATER_VAPOR
  name = G4_WATER_VAPOR
  specific = 4
FEATURE [App::DocumentObjectGroupPython] C_element122  label="C_element : 068"  # scripted group (container) (typed FeaturePython)
  n = 8
  ref = C_element
FEATURE [App::DocumentObjectGroupPython] H_element112  label="H_element : 061"  # scripted group (container) (typed FeaturePython)
  n = 10
  ref = H_element
FEATURE [App::DocumentObjectGroupPython] G4_XYLENE  # scripted group (container) (typed FeaturePython)
  Dunit = g/cm3
  Dvalue = 0.87
  Group = -> [C_element122,H_element112]
  conduct = 2
  density = 1
  expand = 3
  formula = G4_XYLENE
  name = G4_XYLENE
  specific = 4
FEATURE [App::DocumentObjectGroupPython] C_element123  label="C_element : 069"  # scripted group (container) (typed FeaturePython)
  n = 1
  ref = C_element
FEATURE [App::DocumentObjectGroupPython] G4_GRAPHITE  # scripted group (container) (typed FeaturePython)
  Dunit = g/cm3
  Dvalue = 2.21
  Group = -> [C_element123]
  conduct = 2
  density = 1
  expand = 3
  formula = G4_GRAPHITE
  name = G4_GRAPHITE
  specific = 4
FEATURE [App::DocumentObjectGroupPython] NIST  # scripted group (container) (typed FeaturePython)
  Group = -> [G4_A_150_TISSUE,G4_ACETONE,G4_ACETYLENE,G4_ADENINE,G4_ADIPOSE_TISSUE_ICRP,G4_AIR,G4_ALANINE,G4_ALUMINUM_OXIDE,G4_AMBER,G4_AMMONIA,G4_ANILINE,G4_ANTHRACENE,G4_B_100_BONE,G4_BAKELITE,G4_BARIUM_FLUORIDE,G4_BARIUM_SULFATE,G4_BENZENE,G4_BERYLLIUM_OXIDE,G4_BGO,G4_BLOOD_ICRP,G4_BONE_COMPACT_ICRU,G4_BONE_CORTICAL_ICRP,G4_BORON_CARBIDE,G4_BORON_OXIDE,G4_BRAIN_ICRP,G4_BUTANE,G4_N_BUTYL_ALCOHOL,G4_C_552,+152 more]
FEATURE [App::DocumentObjectGroupPython] H_element113  label="H_element : 062"  # scripted group (container) (typed FeaturePython)
  n = 1
  ref = H_element
FEATURE [App::DocumentObjectGroupPython] G4_H  # scripted group (container) (typed FeaturePython)
  Dunit = g/cm3
  Dvalue = 8.3748e-05
  Group = -> [H_element113]
  conduct = 2
  density = 1
  expand = 3
  formula = H
  name = G4_H
  specific = 4
FEATURE [App::DocumentObjectGroupPython] He_element001  label="He_element : 1"  # scripted group (container) (typed FeaturePython)
  n = 1
  ref = He_element
FEATURE [App::DocumentObjectGroupPython] G4_He  # scripted group (container) (typed FeaturePython)
  Dunit = g/cm3
  Dvalue = 0.000166322
  Group = -> [He_element001]
  conduct = 2
  density = 1
  expand = 3
  formula = He
  name = G4_He
  specific = 4
FEATURE [App::DocumentObjectGroupPython] Li_element008  label="Li_element : 008"  # scripted group (container) (typed FeaturePython)
  n = 1
  ref = Li_element
FEATURE [App::DocumentObjectGroupPython] G4_Li  # scripted group (container) (typed FeaturePython)
  Dunit = g/cm3
  Dvalue = 0.534
  Group = -> [Li_element008]
  conduct = 2
  density = 1
  expand = 3
  formula = Li
  name = G4_Li
  specific = 4
FEATURE [App::DocumentObjectGroupPython] Be_element002  label="Be_element : 002"  # scripted group (container) (typed FeaturePython)
  n = 1
  ref = Be_element
FEATURE [App::DocumentObjectGroupPython] G4_Be  # scripted group (container) (typed FeaturePython)
  Dunit = g/cm3
  Dvalue = 1.848
  Group = -> [Be_element002]
  conduct = 2
  density = 1
  expand = 3
  formula = Be
  name = G4_Be
  specific = 4
FEATURE [App::DocumentObjectGroupPython] B_element007  label="B_element : 007"  # scripted group (container) (typed FeaturePython)
  n = 1
  ref = B_element
FEATURE [App::DocumentObjectGroupPython] G4_B  # scripted group (container) (typed FeaturePython)
  Dunit = g/cm3
  Dvalue = 2.37
  Group = -> [B_element007]
  conduct = 2
  density = 1
  expand = 3
  formula = B
  name = G4_B
  specific = 4
FEATURE [App::DocumentObjectGroupPython] C_element124  label="C_element : 070"  # scripted group (container) (typed FeaturePython)
  n = 1
  ref = C_element
FEATURE [App::DocumentObjectGroupPython] G4_C  # scripted group (container) (typed FeaturePython)
  Dunit = g/cm3
  Dvalue = 2
  Group = -> [C_element124]
  conduct = 2
  density = 1
  expand = 3
  formula = C
  name = G4_C
  specific = 4
FEATURE [App::DocumentObjectGroupPython] N_element048  label="N_element : 021"  # scripted group (container) (typed FeaturePython)
  n = 1
  ref = N_element
FEATURE [App::DocumentObjectGroupPython] G4_N  # scripted group (container) (typed FeaturePython)
  Dunit = g/cm3
  Dvalue = 0.0011652
  Group = -> [N_element048]
  conduct = 2
  density = 1
  expand = 3
  formula = N
  name = G4_N
  specific = 4
FEATURE [App::DocumentObjectGroupPython] O_element105  label="O_element : 059"  # scripted group (container) (typed FeaturePython)
  n = 1
  ref = O_element
FEATURE [App::DocumentObjectGroupPython] G4_O  # scripted group (container) (typed FeaturePython)
  Dunit = g/cm3
  Dvalue = 0.00133151
  Group = -> [O_element105]
  conduct = 2
  density = 1
  expand = 3
  formula = O
  name = G4_O
  specific = 4
FEATURE [App::DocumentObjectGroupPython] F_element019  label="F_element : 008"  # scripted group (container) (typed FeaturePython)
  n = 1
  ref = F_element
FEATURE [App::DocumentObjectGroupPython] G4_F  # scripted group (container) (typed FeaturePython)
  Dunit = g/cm3
  Dvalue = 0.00158029
  Group = -> [F_element019]
  conduct = 2
  density = 1
  expand = 3
  formula = F
  name = G4_F
  specific = 4
FEATURE [App::DocumentObjectGroupPython] Ne_element001  label="Ne_element : 1"  # scripted group (container) (typed FeaturePython)
  n = 1
  ref = Ne_element
FEATURE [App::DocumentObjectGroupPython] G4_Ne  # scripted group (container) (typed FeaturePython)
  Dunit = g/cm3
  Dvalue = 0.000838505
  Group = -> [Ne_element001]
  conduct = 2
  density = 1
  expand = 3
  formula = Ne
  name = G4_Ne
  specific = 4
FEATURE [App::DocumentObjectGroupPython] Na_element020  label="Na_element : 005"  # scripted group (container) (typed FeaturePython)
  n = 1
  ref = Na_element
FEATURE [App::DocumentObjectGroupPython] G4_Na  # scripted group (container) (typed FeaturePython)
  Dunit = g/cm3
  Dvalue = 0.971
  Group = -> [Na_element020]
  conduct = 2
  density = 1
  expand = 3
  formula = Na
  name = G4_Na
  specific = 4
FEATURE [App::DocumentObjectGroupPython] Mg_element011  label="Mg_element : 005"  # scripted group (container) (typed FeaturePython)
  n = 1
  ref = Mg_element
FEATURE [App::DocumentObjectGroupPython] G4_Mg  # scripted group (container) (typed FeaturePython)
  Dunit = g/cm3
  Dvalue = 1.74
  Group = -> [Mg_element011]
  conduct = 2
  density = 1
  expand = 3
  formula = Mg
  name = G4_Mg
  specific = 4
FEATURE [App::DocumentObjectGroupPython] Al_element004  label="Al_element : 1"  # scripted group (container) (typed FeaturePython)
  n = 1
  ref = Al_element
FEATURE [App::DocumentObjectGroupPython] G4_Al  # scripted group (container) (typed FeaturePython)
  Dunit = g/cm3
  Dvalue = 2.699
  Group = -> [Al_element004]
  conduct = 2
  density = 1
  expand = 3
  formula = Al
  name = G4_Al
  specific = 4
FEATURE [App::DocumentObjectGroupPython] Si_element007  label="Si_element : 002"  # scripted group (container) (typed FeaturePython)
  n = 1
  ref = Si_element
FEATURE [App::DocumentObjectGroupPython] G4_Si  # scripted group (container) (typed FeaturePython)
  Dunit = g/cm3
  Dvalue = 2.33
  Group = -> [Si_element007]
  conduct = 2
  density = 1
  expand = 3
  formula = Si
  name = G4_Si
  specific = 4
FEATURE [App::DocumentObjectGroupPython] P_element013  label="P_element : 002"  # scripted group (container) (typed FeaturePython)
  n = 1
  ref = P_element
FEATURE [App::DocumentObjectGroupPython] G4_P  # scripted group (container) (typed FeaturePython)
  Dunit = g/cm3
  Dvalue = 2.2
  Group = -> [P_element013]
  conduct = 2
  density = 1
  expand = 3
  formula = P
  name = G4_P
  specific = 4
FEATURE [App::DocumentObjectGroupPython] S_element023  label="S_element : 007"  # scripted group (container) (typed FeaturePython)
  n = 1
  ref = S_element
FEATURE [App::DocumentObjectGroupPython] G4_S  # scripted group (container) (typed FeaturePython)
  Dunit = g/cm3
  Dvalue = 2
  Group = -> [S_element023]
  conduct = 2
  density = 1
  expand = 3
  formula = S
  name = G4_S
  specific = 4
FEATURE [App::DocumentObjectGroupPython] Cl_element029  label="Cl_element : 015"  # scripted group (container) (typed FeaturePython)
  n = 1
  ref = Cl_element
FEATURE [App::DocumentObjectGroupPython] G4_Cl  # scripted group (container) (typed FeaturePython)
  Dunit = g/cm3
  Dvalue = 0.00299473
  Group = -> [Cl_element029]
  conduct = 2
  density = 1
  expand = 3
  formula = Cl
  name = G4_Cl
  specific = 4
FEATURE [App::DocumentObjectGroupPython] Ar_element002  label="Ar_element : 1"  # scripted group (container) (typed FeaturePython)
  n = 1
  ref = Ar_element
FEATURE [App::DocumentObjectGroupPython] G4_Ar  # scripted group (container) (typed FeaturePython)
  Dunit = g/cm3
  Dvalue = 0.00166201
  Group = -> [Ar_element002]
  conduct = 2
  density = 1
  expand = 3
  formula = Ar
  name = G4_Ar
  specific = 4
FEATURE [App::DocumentObjectGroupPython] K_element013  label="K_element : 003"  # scripted group (container) (typed FeaturePython)
  n = 1
  ref = K_element
FEATURE [App::DocumentObjectGroupPython] G4_K  # scripted group (container) (typed FeaturePython)
  Dunit = g/cm3
  Dvalue = 0.862
  Group = -> [K_element013]
  conduct = 2
  density = 1
  expand = 3
  formula = K
  name = G4_K
  specific = 4
FEATURE [App::DocumentObjectGroupPython] Ca_element014  label="Ca_element : 007"  # scripted group (container) (typed FeaturePython)
  n = 1
  ref = Ca_element
FEATURE [App::DocumentObjectGroupPython] G4_Ca  # scripted group (container) (typed FeaturePython)
  Dunit = g/cm3
  Dvalue = 1.55
  Group = -> [Ca_element014]
  conduct = 2
  density = 1
  expand = 3
  formula = Ca
  name = G4_Ca
  specific = 4
FEATURE [App::DocumentObjectGroupPython] Sc_element001  label="Sc_element : 1"  # scripted group (container) (typed FeaturePython)
  n = 1
  ref = Sc_element
FEATURE [App::DocumentObjectGroupPython] G4_Sc  # scripted group (container) (typed FeaturePython)
  Dunit = g/cm3
  Dvalue = 2.989
  Group = -> [Sc_element001]
  conduct = 2
  density = 1
  expand = 3
  formula = Sc
  name = G4_Sc
  specific = 4
FEATURE [App::DocumentObjectGroupPython] Ti_element004  label="Ti_element : 002"  # scripted group (container) (typed FeaturePython)
  n = 1
  ref = Ti_element
FEATURE [App::DocumentObjectGroupPython] G4_Ti  # scripted group (container) (typed FeaturePython)
  Dunit = g/cm3
  Dvalue = 4.54
  Group = -> [Ti_element004]
  conduct = 2
  density = 1
  expand = 3
  formula = Ti
  name = G4_Ti
  specific = 4
FEATURE [App::DocumentObjectGroupPython] V_element001  label="V_element : 1"  # scripted group (container) (typed FeaturePython)
  n = 1
  ref = V_element
FEATURE [App::DocumentObjectGroupPython] G4_V  # scripted group (container) (typed FeaturePython)
  Dunit = g/cm3
  Dvalue = 6.11
  Group = -> [V_element001]
  conduct = 2
  density = 1
  expand = 3
  formula = V
  name = G4_V
  specific = 4
FEATURE [App::DocumentObjectGroupPython] Cr_element001  label="Cr_element : 1"  # scripted group (container) (typed FeaturePython)
  n = 1
  ref = Cr_element
FEATURE [App::DocumentObjectGroupPython] G4_Cr  # scripted group (container) (typed FeaturePython)
  Dunit = g/cm3
  Dvalue = 7.18
  Group = -> [Cr_element001]
  conduct = 2
  density = 1
  expand = 3
  formula = Cr
  name = G4_Cr
  specific = 4
FEATURE [App::DocumentObjectGroupPython] Mn_element001  label="Mn_element : 1"  # scripted group (container) (typed FeaturePython)
  n = 1
  ref = Mn_element
FEATURE [App::DocumentObjectGroupPython] G4_Mn  # scripted group (container) (typed FeaturePython)
  Dunit = g/cm3
  Dvalue = 7.44
  Group = -> [Mn_element001]
  conduct = 2
  density = 1
  expand = 3
  formula = Mn
  name = G4_Mn
  specific = 4
FEATURE [App::DocumentObjectGroupPython] Fe_element007  label="Fe_element : 004"  # scripted group (container) (typed FeaturePython)
  n = 1
  ref = Fe_element
FEATURE [App::DocumentObjectGroupPython] G4_Fe  # scripted group (container) (typed FeaturePython)
  Dunit = g/cm3
  Dvalue = 7.874
  Group = -> [Fe_element007]
  conduct = 2
  density = 1
  expand = 3
  formula = Fe
  name = G4_Fe
  specific = 4
FEATURE [App::DocumentObjectGroupPython] Co_element001  label="Co_element : 1"  # scripted group (container) (typed FeaturePython)
  n = 1
  ref = Co_element
FEATURE [App::DocumentObjectGroupPython] G4_Co  # scripted group (container) (typed FeaturePython)
  Dunit = g/cm3
  Dvalue = 8.9
  Group = -> [Co_element001]
  conduct = 2
  density = 1
  expand = 3
  formula = Co
  name = G4_Co
  specific = 4
FEATURE [App::DocumentObjectGroupPython] Ni_element001  label="Ni_element : 1"  # scripted group (container) (typed FeaturePython)
  n = 1
  ref = Ni_element
FEATURE [App::DocumentObjectGroupPython] G4_Ni  # scripted group (container) (typed FeaturePython)
  Dunit = g/cm3
  Dvalue = 8.902
  Group = -> [Ni_element001]
  conduct = 2
  density = 1
  expand = 3
  formula = Ni
  name = G4_Ni
  specific = 4
FEATURE [App::DocumentObjectGroupPython] Cu_element001  label="Cu_element : 1"  # scripted group (container) (typed FeaturePython)
  n = 1
  ref = Cu_element
FEATURE [App::DocumentObjectGroupPython] G4_Cu  # scripted group (container) (typed FeaturePython)
  Dunit = g/cm3
  Dvalue = 8.96
  Group = -> [Cu_element001]
  conduct = 2
  density = 1
  expand = 3
  formula = Cu
  name = G4_Cu
  specific = 4
FEATURE [App::DocumentObjectGroupPython] Zn_element001  label="Zn_element : 1"  # scripted group (container) (typed FeaturePython)
  n = 1
  ref = Zn_element
FEATURE [App::DocumentObjectGroupPython] G4_Zn  # scripted group (container) (typed FeaturePython)
  Dunit = g/cm3
  Dvalue = 7.133
  Group = -> [Zn_element001]
  conduct = 2
  density = 1
  expand = 3
  formula = Zn
  name = G4_Zn
  specific = 4
FEATURE [App::DocumentObjectGroupPython] Ga_element002  label="Ga_element : 002"  # scripted group (container) (typed FeaturePython)
  n = 1
  ref = Ga_element
FEATURE [App::DocumentObjectGroupPython] G4_Ga  # scripted group (container) (typed FeaturePython)
  Dunit = g/cm3
  Dvalue = 5.904
  Group = -> [Ga_element002]
  conduct = 2
  density = 1
  expand = 3
  formula = Ga
  name = G4_Ga
  specific = 4
FEATURE [App::DocumentObjectGroupPython] Ge_element002  label="Ge_element : 1"  # scripted group (container) (typed FeaturePython)
  n = 1
  ref = Ge_element
FEATURE [App::DocumentObjectGroupPython] G4_Ge  # scripted group (container) (typed FeaturePython)
  Dunit = g/cm3
  Dvalue = 5.323
  Group = -> [Ge_element002]
  conduct = 2
  density = 1
  expand = 3
  formula = Ge
  name = G4_Ge
  specific = 4
FEATURE [App::DocumentObjectGroupPython] As_element003  label="As_element : 002"  # scripted group (container) (typed FeaturePython)
  n = 1
  ref = As_element
FEATURE [App::DocumentObjectGroupPython] G4_As  # scripted group (container) (typed FeaturePython)
  Dunit = g/cm3
  Dvalue = 5.73
  Group = -> [As_element003]
  conduct = 2
  density = 1
  expand = 3
  formula = As
  name = G4_As
  specific = 4
FEATURE [App::DocumentObjectGroupPython] Se_element001  label="Se_element : 1"  # scripted group (container) (typed FeaturePython)
  n = 1
  ref = Se_element
FEATURE [App::DocumentObjectGroupPython] G4_Se  # scripted group (container) (typed FeaturePython)
  Dunit = g/cm3
  Dvalue = 4.5
  Group = -> [Se_element001]
  conduct = 2
  density = 1
  expand = 3
  formula = Se
  name = G4_Se
  specific = 4
FEATURE [App::DocumentObjectGroupPython] Br_element007  label="Br_element : 004"  # scripted group (container) (typed FeaturePython)
  n = 1
  ref = Br_element
FEATURE [App::DocumentObjectGroupPython] G4_Br  # scripted group (container) (typed FeaturePython)
  Dunit = g/cm3
  Dvalue = 0.0070721
  Group = -> [Br_element007]
  conduct = 2
  density = 1
  expand = 3
  formula = Br
  name = G4_Br
  specific = 4
FEATURE [App::DocumentObjectGroupPython] Kr_element001  label="Kr_element : 1"  # scripted group (container) (typed FeaturePython)
  n = 1
  ref = Kr_element
FEATURE [App::DocumentObjectGroupPython] G4_Kr  # scripted group (container) (typed FeaturePython)
  Dunit = g/cm3
  Dvalue = 0.00347832
  Group = -> [Kr_element001]
  conduct = 2
  density = 1
  expand = 3
  formula = Kr
  name = G4_Kr
  specific = 4
FEATURE [App::DocumentObjectGroupPython] Rb_element001  label="Rb_element : 1"  # scripted group (container) (typed FeaturePython)
  n = 1
  ref = Rb_element
FEATURE [App::DocumentObjectGroupPython] G4_Rb  # scripted group (container) (typed FeaturePython)
  Dunit = g/cm3
  Dvalue = 1.532
  Group = -> [Rb_element001]
  conduct = 2
  density = 1
  expand = 3
  formula = Rb
  name = G4_Rb
  specific = 4
FEATURE [App::DocumentObjectGroupPython] Sr_element001  label="Sr_element : 1"  # scripted group (container) (typed FeaturePython)
  n = 1
  ref = Sr_element
FEATURE [App::DocumentObjectGroupPython] G4_Sr  # scripted group (container) (typed FeaturePython)
  Dunit = g/cm3
  Dvalue = 2.54
  Group = -> [Sr_element001]
  conduct = 2
  density = 1
  expand = 3
  formula = Sr
  name = G4_Sr
  specific = 4
FEATURE [App::DocumentObjectGroupPython] Y_element001  label="Y_element : 1"  # scripted group (container) (typed FeaturePython)
  n = 1
  ref = Y_element
FEATURE [App::DocumentObjectGroupPython] G4_Y  # scripted group (container) (typed FeaturePython)
  Dunit = g/cm3
  Dvalue = 4.469
  Group = -> [Y_element001]
  conduct = 2
  density = 1
  expand = 3
  formula = Y
  name = G4_Y
  specific = 4
FEATURE [App::DocumentObjectGroupPython] Zr_element001  label="Zr_element : 1"  # scripted group (container) (typed FeaturePython)
  n = 1
  ref = Zr_element
FEATURE [App::DocumentObjectGroupPython] G4_Zr  # scripted group (container) (typed FeaturePython)
  Dunit = g/cm3
  Dvalue = 6.506
  Group = -> [Zr_element001]
  conduct = 2
  density = 1
  expand = 3
  formula = Zr
  name = G4_Zr
  specific = 4
FEATURE [App::DocumentObjectGroupPython] Nb_element001  label="Nb_element : 1"  # scripted group (container) (typed FeaturePython)
  n = 1
  ref = Nb_element
FEATURE [App::DocumentObjectGroupPython] G4_Nb  # scripted group (container) (typed FeaturePython)
  Dunit = g/cm3
  Dvalue = 8.57
  Group = -> [Nb_element001]
  conduct = 2
  density = 1
  expand = 3
  formula = Nb
  name = G4_Nb
  specific = 4
FEATURE [App::DocumentObjectGroupPython] Mo_element001  label="Mo_element : 1"  # scripted group (container) (typed FeaturePython)
  n = 1
  ref = Mo_element
FEATURE [App::DocumentObjectGroupPython] G4_Mo  # scripted group (container) (typed FeaturePython)
  Dunit = g/cm3
  Dvalue = 10.22
  Group = -> [Mo_element001]
  conduct = 2
  density = 1
  expand = 3
  formula = Mo
  name = G4_Mo
  specific = 4
FEATURE [App::DocumentObjectGroupPython] Tc_element001  label="Tc_element : 1"  # scripted group (container) (typed FeaturePython)
  n = 1
  ref = Tc_element
FEATURE [App::DocumentObjectGroupPython] G4_Tc  # scripted group (container) (typed FeaturePython)
  Dunit = g/cm3
  Dvalue = 11.5
  Group = -> [Tc_element001]
  conduct = 2
  density = 1
  expand = 3
  formula = Tc
  name = G4_Tc
  specific = 4
FEATURE [App::DocumentObjectGroupPython] Ru_element001  label="Ru_element : 1"  # scripted group (container) (typed FeaturePython)
  n = 1
  ref = Ru_element
FEATURE [App::DocumentObjectGroupPython] G4_Ru  # scripted group (container) (typed FeaturePython)
  Dunit = g/cm3
  Dvalue = 12.41
  Group = -> [Ru_element001]
  conduct = 2
  density = 1
  expand = 3
  formula = Ru
  name = G4_Ru
  specific = 4
FEATURE [App::DocumentObjectGroupPython] Rh_element001  label="Rh_element : 1"  # scripted group (container) (typed FeaturePython)
  n = 1
  ref = Rh_element
FEATURE [App::DocumentObjectGroupPython] G4_Rh  # scripted group (container) (typed FeaturePython)
  Dunit = g/cm3
  Dvalue = 12.41
  Group = -> [Rh_element001]
  conduct = 2
  density = 1
  expand = 3
  formula = Rh
  name = G4_Rh
  specific = 4
FEATURE [App::DocumentObjectGroupPython] Pd_element001  label="Pd_element : 1"  # scripted group (container) (typed FeaturePython)
  n = 1
  ref = Pd_element
FEATURE [App::DocumentObjectGroupPython] G4_Pd  # scripted group (container) (typed FeaturePython)
  Dunit = g/cm3
  Dvalue = 12.02
  Group = -> [Pd_element001]
  conduct = 2
  density = 1
  expand = 3
  formula = Pd
  name = G4_Pd
  specific = 4
FEATURE [App::DocumentObjectGroupPython] Ag_element006  label="Ag_element : 004"  # scripted group (container) (typed FeaturePython)
  n = 1
  ref = Ag_element
FEATURE [App::DocumentObjectGroupPython] G4_Ag  # scripted group (container) (typed FeaturePython)
  Dunit = g/cm3
  Dvalue = 10.5
  Group = -> [Ag_element006]
  conduct = 2
  density = 1
  expand = 3
  formula = Ag
  name = G4_Ag
  specific = 4
FEATURE [App::DocumentObjectGroupPython] Cd_element003  label="Cd_element : 003"  # scripted group (container) (typed FeaturePython)
  n = 1
  ref = Cd_element
FEATURE [App::DocumentObjectGroupPython] G4_Cd  # scripted group (container) (typed FeaturePython)
  Dunit = g/cm3
  Dvalue = 8.65
  Group = -> [Cd_element003]
  conduct = 2
  density = 1
  expand = 3
  formula = Cd
  name = G4_Cd
  specific = 4
FEATURE [App::DocumentObjectGroupPython] In_element001  label="In_element : 1"  # scripted group (container) (typed FeaturePython)
  n = 1
  ref = In_element
FEATURE [App::DocumentObjectGroupPython] G4_In  # scripted group (container) (typed FeaturePython)
  Dunit = g/cm3
  Dvalue = 7.31
  Group = -> [In_element001]
  conduct = 2
  density = 1
  expand = 3
  formula = In
  name = G4_In
  specific = 4
FEATURE [App::DocumentObjectGroupPython] Sn_element001  label="Sn_element : 1"  # scripted group (container) (typed FeaturePython)
  n = 1
  ref = Sn_element
FEATURE [App::DocumentObjectGroupPython] G4_Sn  # scripted group (container) (typed FeaturePython)
  Dunit = g/cm3
  Dvalue = 7.31
  Group = -> [Sn_element001]
  conduct = 2
  density = 1
  expand = 3
  formula = Sn
  name = G4_Sn
  specific = 4
FEATURE [App::DocumentObjectGroupPython] Sb_element001  label="Sb_element : 1"  # scripted group (container) (typed FeaturePython)
  n = 1
  ref = Sb_element
FEATURE [App::DocumentObjectGroupPython] G4_Sb  # scripted group (container) (typed FeaturePython)
  Dunit = g/cm3
  Dvalue = 6.691
  Group = -> [Sb_element001]
  conduct = 2
  density = 1
  expand = 3
  formula = Sb
  name = G4_Sb
  specific = 4
FEATURE [App::DocumentObjectGroupPython] Te_element002  label="Te_element : 002"  # scripted group (container) (typed FeaturePython)
  n = 1
  ref = Te_element
FEATURE [App::DocumentObjectGroupPython] G4_Te  # scripted group (container) (typed FeaturePython)
  Dunit = g/cm3
  Dvalue = 6.24
  Group = -> [Te_element002]
  conduct = 2
  density = 1
  expand = 3
  formula = Te
  name = G4_Te
  specific = 4
FEATURE [App::DocumentObjectGroupPython] I_element010  label="I_element : 006"  # scripted group (container) (typed FeaturePython)
  n = 1
  ref = I_element
FEATURE [App::DocumentObjectGroupPython] G4_I  # scripted group (container) (typed FeaturePython)
  Dunit = g/cm3
  Dvalue = 4.93
  Group = -> [I_element010]
  conduct = 2
  density = 1
  expand = 3
  formula = I
  name = G4_I
  specific = 4
FEATURE [App::DocumentObjectGroupPython] Xe_element001  label="Xe_element : 1"  # scripted group (container) (typed FeaturePython)
  n = 1
  ref = Xe_element
FEATURE [App::DocumentObjectGroupPython] G4_Xe  # scripted group (container) (typed FeaturePython)
  Dunit = g/cm3
  Dvalue = 0.00548536
  Group = -> [Xe_element001]
  conduct = 2
  density = 1
  expand = 3
  formula = Xe
  name = G4_Xe
  specific = 4
FEATURE [App::DocumentObjectGroupPython] Cs_element003  label="Cs_element : 003"  # scripted group (container) (typed FeaturePython)
  n = 1
  ref = Cs_element
FEATURE [App::DocumentObjectGroupPython] G4_Cs  # scripted group (container) (typed FeaturePython)
  Dunit = g/cm3
  Dvalue = 1.873
  Group = -> [Cs_element003]
  conduct = 2
  density = 1
  expand = 3
  formula = Cs
  name = G4_Cs
  specific = 4
FEATURE [App::DocumentObjectGroupPython] Ba_element003  label="Ba_element : 003"  # scripted group (container) (typed FeaturePython)
  n = 1
  ref = Ba_element
FEATURE [App::DocumentObjectGroupPython] G4_Ba  # scripted group (container) (typed FeaturePython)
  Dunit = g/cm3
  Dvalue = 3.5
  Group = -> [Ba_element003]
  conduct = 2
  density = 1
  expand = 3
  formula = Ba
  name = G4_Ba
  specific = 4
FEATURE [App::DocumentObjectGroupPython] La_element003  label="La_element : 003"  # scripted group (container) (typed FeaturePython)
  n = 1
  ref = La_element
FEATURE [App::DocumentObjectGroupPython] G4_La  # scripted group (container) (typed FeaturePython)
  Dunit = g/cm3
  Dvalue = 6.154
  Group = -> [La_element003]
  conduct = 2
  density = 1
  expand = 3
  formula = La
  name = G4_La
  specific = 4
FEATURE [App::DocumentObjectGroupPython] Ce_element002  label="Ce_element : 1"  # scripted group (container) (typed FeaturePython)
  n = 1
  ref = Ce_element
FEATURE [App::DocumentObjectGroupPython] G4_Ce  # scripted group (container) (typed FeaturePython)
  Dunit = g/cm3
  Dvalue = 6.657
  Group = -> [Ce_element002]
  conduct = 2
  density = 1
  expand = 3
  formula = Ce
  name = G4_Ce
  specific = 4
FEATURE [App::DocumentObjectGroupPython] Pr_element001  label="Pr_element : 1"  # scripted group (container) (typed FeaturePython)
  n = 1
  ref = Pr_element
FEATURE [App::DocumentObjectGroupPython] G4_Pr  # scripted group (container) (typed FeaturePython)
  Dunit = g/cm3
  Dvalue = 6.71
  Group = -> [Pr_element001]
  conduct = 2
  density = 1
  expand = 3
  formula = Pr
  name = G4_Pr
  specific = 4
FEATURE [App::DocumentObjectGroupPython] Nd_element001  label="Nd_element : 1"  # scripted group (container) (typed FeaturePython)
  n = 1
  ref = Nd_element
FEATURE [App::DocumentObjectGroupPython] G4_Nd  # scripted group (container) (typed FeaturePython)
  Dunit = g/cm3
  Dvalue = 6.9
  Group = -> [Nd_element001]
  conduct = 2
  density = 1
  expand = 3
  formula = Nd
  name = G4_Nd
  specific = 4
FEATURE [App::DocumentObjectGroupPython] Pm_element001  label="Pm_element : 1"  # scripted group (container) (typed FeaturePython)
  n = 1
  ref = Pm_element
FEATURE [App::DocumentObjectGroupPython] G4_Pm  # scripted group (container) (typed FeaturePython)
  Dunit = g/cm3
  Dvalue = 7.22
  Group = -> [Pm_element001]
  conduct = 2
  density = 1
  expand = 3
  formula = Pm
  name = G4_Pm
  specific = 4
FEATURE [App::DocumentObjectGroupPython] Sm_element001  label="Sm_element : 1"  # scripted group (container) (typed FeaturePython)
  n = 1
  ref = Sm_element
FEATURE [App::DocumentObjectGroupPython] G4_Sm  # scripted group (container) (typed FeaturePython)
  Dunit = g/cm3
  Dvalue = 7.46
  Group = -> [Sm_element001]
  conduct = 2
  density = 1
  expand = 3
  formula = Sm
  name = G4_Sm
  specific = 4
FEATURE [App::DocumentObjectGroupPython] Eu_element001  label="Eu_element : 1"  # scripted group (container) (typed FeaturePython)
  n = 1
  ref = Eu_element
FEATURE [App::DocumentObjectGroupPython] G4_Eu  # scripted group (container) (typed FeaturePython)
  Dunit = g/cm3
  Dvalue = 5.243
  Group = -> [Eu_element001]
  conduct = 2
  density = 1
  expand = 3
  formula = Eu
  name = G4_Eu
  specific = 4
FEATURE [App::DocumentObjectGroupPython] Gd_element002  label="Gd_element : 1"  # scripted group (container) (typed FeaturePython)
  n = 1
  ref = Gd_element
FEATURE [App::DocumentObjectGroupPython] G4_Gd  # scripted group (container) (typed FeaturePython)
  Dunit = g/cm3
  Dvalue = 7.9004
  Group = -> [Gd_element002]
  conduct = 2
  density = 1
  expand = 3
  formula = Gd
  name = G4_Gd
  specific = 4
FEATURE [App::DocumentObjectGroupPython] Tb_element001  label="Tb_element : 1"  # scripted group (container) (typed FeaturePython)
  n = 1
  ref = Tb_element
FEATURE [App::DocumentObjectGroupPython] G4_Tb  # scripted group (container) (typed FeaturePython)
  Dunit = g/cm3
  Dvalue = 8.229
  Group = -> [Tb_element001]
  conduct = 2
  density = 1
  expand = 3
  formula = Tb
  name = G4_Tb
  specific = 4
FEATURE [App::DocumentObjectGroupPython] Dy_element001  label="Dy_element : 1"  # scripted group (container) (typed FeaturePython)
  n = 1
  ref = Dy_element
FEATURE [App::DocumentObjectGroupPython] G4_Dy  # scripted group (container) (typed FeaturePython)
  Dunit = g/cm3
  Dvalue = 8.55
  Group = -> [Dy_element001]
  conduct = 2
  density = 1
  expand = 3
  formula = Dy
  name = G4_Dy
  specific = 4
FEATURE [App::DocumentObjectGroupPython] Ho_element001  label="Ho_element : 1"  # scripted group (container) (typed FeaturePython)
  n = 1
  ref = Ho_element
FEATURE [App::DocumentObjectGroupPython] G4_Ho  # scripted group (container) (typed FeaturePython)
  Dunit = g/cm3
  Dvalue = 8.795
  Group = -> [Ho_element001]
  conduct = 2
  density = 1
  expand = 3
  formula = Ho
  name = G4_Ho
  specific = 4
FEATURE [App::DocumentObjectGroupPython] Er_element001  label="Er_element : 1"  # scripted group (container) (typed FeaturePython)
  n = 1
  ref = Er_element
FEATURE [App::DocumentObjectGroupPython] G4_Er  # scripted group (container) (typed FeaturePython)
  Dunit = g/cm3
  Dvalue = 9.066
  Group = -> [Er_element001]
  conduct = 2
  density = 1
  expand = 3
  formula = Er
  name = G4_Er
  specific = 4
FEATURE [App::DocumentObjectGroupPython] Tm_element001  label="Tm_element : 1"  # scripted group (container) (typed FeaturePython)
  n = 1
  ref = Tm_element
FEATURE [App::DocumentObjectGroupPython] G4_Tm  # scripted group (container) (typed FeaturePython)
  Dunit = g/cm3
  Dvalue = 9.321
  Group = -> [Tm_element001]
  conduct = 2
  density = 1
  expand = 3
  formula = Tm
  name = G4_Tm
  specific = 4
FEATURE [App::DocumentObjectGroupPython] Yb_element001  label="Yb_element : 1"  # scripted group (container) (typed FeaturePython)
  n = 1
  ref = Yb_element
FEATURE [App::DocumentObjectGroupPython] G4_Yb  # scripted group (container) (typed FeaturePython)
  Dunit = g/cm3
  Dvalue = 6.73
  Group = -> [Yb_element001]
  conduct = 2
  density = 1
  expand = 3
  formula = Yb
  name = G4_Yb
  specific = 4
FEATURE [App::DocumentObjectGroupPython] Lu_element001  label="Lu_element : 1"  # scripted group (container) (typed FeaturePython)
  n = 1
  ref = Lu_element
FEATURE [App::DocumentObjectGroupPython] G4_Lu  # scripted group (container) (typed FeaturePython)
  Dunit = g/cm3
  Dvalue = 9.84
  Group = -> [Lu_element001]
  conduct = 2
  density = 1
  expand = 3
  formula = Lu
  name = G4_Lu
  specific = 4
FEATURE [App::DocumentObjectGroupPython] Hf_element001  label="Hf_element : 1"  # scripted group (container) (typed FeaturePython)
  n = 1
  ref = Hf_element
FEATURE [App::DocumentObjectGroupPython] G4_Hf  # scripted group (container) (typed FeaturePython)
  Dunit = g/cm3
  Dvalue = 13.31
  Group = -> [Hf_element001]
  conduct = 2
  density = 1
  expand = 3
  formula = Hf
  name = G4_Hf
  specific = 4
FEATURE [App::DocumentObjectGroupPython] Ta_element001  label="Ta_element : 1"  # scripted group (container) (typed FeaturePython)
  n = 1
  ref = Ta_element
FEATURE [App::DocumentObjectGroupPython] G4_Ta  # scripted group (container) (typed FeaturePython)
  Dunit = g/cm3
  Dvalue = 16.654
  Group = -> [Ta_element001]
  conduct = 2
  density = 1
  expand = 3
  formula = Ta
  name = G4_Ta
  specific = 4
FEATURE [App::DocumentObjectGroupPython] W_element004  label="W_element : 004"  # scripted group (container) (typed FeaturePython)
  n = 1
  ref = W_element
FEATURE [App::DocumentObjectGroupPython] G4_W  # scripted group (container) (typed FeaturePython)
  Dunit = g/cm3
  Dvalue = 19.3
  Group = -> [W_element004]
  conduct = 2
  density = 1
  expand = 3
  formula = W
  name = G4_W
  specific = 4
FEATURE [App::DocumentObjectGroupPython] Re_element001  label="Re_element : 1"  # scripted group (container) (typed FeaturePython)
  n = 1
  ref = Re_element
FEATURE [App::DocumentObjectGroupPython] G4_Re  # scripted group (container) (typed FeaturePython)
  Dunit = g/cm3
  Dvalue = 21.02
  Group = -> [Re_element001]
  conduct = 2
  density = 1
  expand = 3
  formula = Re
  name = G4_Re
  specific = 4
FEATURE [App::DocumentObjectGroupPython] Os_element001  label="Os_element : 1"  # scripted group (container) (typed FeaturePython)
  n = 1
  ref = Os_element
FEATURE [App::DocumentObjectGroupPython] G4_Os  # scripted group (container) (typed FeaturePython)
  Dunit = g/cm3
  Dvalue = 22.57
  Group = -> [Os_element001]
  conduct = 2
  density = 1
  expand = 3
  formula = Os
  name = G4_Os
  specific = 4
FEATURE [App::DocumentObjectGroupPython] Ir_element001  label="Ir_element : 1"  # scripted group (container) (typed FeaturePython)
  n = 1
  ref = Ir_element
FEATURE [App::DocumentObjectGroupPython] G4_Ir  # scripted group (container) (typed FeaturePython)
  Dunit = g/cm3
  Dvalue = 22.42
  Group = -> [Ir_element001]
  conduct = 2
  density = 1
  expand = 3
  formula = Ir
  name = G4_Ir
  specific = 4
FEATURE [App::DocumentObjectGroupPython] Pt_element001  label="Pt_element : 1"  # scripted group (container) (typed FeaturePython)
  n = 1
  ref = Pt_element
FEATURE [App::DocumentObjectGroupPython] G4_Pt  # scripted group (container) (typed FeaturePython)
  Dunit = g/cm3
  Dvalue = 21.45
  Group = -> [Pt_element001]
  conduct = 2
  density = 1
  expand = 3
  formula = Pt
  name = G4_Pt
  specific = 4
FEATURE [App::DocumentObjectGroupPython] Au_element001  label="Au_element : 1"  # scripted group (container) (typed FeaturePython)
  n = 1
  ref = Au_element
FEATURE [App::DocumentObjectGroupPython] G4_Au  # scripted group (container) (typed FeaturePython)
  Dunit = g/cm3
  Dvalue = 19.32
  Group = -> [Au_element001]
  conduct = 2
  density = 1
  expand = 3
  formula = Au
  name = G4_Au
  specific = 4
FEATURE [App::DocumentObjectGroupPython] Hg_element002  label="Hg_element : 002"  # scripted group (container) (typed FeaturePython)
  n = 1
  ref = Hg_element
FEATURE [App::DocumentObjectGroupPython] G4_Hg  # scripted group (container) (typed FeaturePython)
  Dunit = g/cm3
  Dvalue = 13.546
  Group = -> [Hg_element002]
  conduct = 2
  density = 1
  expand = 3
  formula = Hg
  name = G4_Hg
  specific = 4
FEATURE [App::DocumentObjectGroupPython] Tl_element002  label="Tl_element : 002"  # scripted group (container) (typed FeaturePython)
  n = 1
  ref = Tl_element
FEATURE [App::DocumentObjectGroupPython] G4_Tl  # scripted group (container) (typed FeaturePython)
  Dunit = g/cm3
  Dvalue = 11.72
  Group = -> [Tl_element002]
  conduct = 2
  density = 1
  expand = 3
  formula = Tl
  name = G4_Tl
  specific = 4
FEATURE [App::DocumentObjectGroupPython] Pb_element003  label="Pb_element : 1"  # scripted group (container) (typed FeaturePython)
  n = 1
  ref = Pb_element
FEATURE [App::DocumentObjectGroupPython] G4_Pb  # scripted group (container) (typed FeaturePython)
  Dunit = g/cm3
  Dvalue = 11.35
  Group = -> [Pb_element003]
  conduct = 2
  density = 1
  expand = 3
  formula = Pb
  name = G4_Pb
  specific = 4
FEATURE [App::DocumentObjectGroupPython] Bi_element002  label="Bi_element : 1"  # scripted group (container) (typed FeaturePython)
  n = 1
  ref = Bi_element
FEATURE [App::DocumentObjectGroupPython] G4_Bi  # scripted group (container) (typed FeaturePython)
  Dunit = g/cm3
  Dvalue = 9.747
  Group = -> [Bi_element002]
  conduct = 2
  density = 1
  expand = 3
  formula = Bi
  name = G4_Bi
  specific = 4
FEATURE [App::DocumentObjectGroupPython] Po_element001  label="Po_element : 1"  # scripted group (container) (typed FeaturePython)
  n = 1
  ref = Po_element
FEATURE [App::DocumentObjectGroupPython] G4_Po  # scripted group (container) (typed FeaturePython)
  Dunit = g/cm3
  Dvalue = 9.32
  Group = -> [Po_element001]
  conduct = 2
  density = 1
  expand = 3
  formula = Po
  name = G4_Po
  specific = 4
FEATURE [App::DocumentObjectGroupPython] At_element001  label="At_element : 1"  # scripted group (container) (typed FeaturePython)
  n = 1
  ref = At_element
FEATURE [App::DocumentObjectGroupPython] G4_At  # scripted group (container) (typed FeaturePython)
  Dunit = g/cm3
  Dvalue = 9.32
  Group = -> [At_element001]
  conduct = 2
  density = 1
  expand = 3
  formula = At
  name = G4_At
  specific = 4
FEATURE [App::DocumentObjectGroupPython] Rn_element001  label="Rn_element : 1"  # scripted group (container) (typed FeaturePython)
  n = 1
  ref = Rn_element
FEATURE [App::DocumentObjectGroupPython] G4_Rn  # scripted group (container) (typed FeaturePython)
  Dunit = g/cm3
  Dvalue = 0.00900662
  Group = -> [Rn_element001]
  conduct = 2
  density = 1
  expand = 3
  formula = Rn
  name = G4_Rn
  specific = 4
FEATURE [App::DocumentObjectGroupPython] Fr_element001  label="Fr_element : 1"  # scripted group (container) (typed FeaturePython)
  n = 1
  ref = Fr_element
FEATURE [App::DocumentObjectGroupPython] G4_Fr  # scripted group (container) (typed FeaturePython)
  Dunit = g/cm3
  Dvalue = 1
  Group = -> [Fr_element001]
  conduct = 2
  density = 1
  expand = 3
  formula = Fr
  name = G4_Fr
  specific = 4
FEATURE [App::DocumentObjectGroupPython] Ra_element001  label="Ra_element : 1"  # scripted group (container) (typed FeaturePython)
  n = 1
  ref = Ra_element
FEATURE [App::DocumentObjectGroupPython] G4_Ra  # scripted group (container) (typed FeaturePython)
  Dunit = g/cm3
  Dvalue = 5
  Group = -> [Ra_element001]
  conduct = 2
  density = 1
  expand = 3
  formula = Ra
  name = G4_Ra
  specific = 4
FEATURE [App::DocumentObjectGroupPython] Ac_element001  label="Ac_element : 1"  # scripted group (container) (typed FeaturePython)
  n = 1
  ref = Ac_element
FEATURE [App::DocumentObjectGroupPython] G4_Ac  # scripted group (container) (typed FeaturePython)
  Dunit = g/cm3
  Dvalue = 10.07
  Group = -> [Ac_element001]
  conduct = 2
  density = 1
  expand = 3
  formula = Ac
  name = G4_Ac
  specific = 4
FEATURE [App::DocumentObjectGroupPython] Th_element001  label="Th_element : 1"  # scripted group (container) (typed FeaturePython)
  n = 1
  ref = Th_element
FEATURE [App::DocumentObjectGroupPython] G4_Th  # scripted group (container) (typed FeaturePython)
  Dunit = g/cm3
  Dvalue = 11.72
  Group = -> [Th_element001]
  conduct = 2
  density = 1
  expand = 3
  formula = Th
  name = G4_Th
  specific = 4
FEATURE [App::DocumentObjectGroupPython] Pa_element001  label="Pa_element : 1"  # scripted group (container) (typed FeaturePython)
  n = 1
  ref = Pa_element
FEATURE [App::DocumentObjectGroupPython] G4_Pa  # scripted group (container) (typed FeaturePython)
  Dunit = g/cm3
  Dvalue = 15.37
  Group = -> [Pa_element001]
  conduct = 2
  density = 1
  expand = 3
  formula = Pa
  name = G4_Pa
  specific = 4
FEATURE [App::DocumentObjectGroupPython] U_element004  label="U_element : 004"  # scripted group (container) (typed FeaturePython)
  n = 1
  ref = U_element
FEATURE [App::DocumentObjectGroupPython] G4_U  # scripted group (container) (typed FeaturePython)
  Dunit = g/cm3
  Dvalue = 18.95
  Group = -> [U_element004]
  conduct = 2
  density = 1
  expand = 3
  formula = U
  name = G4_U
  specific = 4
FEATURE [App::DocumentObjectGroupPython] Np_element001  label="Np_element : 1"  # scripted group (container) (typed FeaturePython)
  n = 1
  ref = Np_element
FEATURE [App::DocumentObjectGroupPython] G4_Np  # scripted group (container) (typed FeaturePython)
  Dunit = g/cm3
  Dvalue = 20.25
  Group = -> [Np_element001]
  conduct = 2
  density = 1
  expand = 3
  formula = Np
  name = G4_Np
  specific = 4
FEATURE [App::DocumentObjectGroupPython] Pu_element002  label="Pu_element : 002"  # scripted group (container) (typed FeaturePython)
  n = 1
  ref = Pu_element
FEATURE [App::DocumentObjectGroupPython] G4_Pu  # scripted group (container) (typed FeaturePython)
  Dunit = g/cm3
  Dvalue = 19.84
  Group = -> [Pu_element002]
  conduct = 2
  density = 1
  expand = 3
  formula = Pu
  name = G4_Pu
  specific = 4
FEATURE [App::DocumentObjectGroupPython] Am_element001  label="Am_element : 1"  # scripted group (container) (typed FeaturePython)
  n = 1
  ref = Am_element
FEATURE [App::DocumentObjectGroupPython] G4_Am  # scripted group (container) (typed FeaturePython)
  Dunit = g/cm3
  Dvalue = 13.67
  Group = -> [Am_element001]
  conduct = 2
  density = 1
  expand = 3
  formula = Am
  name = G4_Am
  specific = 4
FEATURE [App::DocumentObjectGroupPython] Cm_element001  label="Cm_element : 1"  # scripted group (container) (typed FeaturePython)
  n = 1
  ref = Cm_element
FEATURE [App::DocumentObjectGroupPython] G4_Cm  # scripted group (container) (typed FeaturePython)
  Dunit = g/cm3
  Dvalue = 13.51
  Group = -> [Cm_element001]
  conduct = 2
  density = 1
  expand = 3
  formula = Cm
  name = G4_Cm
  specific = 4
FEATURE [App::DocumentObjectGroupPython] Bk_element001  label="Bk_element : 1"  # scripted group (container) (typed FeaturePython)
  n = 1
  ref = Bk_element
FEATURE [App::DocumentObjectGroupPython] G4_Bk  # scripted group (container) (typed FeaturePython)
  Dunit = g/cm3
  Dvalue = 14
  Group = -> [Bk_element001]
  conduct = 2
  density = 1
  expand = 3
  formula = Bk
  name = G4_Bk
  specific = 4
FEATURE [App::DocumentObjectGroupPython] Cf_element001  label="Cf_element : 1"  # scripted group (container) (typed FeaturePython)
  n = 1
  ref = Cf_element
FEATURE [App::DocumentObjectGroupPython] G4_Cf  # scripted group (container) (typed FeaturePython)
  Dunit = g/cm3
  Dvalue = 10
  Group = -> [Cf_element001]
  conduct = 2
  density = 1
  expand = 3
  formula = Cf
  name = G4_Cf
  specific = 4
FEATURE [App::DocumentObjectGroupPython] Element  # scripted group (container) (typed FeaturePython)
  Group = -> [G4_H,G4_He,G4_Li,G4_Be,G4_B,G4_C,G4_N,G4_O,G4_F,G4_Ne,G4_Na,G4_Mg,G4_Al,G4_Si,G4_P,G4_S,G4_Cl,G4_Ar,G4_K,G4_Ca,G4_Sc,G4_Ti,G4_V,G4_Cr,G4_Mn,G4_Fe,G4_Co,G4_Ni,G4_Cu,G4_Zn,G4_Ga,G4_Ge,G4_As,G4_Se,G4_Br,G4_Kr,G4_Rb,G4_Sr,G4_Y,G4_Zr,G4_Nb,G4_Mo,G4_Tc,G4_Ru,G4_Rh,G4_Pd,G4_Ag,G4_Cd,G4_In,G4_Sn,G4_Sb,G4_Te,G4_I,G4_Xe,G4_Cs,G4_Ba,G4_La,G4_Ce,G4_Pr,G4_Nd,G4_Pm,G4_Sm,G4_Eu,G4_Gd,G4_Tb,G4_Dy,G4_Ho,G4_Er,+30 more]
FEATURE [App::DocumentObjectGroupPython] H_element114  label="H_element : 063"  # scripted group (container) (typed FeaturePython)
  n = 2
  ref = H_element
FEATURE [App::DocumentObjectGroupPython] G4_lH2  # scripted group (container) (typed FeaturePython)
  Dunit = g/cm3
  Dvalue = 0.0708
  Group = -> [H_element114]
  conduct = 2
  density = 1
  expand = 3
  formula = G4_lH2
  name = G4_lH2
  specific = 4
FEATURE [App::DocumentObjectGroupPython] N_element049  label="N_element : 022"  # scripted group (container) (typed FeaturePython)
  n = 2
  ref = N_element
FEATURE [App::DocumentObjectGroupPython] G4_lN2  # scripted group (container) (typed FeaturePython)
  Dunit = g/cm3
  Dvalue = 0.807
  Group = -> [N_element049]
  conduct = 2
  density = 1
  expand = 3
  formula = G4_lN2
  name = G4_lN2
  specific = 4
FEATURE [App::DocumentObjectGroupPython] O_element106  label="O_element : 060"  # scripted group (container) (typed FeaturePython)
  n = 2
  ref = O_element
FEATURE [App::DocumentObjectGroupPython] G4_lO2  # scripted group (container) (typed FeaturePython)
  Dunit = g/cm3
  Dvalue = 1.141
  Group = -> [O_element106]
  conduct = 2
  density = 1
  expand = 3
  formula = G4_lO2
  name = G4_lO2
  specific = 4
FEATURE [App::DocumentObjectGroupPython] Ar_element003  label="Ar_element : 002"  # scripted group (container) (typed FeaturePython)
  n = 1
  ref = Ar_element
FEATURE [App::DocumentObjectGroupPython] G4_lAr  # scripted group (container) (typed FeaturePython)
  Dunit = g/cm3
  Dvalue = 1.396
  Group = -> [Ar_element003]
  conduct = 2
  density = 1
  expand = 3
  formula = G4_lAr
  name = G4_lAr
  specific = 4
FEATURE [App::DocumentObjectGroupPython] Br_element008  label="Br_element : 005"  # scripted group (container) (typed FeaturePython)
  n = 1
  ref = Br_element
FEATURE [App::DocumentObjectGroupPython] G4_lBr  # scripted group (container) (typed FeaturePython)
  Dunit = g/cm3
  Dvalue = 3.1028
  Group = -> [Br_element008]
  conduct = 2
  density = 1
  expand = 3
  formula = G4_lBr
  name = G4_lBr
  specific = 4
FEATURE [App::DocumentObjectGroupPython] Kr_element002  label="Kr_element : 002"  # scripted group (container) (typed FeaturePython)
  n = 1
  ref = Kr_element
FEATURE [App::DocumentObjectGroupPython] G4_lKr  # scripted group (container) (typed FeaturePython)
  Dunit = g/cm3
  Dvalue = 2.418
  Group = -> [Kr_element002]
  conduct = 2
  density = 1
  expand = 3
  formula = G4_lKr
  name = G4_lKr
  specific = 4
FEATURE [App::DocumentObjectGroupPython] Xe_element002  label="Xe_element : 002"  # scripted group (container) (typed FeaturePython)
  n = 1
  ref = Xe_element
FEATURE [App::DocumentObjectGroupPython] G4_lXe  # scripted group (container) (typed FeaturePython)
  Dunit = g/cm3
  Dvalue = 2.953
  Group = -> [Xe_element002]
  conduct = 2
  density = 1
  expand = 3
  formula = G4_lXe
  name = G4_lXe
  specific = 4
FEATURE [App::DocumentObjectGroupPython] O_element107  label="O_element : 061"  # scripted group (container) (typed FeaturePython)
  n = 4
  ref = O_element
FEATURE [App::DocumentObjectGroupPython] Pb_element004  label="Pb_element : 002"  # scripted group (container) (typed FeaturePython)
  n = 1
  ref = Pb_element
FEATURE [App::DocumentObjectGroupPython] W_element005  label="W_element : 005"  # scripted group (container) (typed FeaturePython)
  n = 1
  ref = W_element
FEATURE [App::DocumentObjectGroupPython] G4_PbWO4  # scripted group (container) (typed FeaturePython)
  Dunit = g/cm3
  Dvalue = 8.28
  Group = -> [O_element107,Pb_element004,W_element005]
  conduct = 2
  density = 1
  expand = 3
  formula = G4_PbWO4
  name = G4_PbWO4
  specific = 4
FEATURE [App::DocumentObjectGroupPython] H_element115  label="H_element : 064"  # scripted group (container) (typed FeaturePython)
  n = 1
  ref = H_element
FEATURE [App::DocumentObjectGroupPython] G4_Galactic  # scripted group (container) (typed FeaturePython)
  Dunit = g/cm3
  Dvalue = 0
  Group = -> [H_element115]
  conduct = 2
  density = 1
  expand = 3
  formula = G4_Galactic
  name = G4_Galactic
  specific = 4
FEATURE [App::DocumentObjectGroupPython] C_element125  label="C_element : 071"  # scripted group (container) (typed FeaturePython)
  n = 1
  ref = C_element
FEATURE [App::DocumentObjectGroupPython] G4_GRAPHITE_POROUS  # scripted group (container) (typed FeaturePython)
  Dunit = g/cm3
  Dvalue = 1.7
  Group = -> [C_element125]
  conduct = 2
  density = 1
  expand = 3
  formula = G4_GRAPHITE_POROUS
  name = G4_GRAPHITE_POROUS
  specific = 4
FEATURE [App::DocumentObjectGroupPython] H_element116  label="H_element : 0.150"  # scripted group (container) (typed FeaturePython)
  n = 0.080538
FEATURE [App::DocumentObjectGroupPython] C_element126  label="C_element : 0.600"  # scripted group (container) (typed FeaturePython)
  n = 0.599848
FEATURE [App::DocumentObjectGroupPython] O_element108  label="O_element : 0.320"  # scripted group (container) (typed FeaturePython)
  n = 0.319614
FEATURE [App::DocumentObjectGroupPython] G4_LUCITE  # scripted group (container) (typed FeaturePython)
  Dunit = g/cm3
  Dvalue = 1.19
  Group = -> [H_element116,C_element126,O_element108]
  conduct = 2
  density = 1
  expand = 3
  formula = G4_LUCITE
  name = G4_LUCITE
  specific = 4
FEATURE [App::DocumentObjectGroupPython] Cu_element002  label="Cu_element : 62"  # scripted group (container) (typed FeaturePython)
  n = 62
  ref = Cu_element
FEATURE [App::DocumentObjectGroupPython] Zn_element002  label="Zn_element : 35"  # scripted group (container) (typed FeaturePython)
  n = 35
  ref = Zn_element
FEATURE [App::DocumentObjectGroupPython] Pb_element005  label="Pb_element : 3"  # scripted group (container) (typed FeaturePython)
  n = 3
  ref = Pb_element
FEATURE [App::DocumentObjectGroupPython] G4_BRASS  # scripted group (container) (typed FeaturePython)
  Dunit = g/cm3
  Dvalue = 8.52
  Group = -> [Cu_element002,Zn_element002,Pb_element005]
  conduct = 2
  density = 1
  expand = 3
  formula = G4_BRASS
  name = G4_BRASS
  specific = 4
FEATURE [App::DocumentObjectGroupPython] Cu_element003  label="Cu_element : 89"  # scripted group (container) (typed FeaturePython)
  n = 89
  ref = Cu_element
FEATURE [App::DocumentObjectGroupPython] Zn_element003  label="Zn_element : 9"  # scripted group (container) (typed FeaturePython)
  n = 9
  ref = Zn_element
FEATURE [App::DocumentObjectGroupPython] Pb_element006  label="Pb_element : 2"  # scripted group (container) (typed FeaturePython)
  n = 2
  ref = Pb_element
FEATURE [App::DocumentObjectGroupPython] G4_BRONZE  # scripted group (container) (typed FeaturePython)
  Dunit = g/cm3
  Dvalue = 8.82
  Group = -> [Cu_element003,Zn_element003,Pb_element006]
  conduct = 2
  density = 1
  expand = 3
  formula = G4_BRONZE
  name = G4_BRONZE
  specific = 4
FEATURE [App::DocumentObjectGroupPython] Fe_element008  label="Fe_element : 74"  # scripted group (container) (typed FeaturePython)
  n = 74
  ref = Fe_element
FEATURE [App::DocumentObjectGroupPython] Cr_element002  label="Cr_element : 18"  # scripted group (container) (typed FeaturePython)
  n = 18
  ref = Cr_element
FEATURE [App::DocumentObjectGroupPython] Ni_element002  label="Ni_element : 8"  # scripted group (container) (typed FeaturePython)
  n = 8
  ref = Ni_element
FEATURE [App::DocumentObjectGroupPython] G4_STAINLESS_STEEL  label="G4_STAINLESS-STEEL"  # scripted group (container) (typed FeaturePython)
  Dunit = g/cm3
  Dvalue = 8
  Group = -> [Fe_element008,Cr_element002,Ni_element002]
  conduct = 2
  density = 1
  expand = 3
  formula = G4_STAINLESS-STEEL
  name = G4_STAINLESS-STEEL
  specific = 4
FEATURE [App::DocumentObjectGroupPython] H_element117  label="H_element : 065"  # scripted group (container) (typed FeaturePython)
  n = 18
  ref = H_element
FEATURE [App::DocumentObjectGroupPython] C_element127  label="C_element : 072"  # scripted group (container) (typed FeaturePython)
  n = 12
  ref = C_element
FEATURE [App::DocumentObjectGroupPython] O_element109  label="O_element : 062"  # scripted group (container) (typed FeaturePython)
  n = 7
  ref = O_element
FEATURE [App::DocumentObjectGroupPython] G4_CR39  # scripted group (container) (typed FeaturePython)
  Dunit = g/cm3
  Dvalue = 1.32
  Group = -> [H_element117,C_element127,O_element109]
  conduct = 2
  density = 1
  expand = 3
  formula = G4_CR39
  name = G4_CR39
  specific = 4
FEATURE [App::DocumentObjectGroupPython] H_element118  label="H_element : 38"  # scripted group (container) (typed FeaturePython)
  n = 38
  ref = H_element
FEATURE [App::DocumentObjectGroupPython] C_element128  label="C_element : 073"  # scripted group (container) (typed FeaturePython)
  n = 18
  ref = C_element
FEATURE [App::DocumentObjectGroupPython] O_element110  label="O_element : 063"  # scripted group (container) (typed FeaturePython)
  n = 1
  ref = O_element
FEATURE [App::DocumentObjectGroupPython] G4_OCTADECANOL  # scripted group (container) (typed FeaturePython)
  Dunit = g/cm3
  Dvalue = 0.812
  Group = -> [H_element118,C_element128,O_element110]
  conduct = 2
  density = 1
  expand = 3
  formula = G4_OCTADECANOL
  name = G4_OCTADECANOL
  specific = 4
FEATURE [App::DocumentObjectGroupPython] HEP  # scripted group (container) (typed FeaturePython)
  Group = -> [G4_lH2,G4_lN2,G4_lO2,G4_lAr,G4_lBr,G4_lKr,G4_lXe,G4_PbWO4,G4_Galactic,G4_GRAPHITE_POROUS,G4_LUCITE,G4_BRASS,G4_BRONZE,G4_STAINLESS_STEEL,G4_CR39,G4_OCTADECANOL]
FEATURE [App::DocumentObjectGroupPython] C_element129  label="C_element : 074"  # scripted group (container) (typed FeaturePython)
  n = 14
  ref = C_element
FEATURE [App::DocumentObjectGroupPython] H_element119  label="H_element : 066"  # scripted group (container) (typed FeaturePython)
  n = 10
  ref = H_element
FEATURE [App::DocumentObjectGroupPython] O_element111  label="O_element : 064"  # scripted group (container) (typed FeaturePython)
  n = 2
  ref = O_element
FEATURE [App::DocumentObjectGroupPython] N_element050  label="N_element : 023"  # scripted group (container) (typed FeaturePython)
  n = 2
  ref = N_element
FEATURE [App::DocumentObjectGroupPython] G4_KEVLAR  # scripted group (container) (typed FeaturePython)
  Dunit = g/cm3
  Dvalue = 1.44
  Group = -> [C_element129,H_element119,O_element111,N_element050]
  conduct = 2
  density = 1
  expand = 3
  formula = G4_KEVLAR
  name = G4_KEVLAR
  specific = 4
FEATURE [App::DocumentObjectGroupPython] C_element130  label="C_element : 075"  # scripted group (container) (typed FeaturePython)
  n = 10
  ref = C_element
FEATURE [App::DocumentObjectGroupPython] H_element120  label="H_element : 067"  # scripted group (container) (typed FeaturePython)
  n = 8
  ref = H_element
FEATURE [App::DocumentObjectGroupPython] O_element112  label="O_element : 065"  # scripted group (container) (typed FeaturePython)
  n = 4
  ref = O_element
FEATURE [App::DocumentObjectGroupPython] G4_DACRON  # scripted group (container) (typed FeaturePython)
  Dunit = g/cm3
  Dvalue = 1.4
  Group = -> [C_element130,H_element120,O_element112]
  conduct = 2
  density = 1
  expand = 3
  formula = G4_DACRON
  name = G4_DACRON
  specific = 4
FEATURE [App::DocumentObjectGroupPython] C_element131  label="C_element : 076"  # scripted group (container) (typed FeaturePython)
  n = 4
  ref = C_element
FEATURE [App::DocumentObjectGroupPython] H_element121  label="H_element : 068"  # scripted group (container) (typed FeaturePython)
  n = 5
  ref = H_element
FEATURE [App::DocumentObjectGroupPython] Cl_element030  label="Cl_element : 016"  # scripted group (container) (typed FeaturePython)
  n = 1
  ref = Cl_element
FEATURE [App::DocumentObjectGroupPython] G4_NEOPRENE  # scripted group (container) (typed FeaturePython)
  Dunit = g/cm3
  Dvalue = 1.23
  Group = -> [C_element131,H_element121,Cl_element030]
  conduct = 2
  density = 1
  expand = 3
  formula = G4_NEOPRENE
  name = G4_NEOPRENE
  specific = 4
FEATURE [App::DocumentObjectGroupPython] Space  # scripted group (container) (typed FeaturePython)
  Group = -> [G4_KEVLAR,G4_DACRON,G4_NEOPRENE]
FEATURE [App::DocumentObjectGroupPython] H_element122  label="H_element : 069"  # scripted group (container) (typed FeaturePython)
  n = 5
  ref = H_element
FEATURE [App::DocumentObjectGroupPython] C_element132  label="C_element : 077"  # scripted group (container) (typed FeaturePython)
  n = 4
  ref = C_element
FEATURE [App::DocumentObjectGroupPython] N_element051  label="N_element : 3"  # scripted group (container) (typed FeaturePython)
  n = 3
  ref = N_element
FEATURE [App::DocumentObjectGroupPython] O_element113  label="O_element : 066"  # scripted group (container) (typed FeaturePython)
  n = 1
  ref = O_element
FEATURE [App::DocumentObjectGroupPython] G4_CYTOSINE  # scripted group (container) (typed FeaturePython)
  Dunit = g/cm3
  Dvalue = 1.55
  Group = -> [H_element122,C_element132,N_element051,O_element113]
  conduct = 2
  density = 1
  expand = 3
  formula = G4_CYTOSINE
  name = G4_CYTOSINE
  specific = 4
FEATURE [App::DocumentObjectGroupPython] H_element123  label="H_element : 070"  # scripted group (container) (typed FeaturePython)
  n = 6
  ref = H_element
FEATURE [App::DocumentObjectGroupPython] C_element133  label="C_element : 078"  # scripted group (container) (typed FeaturePython)
  n = 5
  ref = C_element
FEATURE [App::DocumentObjectGroupPython] N_element052  label="N_element : 024"  # scripted group (container) (typed FeaturePython)
  n = 2
  ref = N_element
FEATURE [App::DocumentObjectGroupPython] O_element114  label="O_element : 067"  # scripted group (container) (typed FeaturePython)
  n = 2
  ref = O_element
FEATURE [App::DocumentObjectGroupPython] G4_THYMINE  # scripted group (container) (typed FeaturePython)
  Dunit = g/cm3
  Dvalue = 1.23
  Group = -> [H_element123,C_element133,N_element052,O_element114]
  conduct = 2
  density = 1
  expand = 3
  formula = G4_THYMINE
  name = G4_THYMINE
  specific = 4
FEATURE [App::DocumentObjectGroupPython] H_element124  label="H_element : 071"  # scripted group (container) (typed FeaturePython)
  n = 4
  ref = H_element
FEATURE [App::DocumentObjectGroupPython] C_element134  label="C_element : 079"  # scripted group (container) (typed FeaturePython)
  n = 4
  ref = C_element
FEATURE [App::DocumentObjectGroupPython] N_element053  label="N_element : 025"  # scripted group (container) (typed FeaturePython)
  n = 2
  ref = N_element
FEATURE [App::DocumentObjectGroupPython] O_element115  label="O_element : 068"  # scripted group (container) (typed FeaturePython)
  n = 2
  ref = O_element
FEATURE [App::DocumentObjectGroupPython] G4_URACIL  # scripted group (container) (typed FeaturePython)
  Dunit = g/cm3
  Dvalue = 1.32
  Group = -> [H_element124,C_element134,N_element053,O_element115]
  conduct = 2
  density = 1
  expand = 3
  formula = G4_URACIL
  name = G4_URACIL
  specific = 4
FEATURE [App::DocumentObjectGroupPython] H_element125  label="H_element : 072"  # scripted group (container) (typed FeaturePython)
  n = 4
  ref = H_element
FEATURE [App::DocumentObjectGroupPython] C_element135  label="C_element : 080"  # scripted group (container) (typed FeaturePython)
  n = 5
  ref = C_element
FEATURE [App::DocumentObjectGroupPython] N_element054  label="N_element : 026"  # scripted group (container) (typed FeaturePython)
  n = 5
  ref = N_element
FEATURE [App::DocumentObjectGroupPython] G4_DNA_ADENINE  # scripted group (container) (typed FeaturePython)
  Dunit = g/cm3
  Dvalue = 1
  Group = -> [H_element125,C_element135,N_element054]
  conduct = 2
  density = 1
  expand = 3
  formula = G4_DNA_ADENINE
  name = G4_DNA_ADENINE
  specific = 4
FEATURE [App::DocumentObjectGroupPython] H_element126  label="H_element : 073"  # scripted group (container) (typed FeaturePython)
  n = 4
  ref = H_element
FEATURE [App::DocumentObjectGroupPython] C_element136  label="C_element : 081"  # scripted group (container) (typed FeaturePython)
  n = 5
  ref = C_element
FEATURE [App::DocumentObjectGroupPython] N_element055  label="N_element : 027"  # scripted group (container) (typed FeaturePython)
  n = 5
  ref = N_element
FEATURE [App::DocumentObjectGroupPython] O_element116  label="O_element : 069"  # scripted group (container) (typed FeaturePython)
  n = 1
  ref = O_element
FEATURE [App::DocumentObjectGroupPython] G4_DNA_GUANINE  # scripted group (container) (typed FeaturePython)
  Dunit = g/cm3
  Dvalue = 1
  Group = -> [H_element126,C_element136,N_element055,O_element116]
  conduct = 2
  density = 1
  expand = 3
  formula = G4_DNA_GUANINE
  name = G4_DNA_GUANINE
  specific = 4
FEATURE [App::DocumentObjectGroupPython] H_element127  label="H_element : 074"  # scripted group (container) (typed FeaturePython)
  n = 4
  ref = H_element
FEATURE [App::DocumentObjectGroupPython] C_element137  label="C_element : 082"  # scripted group (container) (typed FeaturePython)
  n = 4
  ref = C_element
FEATURE [App::DocumentObjectGroupPython] N_element056  label="N_element : 028"  # scripted group (container) (typed FeaturePython)
  n = 3
  ref = N_element
FEATURE [App::DocumentObjectGroupPython] O_element117  label="O_element : 070"  # scripted group (container) (typed FeaturePython)
  n = 1
  ref = O_element
FEATURE [App::DocumentObjectGroupPython] G4_DNA_CYTOSINE  # scripted group (container) (typed FeaturePython)
  Dunit = g/cm3
  Dvalue = 1
  Group = -> [H_element127,C_element137,N_element056,O_element117]
  conduct = 2
  density = 1
  expand = 3
  formula = G4_DNA_CYTOSINE
  name = G4_DNA_CYTOSINE
  specific = 4
FEATURE [App::DocumentObjectGroupPython] H_element128  label="H_element : 075"  # scripted group (container) (typed FeaturePython)
  n = 5
  ref = H_element
FEATURE [App::DocumentObjectGroupPython] C_element138  label="C_element : 083"  # scripted group (container) (typed FeaturePython)
  n = 5
  ref = C_element
FEATURE [App::DocumentObjectGroupPython] N_element057  label="N_element : 029"  # scripted group (container) (typed FeaturePython)
  n = 2
  ref = N_element
FEATURE [App::DocumentObjectGroupPython] O_element118  label="O_element : 071"  # scripted group (container) (typed FeaturePython)
  n = 2
  ref = O_element
FEATURE [App::DocumentObjectGroupPython] G4_DNA_THYMINE  # scripted group (container) (typed FeaturePython)
  Dunit = g/cm3
  Dvalue = 1
  Group = -> [H_element128,C_element138,N_element057,O_element118]
  conduct = 2
  density = 1
  expand = 3
  formula = G4_DNA_THYMINE
  name = G4_DNA_THYMINE
  specific = 4
FEATURE [App::DocumentObjectGroupPython] H_element129  label="H_element : 076"  # scripted group (container) (typed FeaturePython)
  n = 3
  ref = H_element
FEATURE [App::DocumentObjectGroupPython] C_element139  label="C_element : 084"  # scripted group (container) (typed FeaturePython)
  n = 4
  ref = C_element
FEATURE [App::DocumentObjectGroupPython] N_element058  label="N_element : 030"  # scripted group (container) (typed FeaturePython)
  n = 2
  ref = N_element
FEATURE [App::DocumentObjectGroupPython] O_element119  label="O_element : 072"  # scripted group (container) (typed FeaturePython)
  n = 2
  ref = O_element
FEATURE [App::DocumentObjectGroupPython] G4_DNA_URACIL  # scripted group (container) (typed FeaturePython)
  Dunit = g/cm3
  Dvalue = 1
  Group = -> [H_element129,C_element139,N_element058,O_element119]
  conduct = 2
  density = 1
  expand = 3
  formula = G4_DNA_URACIL
  name = G4_DNA_URACIL
  specific = 4
FEATURE [App::DocumentObjectGroupPython] H_element130  label="H_element : 077"  # scripted group (container) (typed FeaturePython)
  n = 10
  ref = H_element
FEATURE [App::DocumentObjectGroupPython] C_element140  label="C_element : 085"  # scripted group (container) (typed FeaturePython)
  n = 10
  ref = C_element
FEATURE [App::DocumentObjectGroupPython] N_element059  label="N_element : 031"  # scripted group (container) (typed FeaturePython)
  n = 5
  ref = N_element
FEATURE [App::DocumentObjectGroupPython] O_element120  label="O_element : 073"  # scripted group (container) (typed FeaturePython)
  n = 4
  ref = O_element
FEATURE [App::DocumentObjectGroupPython] G4_DNA_ADENOSINE  # scripted group (container) (typed FeaturePython)
  Dunit = g/cm3
  Dvalue = 1
  Group = -> [H_element130,C_element140,N_element059,O_element120]
  conduct = 2
  density = 1
  expand = 3
  formula = G4_DNA_ADENOSINE
  name = G4_DNA_ADENOSINE
  specific = 4
FEATURE [App::DocumentObjectGroupPython] H_element131  label="H_element : 078"  # scripted group (container) (typed FeaturePython)
  n = 10
  ref = H_element
FEATURE [App::DocumentObjectGroupPython] C_element141  label="C_element : 086"  # scripted group (container) (typed FeaturePython)
  n = 10
  ref = C_element
FEATURE [App::DocumentObjectGroupPython] N_element060  label="N_element : 032"  # scripted group (container) (typed FeaturePython)
  n = 5
  ref = N_element
FEATURE [App::DocumentObjectGroupPython] O_element121  label="O_element : 074"  # scripted group (container) (typed FeaturePython)
  n = 5
  ref = O_element
FEATURE [App::DocumentObjectGroupPython] G4_DNA_GUANOSINE  # scripted group (container) (typed FeaturePython)
  Dunit = g/cm3
  Dvalue = 1
  Group = -> [H_element131,C_element141,N_element060,O_element121]
  conduct = 2
  density = 1
  expand = 3
  formula = G4_DNA_GUANOSINE
  name = G4_DNA_GUANOSINE
  specific = 4
FEATURE [App::DocumentObjectGroupPython] H_element132  label="H_element : 079"  # scripted group (container) (typed FeaturePython)
  n = 10
  ref = H_element
FEATURE [App::DocumentObjectGroupPython] C_element142  label="C_element : 087"  # scripted group (container) (typed FeaturePython)
  n = 9
  ref = C_element
FEATURE [App::DocumentObjectGroupPython] N_element061  label="N_element : 033"  # scripted group (container) (typed FeaturePython)
  n = 3
  ref = N_element
FEATURE [App::DocumentObjectGroupPython] O_element122  label="O_element : 075"  # scripted group (container) (typed FeaturePython)
  n = 5
  ref = O_element
FEATURE [App::DocumentObjectGroupPython] G4_DNA_CYTIDINE  # scripted group (container) (typed FeaturePython)
  Dunit = g/cm3
  Dvalue = 1
  Group = -> [H_element132,C_element142,N_element061,O_element122]
  conduct = 2
  density = 1
  expand = 3
  formula = G4_DNA_CYTIDINE
  name = G4_DNA_CYTIDINE
  specific = 4
FEATURE [App::DocumentObjectGroupPython] H_element133  label="H_element : 080"  # scripted group (container) (typed FeaturePython)
  n = 9
  ref = H_element
FEATURE [App::DocumentObjectGroupPython] C_element143  label="C_element : 088"  # scripted group (container) (typed FeaturePython)
  n = 9
  ref = C_element
FEATURE [App::DocumentObjectGroupPython] N_element062  label="N_element : 034"  # scripted group (container) (typed FeaturePython)
  n = 2
  ref = N_element
FEATURE [App::DocumentObjectGroupPython] O_element123  label="O_element : 076"  # scripted group (container) (typed FeaturePython)
  n = 6
  ref = O_element
FEATURE [App::DocumentObjectGroupPython] G4_DNA_URIDINE  # scripted group (container) (typed FeaturePython)
  Dunit = g/cm3
  Dvalue = 1
  Group = -> [H_element133,C_element143,N_element062,O_element123]
  conduct = 2
  density = 1
  expand = 3
  formula = G4_DNA_URIDINE
  name = G4_DNA_URIDINE
  specific = 4
FEATURE [App::DocumentObjectGroupPython] H_element134  label="H_element : 081"  # scripted group (container) (typed FeaturePython)
  n = 11
  ref = H_element
FEATURE [App::DocumentObjectGroupPython] C_element144  label="C_element : 089"  # scripted group (container) (typed FeaturePython)
  n = 10
  ref = C_element
FEATURE [App::DocumentObjectGroupPython] N_element063  label="N_element : 035"  # scripted group (container) (typed FeaturePython)
  n = 2
  ref = N_element
FEATURE [App::DocumentObjectGroupPython] O_element124  label="O_element : 077"  # scripted group (container) (typed FeaturePython)
  n = 6
  ref = O_element
FEATURE [App::DocumentObjectGroupPython] G4_DNA_METHYLURIDINE  # scripted group (container) (typed FeaturePython)
  Dunit = g/cm3
  Dvalue = 1
  Group = -> [H_element134,C_element144,N_element063,O_element124]
  conduct = 2
  density = 1
  expand = 3
  formula = G4_DNA_METHYLURIDINE
  name = G4_DNA_METHYLURIDINE
  specific = 4
FEATURE [App::DocumentObjectGroupPython] P_element014  label="P_element : 003"  # scripted group (container) (typed FeaturePython)
  n = 1
  ref = P_element
FEATURE [App::DocumentObjectGroupPython] O_element125  label="O_element : 078"  # scripted group (container) (typed FeaturePython)
  n = 3
  ref = O_element
FEATURE [App::DocumentObjectGroupPython] G4_DNA_MONOPHOSPHATE  # scripted group (container) (typed FeaturePython)
  Dunit = g/cm3
  Dvalue = 1
  Group = -> [P_element014,O_element125]
  conduct = 2
  density = 1
  expand = 3
  formula = G4_DNA_MONOPHOSPHATE
  name = G4_DNA_MONOPHOSPHATE
  specific = 4
FEATURE [App::DocumentObjectGroupPython] H_element135  label="H_element : 082"  # scripted group (container) (typed FeaturePython)
  n = 10
  ref = H_element
FEATURE [App::DocumentObjectGroupPython] C_element145  label="C_element : 090"  # scripted group (container) (typed FeaturePython)
  n = 10
  ref = C_element
FEATURE [App::DocumentObjectGroupPython] N_element064  label="N_element : 036"  # scripted group (container) (typed FeaturePython)
  n = 5
  ref = N_element
FEATURE [App::DocumentObjectGroupPython] O_element126  label="O_element : 079"  # scripted group (container) (typed FeaturePython)
  n = 7
  ref = O_element
FEATURE [App::DocumentObjectGroupPython] P_element015  label="P_element : 004"  # scripted group (container) (typed FeaturePython)
  n = 1
  ref = P_element
FEATURE [App::DocumentObjectGroupPython] G4_DNA_A  # scripted group (container) (typed FeaturePython)
  Dunit = g/cm3
  Dvalue = 1
  Group = -> [H_element135,C_element145,N_element064,O_element126,P_element015]
  conduct = 2
  density = 1
  expand = 3
  formula = G4_DNA_A
  name = G4_DNA_A
  specific = 4
FEATURE [App::DocumentObjectGroupPython] H_element136  label="H_element : 083"  # scripted group (container) (typed FeaturePython)
  n = 10
  ref = H_element
FEATURE [App::DocumentObjectGroupPython] C_element146  label="C_element : 091"  # scripted group (container) (typed FeaturePython)
  n = 10
  ref = C_element
FEATURE [App::DocumentObjectGroupPython] N_element065  label="N_element : 037"  # scripted group (container) (typed FeaturePython)
  n = 5
  ref = N_element
FEATURE [App::DocumentObjectGroupPython] O_element127  label="O_element : 8"  # scripted group (container) (typed FeaturePython)
  n = 8
  ref = O_element
FEATURE [App::DocumentObjectGroupPython] P_element016  label="P_element : 005"  # scripted group (container) (typed FeaturePython)
  n = 1
  ref = P_element
FEATURE [App::DocumentObjectGroupPython] G4_DNA_G  # scripted group (container) (typed FeaturePython)
  Dunit = g/cm3
  Dvalue = 1
  Group = -> [H_element136,C_element146,N_element065,O_element127,P_element016]
  conduct = 2
  density = 1
  expand = 3
  formula = G4_DNA_G
  name = G4_DNA_G
  specific = 4
FEATURE [App::DocumentObjectGroupPython] H_element137  label="H_element : 084"  # scripted group (container) (typed FeaturePython)
  n = 10
  ref = H_element
FEATURE [App::DocumentObjectGroupPython] C_element147  label="C_element : 092"  # scripted group (container) (typed FeaturePython)
  n = 9
  ref = C_element
FEATURE [App::DocumentObjectGroupPython] N_element066  label="N_element : 038"  # scripted group (container) (typed FeaturePython)
  n = 3
  ref = N_element
FEATURE [App::DocumentObjectGroupPython] O_element128  label="O_element : 080"  # scripted group (container) (typed FeaturePython)
  n = 8
  ref = O_element
FEATURE [App::DocumentObjectGroupPython] P_element017  label="P_element : 006"  # scripted group (container) (typed FeaturePython)
  n = 1
  ref = P_element
FEATURE [App::DocumentObjectGroupPython] G4_DNA_C  # scripted group (container) (typed FeaturePython)
  Dunit = g/cm3
  Dvalue = 1
  Group = -> [H_element137,C_element147,N_element066,O_element128,P_element017]
  conduct = 2
  density = 1
  expand = 3
  formula = G4_DNA_C
  name = G4_DNA_C
  specific = 4
FEATURE [App::DocumentObjectGroupPython] H_element138  label="H_element : 085"  # scripted group (container) (typed FeaturePython)
  n = 9
  ref = H_element
FEATURE [App::DocumentObjectGroupPython] C_element148  label="C_element : 093"  # scripted group (container) (typed FeaturePython)
  n = 9
  ref = C_element
FEATURE [App::DocumentObjectGroupPython] N_element067  label="N_element : 039"  # scripted group (container) (typed FeaturePython)
  n = 2
  ref = N_element
FEATURE [App::DocumentObjectGroupPython] O_element129  label="O_element : 9"  # scripted group (container) (typed FeaturePython)
  n = 9
  ref = O_element
FEATURE [App::DocumentObjectGroupPython] P_element018  label="P_element : 007"  # scripted group (container) (typed FeaturePython)
  n = 1
  ref = P_element
FEATURE [App::DocumentObjectGroupPython] G4_DNA_U  # scripted group (container) (typed FeaturePython)
  Dunit = g/cm3
  Dvalue = 1
  Group = -> [H_element138,C_element148,N_element067,O_element129,P_element018]
  conduct = 2
  density = 1
  expand = 3
  formula = G4_DNA_U
  name = G4_DNA_U
  specific = 4
FEATURE [App::DocumentObjectGroupPython] H_element139  label="H_element : 086"  # scripted group (container) (typed FeaturePython)
  n = 11
  ref = H_element
FEATURE [App::DocumentObjectGroupPython] C_element149  label="C_element : 094"  # scripted group (container) (typed FeaturePython)
  n = 10
  ref = C_element
FEATURE [App::DocumentObjectGroupPython] N_element068  label="N_element : 040"  # scripted group (container) (typed FeaturePython)
  n = 2
  ref = N_element
FEATURE [App::DocumentObjectGroupPython] O_element130  label="O_element : 081"  # scripted group (container) (typed FeaturePython)
  n = 9
  ref = O_element
FEATURE [App::DocumentObjectGroupPython] P_element019  label="P_element : 008"  # scripted group (container) (typed FeaturePython)
  n = 1
  ref = P_element
FEATURE [App::DocumentObjectGroupPython] G4_DNA_MU  # scripted group (container) (typed FeaturePython)
  Dunit = g/cm3
  Dvalue = 1
  Group = -> [H_element139,C_element149,N_element068,O_element130,P_element019]
  conduct = 2
  density = 1
  expand = 3
  formula = G4_DNA_MU
  name = G4_DNA_MU
  specific = 4
FEATURE [App::DocumentObjectGroupPython] BioChemical  # scripted group (container) (typed FeaturePython)
  Group = -> [G4_CYTOSINE,G4_THYMINE,G4_URACIL,G4_DNA_ADENINE,G4_DNA_GUANINE,G4_DNA_CYTOSINE,G4_DNA_THYMINE,G4_DNA_URACIL,G4_DNA_ADENOSINE,G4_DNA_GUANOSINE,G4_DNA_CYTIDINE,G4_DNA_URIDINE,G4_DNA_METHYLURIDINE,G4_DNA_MONOPHOSPHATE,G4_DNA_A,G4_DNA_G,G4_DNA_C,G4_DNA_U,G4_DNA_MU]
FEATURE [App::DocumentObjectGroupPython] G4Materials  # scripted group (container) (typed FeaturePython)
  Group = -> [NIST,Element,HEP,Space,BioChemical]
  version = 1
FEATURE [App::DocumentObjectGroupPython] Geant4  # scripted group (container) (typed FeaturePython)
  Group = -> [G4Isotopes,G4Elements,G4Materials]
FEATURE [App::DocumentObjectGroupPython] Materials  # scripted group (container) (typed FeaturePython)
  Group = -> [Geant4]
FEATURE [Part::FeaturePython] GDMLBox_WorldBox  # WARN: FeaturePython — macro-defined, semantics opaque (R4)
  lunit = 2
  material = 5
  x = 100
  y = 100
  z = 100
FEATURE [Part::Box] Box  label="Cube"
  AttacherType = Attacher::AttachEngine3D
  Height = 10
  Length = 10
  Placement = pos=(5,0,0) rot=(0,0,1;0rad)
  Width = 10
FEATURE [Part::Chamfer] Chamfer
  Base = -> Box
  Edges = 12 edges r=1: [Edge1,Edge2,Edge3,Edge4,Edge5,Edge6,Edge7,Edge8,Edge9,Edge10,Edge11,Edge12]
  Placement = pos=(0,0,0) rot=(0,0,1;0.523599rad)
FEATURE [Part::Box] Box001  label="Cube001"
  AttacherType = Attacher::AttachEngine3D
  Height = 10
  Length = 10
  Placement = pos=(0,0,0) rot=(1,0,0;0.698132rad)
  Width = 10
FEATURE [Part::Fillet] Fillet
  Base = -> Box001
  Edges = 12 edges r=1: [Edge1,Edge2,Edge3,Edge4,Edge5,Edge6,Edge7,Edge8,Edge9,Edge10,Edge11,Edge12]
  Placement = pos=(0,0,-7) rot=(0,0,1;0rad)
FEATURE [App::Part] Part  label="Part_fillet"
  Group = -> [Box001,Fillet]
  Origin = -> Origin001
  Placement = pos=(-14,0,15) rot=(0,0,1;0rad)
FEATURE [App::Part] Part001  label="Part_chamfer"
  Group = -> [Box,Chamfer]
  Origin = -> Origin002
  Placement = pos=(4,0,15) rot=(0,0,1;0rad)
FEATURE [App::Part] worldVOL
  Group = -> [GDMLBox_WorldBox,Part,Part001]
  Origin = -> Origin
